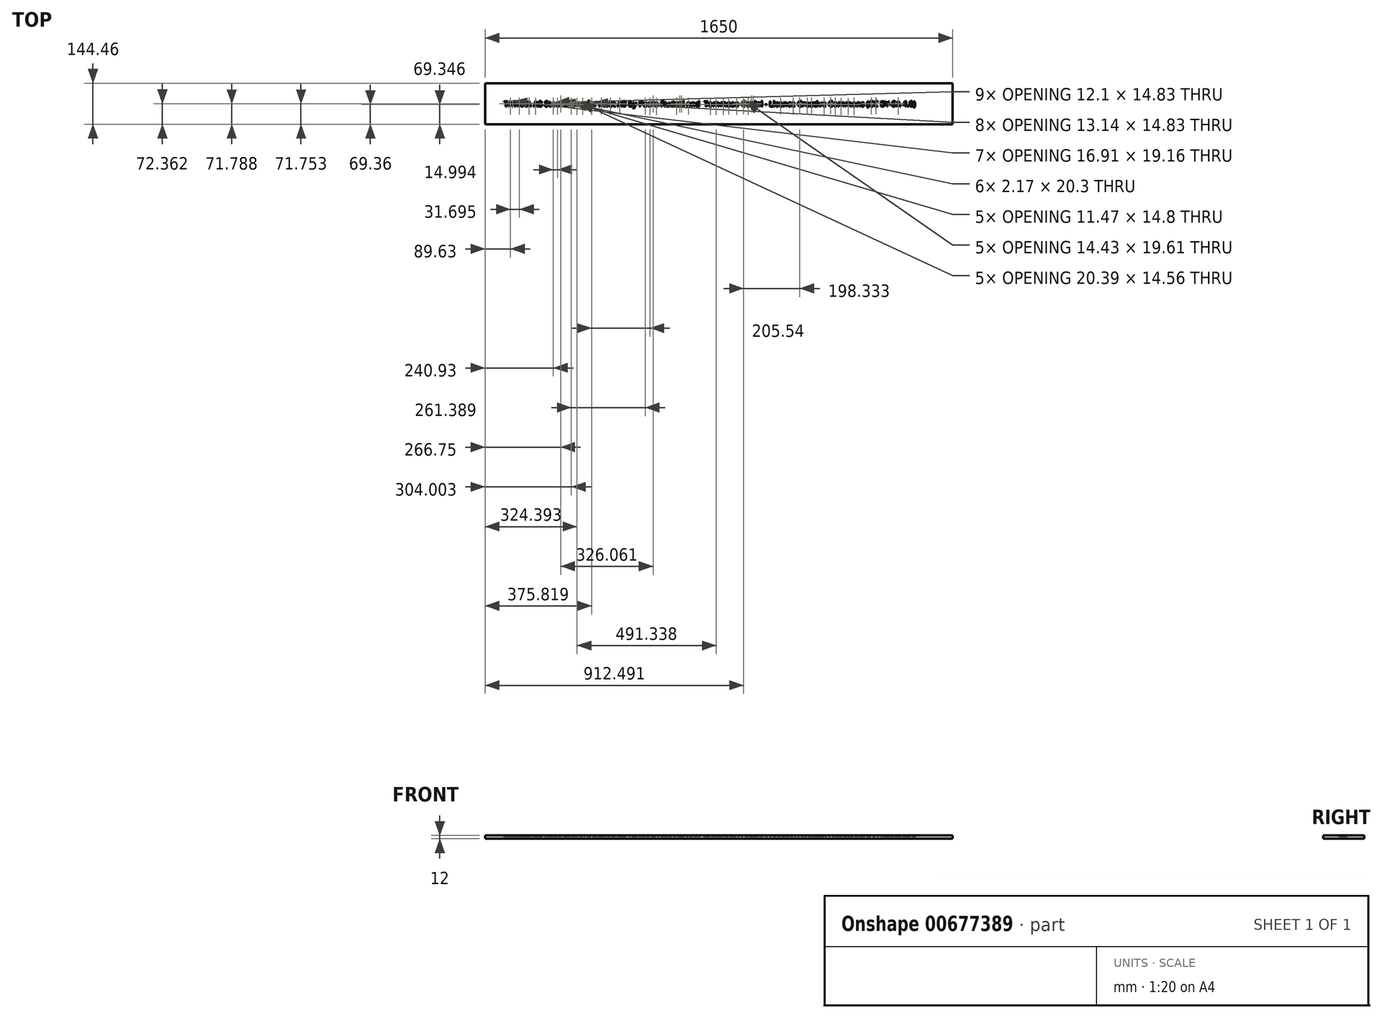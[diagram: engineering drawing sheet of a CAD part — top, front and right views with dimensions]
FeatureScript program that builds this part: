
annotation { "Feature Type Name" : "Feature", "Feature Type Description" : "" }
export const myFeature = defineFeature(function(context is Context, id is Id, definition is map)
    precondition{}
    {
        {
            var Q0;
            Q0=qCreatedBy(makeId("Top.planeOp"),FACE);
            var sketch = newSketch(context, id + "F0", { "sketchPlane" : qUnion([Q0])});
            skText(sketch, "E0", { "text": "TATARA A8 Steel frame for Anet A8 by Paolo Rudelli and  Tommaso Collini - Licence Creative Commons (CC BY-SA 4.0)", "fontName": "OpenSans-Regular.ttf"});
            const initialGuessF0  = {"E0": [-0.56495, -0.011, 1, 0, 0.01924]};
            skSetInitialGuess(sketch, initialGuessF0);
            skSolve(sketch);
        }
        {
            var Q0;
            Q0=qCreatedBy(makeId("Top.planeOp"),FACE);
            var sketch = newSketch(context, id + "F1", { "sketchPlane" : qUnion([Q0])});
            skLineSegment(sketch, "E1.bottom", {"start": v(-631.34, 71.25) * mm, "end": v(1018.66, 71.25) * mm});
            skLineSegment(sketch, "E1.top", {"start": v(-631.34, -73.21) * mm, "end": v(1018.66, -73.21) * mm});
            skLineSegment(sketch, "E1.left", {"start": v(-631.34, 71.25) * mm, "end": v(-631.34, -73.21) * mm});
            skLineSegment(sketch, "E1.right", {"start": v(1018.66, 71.25) * mm, "end": v(1018.66, -73.21) * mm});
            skSolve(sketch);
        }
        {
            var Q0;
            Q0 = qSketchRegion(id + "F0", true);
            extrude(context, id + "F2", {"entities" : qUnion([Q0]), "depth" : 25 * mm, "offsetDistance" : 25 * mm});
        }
        {
            var Q0;
            Q0=makeQuery(id+"F1.imprint","IMPRINT",FACE,{"disambiguationData":[TD([[makeQuery(id+"F1.imprint","IMPRINT",EDGE,{"derivedFrom":sQuery(id+"F1.wireOp",EDGE,"E1.bottom")}),-1.0]])]});
            extrude(context, id + "F3", {"entities" : qUnion([Q0]), "depth" : 18 * mm, "offsetDistance" : 25 * mm, "hasSecondDirection" : true, "secondDirectionOppositeDirection" : false, "secondDirectionDepth" : 6 * mm});
        }
        {
            var Q0;
            Q0=makeQuery(id+"F2.opExtrude","SWEPT_BODY",BODY,{"disambiguationData":[OSD([sQuery(id+"F0.wireOp",EDGE,"E0.sketch_text.stroke-1756"),sQuery(id+"F0.wireOp",EDGE,"E0.sketch_text.stroke-1757"),sQuery(id+"F0.wireOp",EDGE,"E0.sketch_text.stroke-1758"),sQuery(id+"F0.wireOp",EDGE,"E0.sketch_text.stroke-1759"),sQuery(id+"F0.wireOp",EDGE,"E0.sketch_text.stroke-1760"),sQuery(id+"F0.wireOp",EDGE,"E0.sketch_text.stroke-1761"),sQuery(id+"F0.wireOp",EDGE,"E0.sketch_text.stroke-1762"),sQuery(id+"F0.wireOp",EDGE,"E0.sketch_text.stroke-1763"),sQuery(id+"F0.wireOp",EDGE,"E0.sketch_text.stroke-1764"),sQuery(id+"F0.wireOp",EDGE,"E0.sketch_text.stroke-1765"),sQuery(id+"F0.wireOp",EDGE,"E0.sketch_text.stroke-1766"),sQuery(id+"F0.wireOp",EDGE,"E0.sketch_text.stroke-1767"),sQuery(id+"F0.wireOp",EDGE,"E0.sketch_text.stroke-1768"),sQuery(id+"F0.wireOp",EDGE,"E0.sketch_text.stroke-1769"),sQuery(id+"F0.wireOp",EDGE,"E0.sketch_text.stroke-1770"),sQuery(id+"F0.wireOp",EDGE,"E0.sketch_text.stroke-1771"),sQuery(id+"F0.wireOp",EDGE,"E0.sketch_text.stroke-1772"),sQuery(id+"F0.wireOp",EDGE,"E0.sketch_text.stroke-1773"),sQuery(id+"F0.wireOp",EDGE,"E0.sketch_text.stroke-1774")])]});
            var Q1;
            Q1=makeQuery(id+"F2.opExtrude","SWEPT_BODY",BODY,{"disambiguationData":[OSD([sQuery(id+"F0.wireOp",EDGE,"E0.sketch_text.stroke-1705"),sQuery(id+"F0.wireOp",EDGE,"E0.sketch_text.stroke-1706"),sQuery(id+"F0.wireOp",EDGE,"E0.sketch_text.stroke-1707"),sQuery(id+"F0.wireOp",EDGE,"E0.sketch_text.stroke-1708"),sQuery(id+"F0.wireOp",EDGE,"E0.sketch_text.stroke-1709"),sQuery(id+"F0.wireOp",EDGE,"E0.sketch_text.stroke-1710"),sQuery(id+"F0.wireOp",EDGE,"E0.sketch_text.stroke-1711"),sQuery(id+"F0.wireOp",EDGE,"E0.sketch_text.stroke-1712"),sQuery(id+"F0.wireOp",EDGE,"E0.sketch_text.stroke-1713"),sQuery(id+"F0.wireOp",EDGE,"E0.sketch_text.stroke-1714"),sQuery(id+"F0.wireOp",EDGE,"E0.sketch_text.stroke-1715"),sQuery(id+"F0.wireOp",EDGE,"E0.sketch_text.stroke-1716"),sQuery(id+"F0.wireOp",EDGE,"E0.sketch_text.stroke-1717"),sQuery(id+"F0.wireOp",EDGE,"E0.sketch_text.stroke-1718"),sQuery(id+"F0.wireOp",EDGE,"E0.sketch_text.stroke-1719"),sQuery(id+"F0.wireOp",EDGE,"E0.sketch_text.stroke-1720"),sQuery(id+"F0.wireOp",EDGE,"E0.sketch_text.stroke-1721"),sQuery(id+"F0.wireOp",EDGE,"E0.sketch_text.stroke-1722"),sQuery(id+"F0.wireOp",EDGE,"E0.sketch_text.stroke-1723")])]});
            var Q2;
            Q2=makeQuery(id+"F2.opExtrude","SWEPT_BODY",BODY,{"disambiguationData":[OSD([sQuery(id+"F0.wireOp",EDGE,"E0.sketch_text.stroke-1682"),sQuery(id+"F0.wireOp",EDGE,"E0.sketch_text.stroke-1683"),sQuery(id+"F0.wireOp",EDGE,"E0.sketch_text.stroke-1684"),sQuery(id+"F0.wireOp",EDGE,"E0.sketch_text.stroke-1685"),sQuery(id+"F0.wireOp",EDGE,"E0.sketch_text.stroke-1686"),sQuery(id+"F0.wireOp",EDGE,"E0.sketch_text.stroke-1687"),sQuery(id+"F0.wireOp",EDGE,"E0.sketch_text.stroke-1688"),sQuery(id+"F0.wireOp",EDGE,"E0.sketch_text.stroke-1689")])]});
            var Q3;
            Q3=makeQuery(id+"F2.opExtrude","SWEPT_BODY",BODY,{"disambiguationData":[OSD([sQuery(id+"F0.wireOp",EDGE,"E0.sketch_text.stroke-1690"),sQuery(id+"F0.wireOp",EDGE,"E0.sketch_text.stroke-1691"),sQuery(id+"F0.wireOp",EDGE,"E0.sketch_text.stroke-1692"),sQuery(id+"F0.wireOp",EDGE,"E0.sketch_text.stroke-1693"),sQuery(id+"F0.wireOp",EDGE,"E0.sketch_text.stroke-1694"),sQuery(id+"F0.wireOp",EDGE,"E0.sketch_text.stroke-1695"),sQuery(id+"F0.wireOp",EDGE,"E0.sketch_text.stroke-1696"),sQuery(id+"F0.wireOp",EDGE,"E0.sketch_text.stroke-1697"),sQuery(id+"F0.wireOp",EDGE,"E0.sketch_text.stroke-1698"),sQuery(id+"F0.wireOp",EDGE,"E0.sketch_text.stroke-1699"),sQuery(id+"F0.wireOp",EDGE,"E0.sketch_text.stroke-1700"),sQuery(id+"F0.wireOp",EDGE,"E0.sketch_text.stroke-1701"),sQuery(id+"F0.wireOp",EDGE,"E0.sketch_text.stroke-1702"),sQuery(id+"F0.wireOp",EDGE,"E0.sketch_text.stroke-1703"),sQuery(id+"F0.wireOp",EDGE,"E0.sketch_text.stroke-1704")])]});
            var Q4;
            Q4=makeQuery(id+"F2.opExtrude","SWEPT_BODY",BODY,{"disambiguationData":[OSD([sQuery(id+"F0.wireOp",EDGE,"E0.sketch_text.stroke-1741"),sQuery(id+"F0.wireOp",EDGE,"E0.sketch_text.stroke-1742"),sQuery(id+"F0.wireOp",EDGE,"E0.sketch_text.stroke-1743"),sQuery(id+"F0.wireOp",EDGE,"E0.sketch_text.stroke-1744"),sQuery(id+"F0.wireOp",EDGE,"E0.sketch_text.stroke-1745"),sQuery(id+"F0.wireOp",EDGE,"E0.sketch_text.stroke-1746"),sQuery(id+"F0.wireOp",EDGE,"E0.sketch_text.stroke-1747"),sQuery(id+"F0.wireOp",EDGE,"E0.sketch_text.stroke-1748"),sQuery(id+"F0.wireOp",EDGE,"E0.sketch_text.stroke-1749"),sQuery(id+"F0.wireOp",EDGE,"E0.sketch_text.stroke-1750"),sQuery(id+"F0.wireOp",EDGE,"E0.sketch_text.stroke-1751"),sQuery(id+"F0.wireOp",EDGE,"E0.sketch_text.stroke-1752"),sQuery(id+"F0.wireOp",EDGE,"E0.sketch_text.stroke-1753"),sQuery(id+"F0.wireOp",EDGE,"E0.sketch_text.stroke-1754"),sQuery(id+"F0.wireOp",EDGE,"E0.sketch_text.stroke-1755")])]});
            var Q5;
            Q5=makeQuery(id+"F2.opExtrude","SWEPT_BODY",BODY,{"disambiguationData":[OSD([sQuery(id+"F0.wireOp",EDGE,"E0.sketch_text.stroke-0"),sQuery(id+"F0.wireOp",EDGE,"E0.sketch_text.stroke-1"),sQuery(id+"F0.wireOp",EDGE,"E0.sketch_text.stroke-2"),sQuery(id+"F0.wireOp",EDGE,"E0.sketch_text.stroke-3"),sQuery(id+"F0.wireOp",EDGE,"E0.sketch_text.stroke-4"),sQuery(id+"F0.wireOp",EDGE,"E0.sketch_text.stroke-5"),sQuery(id+"F0.wireOp",EDGE,"E0.sketch_text.stroke-6"),sQuery(id+"F0.wireOp",EDGE,"E0.sketch_text.stroke-7")])]});
            var Q6;
            Q6=makeQuery(id+"F2.opExtrude","SWEPT_BODY",BODY,{"disambiguationData":[OSD([sQuery(id+"F0.wireOp",EDGE,"E0.sketch_text.stroke-8"),sQuery(id+"F0.wireOp",EDGE,"E0.sketch_text.stroke-9"),sQuery(id+"F0.wireOp",EDGE,"E0.sketch_text.stroke-10"),sQuery(id+"F0.wireOp",EDGE,"E0.sketch_text.stroke-11"),sQuery(id+"F0.wireOp",EDGE,"E0.sketch_text.stroke-12"),sQuery(id+"F0.wireOp",EDGE,"E0.sketch_text.stroke-13"),sQuery(id+"F0.wireOp",EDGE,"E0.sketch_text.stroke-14"),sQuery(id+"F0.wireOp",EDGE,"E0.sketch_text.stroke-15"),sQuery(id+"F0.wireOp",EDGE,"E0.sketch_text.stroke-16"),sQuery(id+"F0.wireOp",EDGE,"E0.sketch_text.stroke-17"),sQuery(id+"F0.wireOp",EDGE,"E0.sketch_text.stroke-18"),sQuery(id+"F0.wireOp",EDGE,"E0.sketch_text.stroke-19"),sQuery(id+"F0.wireOp",EDGE,"E0.sketch_text.stroke-20")])]});
            var Q7;
            Q7=makeQuery(id+"F2.opExtrude","SWEPT_BODY",BODY,{"disambiguationData":[OSD([sQuery(id+"F0.wireOp",EDGE,"E0.sketch_text.stroke-21"),sQuery(id+"F0.wireOp",EDGE,"E0.sketch_text.stroke-22"),sQuery(id+"F0.wireOp",EDGE,"E0.sketch_text.stroke-23"),sQuery(id+"F0.wireOp",EDGE,"E0.sketch_text.stroke-24"),sQuery(id+"F0.wireOp",EDGE,"E0.sketch_text.stroke-25"),sQuery(id+"F0.wireOp",EDGE,"E0.sketch_text.stroke-26"),sQuery(id+"F0.wireOp",EDGE,"E0.sketch_text.stroke-27"),sQuery(id+"F0.wireOp",EDGE,"E0.sketch_text.stroke-28")])]});
            var Q8;
            Q8=makeQuery(id+"F2.opExtrude","SWEPT_BODY",BODY,{"disambiguationData":[OSD([sQuery(id+"F0.wireOp",EDGE,"E0.sketch_text.stroke-29"),sQuery(id+"F0.wireOp",EDGE,"E0.sketch_text.stroke-30"),sQuery(id+"F0.wireOp",EDGE,"E0.sketch_text.stroke-31"),sQuery(id+"F0.wireOp",EDGE,"E0.sketch_text.stroke-32"),sQuery(id+"F0.wireOp",EDGE,"E0.sketch_text.stroke-33"),sQuery(id+"F0.wireOp",EDGE,"E0.sketch_text.stroke-34"),sQuery(id+"F0.wireOp",EDGE,"E0.sketch_text.stroke-35"),sQuery(id+"F0.wireOp",EDGE,"E0.sketch_text.stroke-36"),sQuery(id+"F0.wireOp",EDGE,"E0.sketch_text.stroke-37"),sQuery(id+"F0.wireOp",EDGE,"E0.sketch_text.stroke-38"),sQuery(id+"F0.wireOp",EDGE,"E0.sketch_text.stroke-39"),sQuery(id+"F0.wireOp",EDGE,"E0.sketch_text.stroke-40"),sQuery(id+"F0.wireOp",EDGE,"E0.sketch_text.stroke-41")])]});
            var Q9;
            Q9=makeQuery(id+"F2.opExtrude","SWEPT_BODY",BODY,{"disambiguationData":[OSD([sQuery(id+"F0.wireOp",EDGE,"E0.sketch_text.stroke-42"),sQuery(id+"F0.wireOp",EDGE,"E0.sketch_text.stroke-43"),sQuery(id+"F0.wireOp",EDGE,"E0.sketch_text.stroke-44"),sQuery(id+"F0.wireOp",EDGE,"E0.sketch_text.stroke-45"),sQuery(id+"F0.wireOp",EDGE,"E0.sketch_text.stroke-46"),sQuery(id+"F0.wireOp",EDGE,"E0.sketch_text.stroke-47"),sQuery(id+"F0.wireOp",EDGE,"E0.sketch_text.stroke-48"),sQuery(id+"F0.wireOp",EDGE,"E0.sketch_text.stroke-49"),sQuery(id+"F0.wireOp",EDGE,"E0.sketch_text.stroke-50"),sQuery(id+"F0.wireOp",EDGE,"E0.sketch_text.stroke-51"),sQuery(id+"F0.wireOp",EDGE,"E0.sketch_text.stroke-52"),sQuery(id+"F0.wireOp",EDGE,"E0.sketch_text.stroke-53"),sQuery(id+"F0.wireOp",EDGE,"E0.sketch_text.stroke-54"),sQuery(id+"F0.wireOp",EDGE,"E0.sketch_text.stroke-55"),sQuery(id+"F0.wireOp",EDGE,"E0.sketch_text.stroke-56"),sQuery(id+"F0.wireOp",EDGE,"E0.sketch_text.stroke-57"),sQuery(id+"F0.wireOp",EDGE,"E0.sketch_text.stroke-58"),sQuery(id+"F0.wireOp",EDGE,"E0.sketch_text.stroke-59")])]});
            var Q10;
            Q10=makeQuery(id+"F2.opExtrude","SWEPT_BODY",BODY,{"disambiguationData":[OSD([sQuery(id+"F0.wireOp",EDGE,"E0.sketch_text.stroke-60"),sQuery(id+"F0.wireOp",EDGE,"E0.sketch_text.stroke-61"),sQuery(id+"F0.wireOp",EDGE,"E0.sketch_text.stroke-62"),sQuery(id+"F0.wireOp",EDGE,"E0.sketch_text.stroke-63"),sQuery(id+"F0.wireOp",EDGE,"E0.sketch_text.stroke-64"),sQuery(id+"F0.wireOp",EDGE,"E0.sketch_text.stroke-65"),sQuery(id+"F0.wireOp",EDGE,"E0.sketch_text.stroke-66"),sQuery(id+"F0.wireOp",EDGE,"E0.sketch_text.stroke-67"),sQuery(id+"F0.wireOp",EDGE,"E0.sketch_text.stroke-68"),sQuery(id+"F0.wireOp",EDGE,"E0.sketch_text.stroke-69"),sQuery(id+"F0.wireOp",EDGE,"E0.sketch_text.stroke-70"),sQuery(id+"F0.wireOp",EDGE,"E0.sketch_text.stroke-71"),sQuery(id+"F0.wireOp",EDGE,"E0.sketch_text.stroke-72")])]});
            var Q11;
            Q11=makeQuery(id+"F2.opExtrude","SWEPT_BODY",BODY,{"disambiguationData":[OSD([sQuery(id+"F0.wireOp",EDGE,"E0.sketch_text.stroke-73"),sQuery(id+"F0.wireOp",EDGE,"E0.sketch_text.stroke-74"),sQuery(id+"F0.wireOp",EDGE,"E0.sketch_text.stroke-75"),sQuery(id+"F0.wireOp",EDGE,"E0.sketch_text.stroke-76"),sQuery(id+"F0.wireOp",EDGE,"E0.sketch_text.stroke-77"),sQuery(id+"F0.wireOp",EDGE,"E0.sketch_text.stroke-78"),sQuery(id+"F0.wireOp",EDGE,"E0.sketch_text.stroke-79"),sQuery(id+"F0.wireOp",EDGE,"E0.sketch_text.stroke-80"),sQuery(id+"F0.wireOp",EDGE,"E0.sketch_text.stroke-81"),sQuery(id+"F0.wireOp",EDGE,"E0.sketch_text.stroke-82"),sQuery(id+"F0.wireOp",EDGE,"E0.sketch_text.stroke-83"),sQuery(id+"F0.wireOp",EDGE,"E0.sketch_text.stroke-84"),sQuery(id+"F0.wireOp",EDGE,"E0.sketch_text.stroke-85"),sQuery(id+"F0.wireOp",EDGE,"E0.sketch_text.stroke-86"),sQuery(id+"F0.wireOp",EDGE,"E0.sketch_text.stroke-87"),sQuery(id+"F0.wireOp",EDGE,"E0.sketch_text.stroke-88"),sQuery(id+"F0.wireOp",EDGE,"E0.sketch_text.stroke-89"),sQuery(id+"F0.wireOp",EDGE,"E0.sketch_text.stroke-90"),sQuery(id+"F0.wireOp",EDGE,"E0.sketch_text.stroke-91")])]});
            var Q12;
            Q12=makeQuery(id+"F2.opExtrude","SWEPT_BODY",BODY,{"disambiguationData":[OSD([sQuery(id+"F0.wireOp",EDGE,"E0.sketch_text.stroke-92"),sQuery(id+"F0.wireOp",EDGE,"E0.sketch_text.stroke-93"),sQuery(id+"F0.wireOp",EDGE,"E0.sketch_text.stroke-94"),sQuery(id+"F0.wireOp",EDGE,"E0.sketch_text.stroke-95"),sQuery(id+"F0.wireOp",EDGE,"E0.sketch_text.stroke-96"),sQuery(id+"F0.wireOp",EDGE,"E0.sketch_text.stroke-97"),sQuery(id+"F0.wireOp",EDGE,"E0.sketch_text.stroke-98"),sQuery(id+"F0.wireOp",EDGE,"E0.sketch_text.stroke-99"),sQuery(id+"F0.wireOp",EDGE,"E0.sketch_text.stroke-100"),sQuery(id+"F0.wireOp",EDGE,"E0.sketch_text.stroke-101"),sQuery(id+"F0.wireOp",EDGE,"E0.sketch_text.stroke-102"),sQuery(id+"F0.wireOp",EDGE,"E0.sketch_text.stroke-103")])]});
            var Q13;
            Q13=makeQuery(id+"F2.opExtrude","SWEPT_BODY",BODY,{"disambiguationData":[OSD([sQuery(id+"F0.wireOp",EDGE,"E0.sketch_text.stroke-104"),sQuery(id+"F0.wireOp",EDGE,"E0.sketch_text.stroke-105"),sQuery(id+"F0.wireOp",EDGE,"E0.sketch_text.stroke-106"),sQuery(id+"F0.wireOp",EDGE,"E0.sketch_text.stroke-107"),sQuery(id+"F0.wireOp",EDGE,"E0.sketch_text.stroke-108"),sQuery(id+"F0.wireOp",EDGE,"E0.sketch_text.stroke-109"),sQuery(id+"F0.wireOp",EDGE,"E0.sketch_text.stroke-110"),sQuery(id+"F0.wireOp",EDGE,"E0.sketch_text.stroke-111"),sQuery(id+"F0.wireOp",EDGE,"E0.sketch_text.stroke-112"),sQuery(id+"F0.wireOp",EDGE,"E0.sketch_text.stroke-113"),sQuery(id+"F0.wireOp",EDGE,"E0.sketch_text.stroke-114"),sQuery(id+"F0.wireOp",EDGE,"E0.sketch_text.stroke-115"),sQuery(id+"F0.wireOp",EDGE,"E0.sketch_text.stroke-116"),sQuery(id+"F0.wireOp",EDGE,"E0.sketch_text.stroke-117"),sQuery(id+"F0.wireOp",EDGE,"E0.sketch_text.stroke-118"),sQuery(id+"F0.wireOp",EDGE,"E0.sketch_text.stroke-119"),sQuery(id+"F0.wireOp",EDGE,"E0.sketch_text.stroke-120"),sQuery(id+"F0.wireOp",EDGE,"E0.sketch_text.stroke-121"),sQuery(id+"F0.wireOp",EDGE,"E0.sketch_text.stroke-122")])]});
            var Q14;
            Q14=makeQuery(id+"F2.opExtrude","SWEPT_BODY",BODY,{"disambiguationData":[OSD([sQuery(id+"F0.wireOp",EDGE,"E0.sketch_text.stroke-123"),sQuery(id+"F0.wireOp",EDGE,"E0.sketch_text.stroke-124"),sQuery(id+"F0.wireOp",EDGE,"E0.sketch_text.stroke-125"),sQuery(id+"F0.wireOp",EDGE,"E0.sketch_text.stroke-126"),sQuery(id+"F0.wireOp",EDGE,"E0.sketch_text.stroke-127"),sQuery(id+"F0.wireOp",EDGE,"E0.sketch_text.stroke-128"),sQuery(id+"F0.wireOp",EDGE,"E0.sketch_text.stroke-129"),sQuery(id+"F0.wireOp",EDGE,"E0.sketch_text.stroke-130"),sQuery(id+"F0.wireOp",EDGE,"E0.sketch_text.stroke-131"),sQuery(id+"F0.wireOp",EDGE,"E0.sketch_text.stroke-132"),sQuery(id+"F0.wireOp",EDGE,"E0.sketch_text.stroke-133"),sQuery(id+"F0.wireOp",EDGE,"E0.sketch_text.stroke-134"),sQuery(id+"F0.wireOp",EDGE,"E0.sketch_text.stroke-135")])]});
            var Q15;
            Q15=makeQuery(id+"F2.opExtrude","SWEPT_BODY",BODY,{"disambiguationData":[OSD([sQuery(id+"F0.wireOp",EDGE,"E0.sketch_text.stroke-136"),sQuery(id+"F0.wireOp",EDGE,"E0.sketch_text.stroke-137"),sQuery(id+"F0.wireOp",EDGE,"E0.sketch_text.stroke-138"),sQuery(id+"F0.wireOp",EDGE,"E0.sketch_text.stroke-139"),sQuery(id+"F0.wireOp",EDGE,"E0.sketch_text.stroke-140"),sQuery(id+"F0.wireOp",EDGE,"E0.sketch_text.stroke-141"),sQuery(id+"F0.wireOp",EDGE,"E0.sketch_text.stroke-142"),sQuery(id+"F0.wireOp",EDGE,"E0.sketch_text.stroke-143"),sQuery(id+"F0.wireOp",EDGE,"E0.sketch_text.stroke-144"),sQuery(id+"F0.wireOp",EDGE,"E0.sketch_text.stroke-145"),sQuery(id+"F0.wireOp",EDGE,"E0.sketch_text.stroke-146"),sQuery(id+"F0.wireOp",EDGE,"E0.sketch_text.stroke-147"),sQuery(id+"F0.wireOp",EDGE,"E0.sketch_text.stroke-148"),sQuery(id+"F0.wireOp",EDGE,"E0.sketch_text.stroke-149"),sQuery(id+"F0.wireOp",EDGE,"E0.sketch_text.stroke-150"),sQuery(id+"F0.wireOp",EDGE,"E0.sketch_text.stroke-151"),sQuery(id+"F0.wireOp",EDGE,"E0.sketch_text.stroke-152"),sQuery(id+"F0.wireOp",EDGE,"E0.sketch_text.stroke-153"),sQuery(id+"F0.wireOp",EDGE,"E0.sketch_text.stroke-154")])]});
            var Q16;
            Q16=makeQuery(id+"F2.opExtrude","SWEPT_BODY",BODY,{"disambiguationData":[OSD([sQuery(id+"F0.wireOp",EDGE,"E0.sketch_text.stroke-155"),sQuery(id+"F0.wireOp",EDGE,"E0.sketch_text.stroke-156"),sQuery(id+"F0.wireOp",EDGE,"E0.sketch_text.stroke-157"),sQuery(id+"F0.wireOp",EDGE,"E0.sketch_text.stroke-158"),sQuery(id+"F0.wireOp",EDGE,"E0.sketch_text.stroke-159"),sQuery(id+"F0.wireOp",EDGE,"E0.sketch_text.stroke-160"),sQuery(id+"F0.wireOp",EDGE,"E0.sketch_text.stroke-161"),sQuery(id+"F0.wireOp",EDGE,"E0.sketch_text.stroke-162"),sQuery(id+"F0.wireOp",EDGE,"E0.sketch_text.stroke-163"),sQuery(id+"F0.wireOp",EDGE,"E0.sketch_text.stroke-164"),sQuery(id+"F0.wireOp",EDGE,"E0.sketch_text.stroke-165"),sQuery(id+"F0.wireOp",EDGE,"E0.sketch_text.stroke-166"),sQuery(id+"F0.wireOp",EDGE,"E0.sketch_text.stroke-167"),sQuery(id+"F0.wireOp",EDGE,"E0.sketch_text.stroke-168"),sQuery(id+"F0.wireOp",EDGE,"E0.sketch_text.stroke-169"),sQuery(id+"F0.wireOp",EDGE,"E0.sketch_text.stroke-170"),sQuery(id+"F0.wireOp",EDGE,"E0.sketch_text.stroke-171"),sQuery(id+"F0.wireOp",EDGE,"E0.sketch_text.stroke-172"),sQuery(id+"F0.wireOp",EDGE,"E0.sketch_text.stroke-173"),sQuery(id+"F0.wireOp",EDGE,"E0.sketch_text.stroke-174"),sQuery(id+"F0.wireOp",EDGE,"E0.sketch_text.stroke-175"),sQuery(id+"F0.wireOp",EDGE,"E0.sketch_text.stroke-176"),sQuery(id+"F0.wireOp",EDGE,"E0.sketch_text.stroke-177"),sQuery(id+"F0.wireOp",EDGE,"E0.sketch_text.stroke-178"),sQuery(id+"F0.wireOp",EDGE,"E0.sketch_text.stroke-179"),sQuery(id+"F0.wireOp",EDGE,"E0.sketch_text.stroke-180"),sQuery(id+"F0.wireOp",EDGE,"E0.sketch_text.stroke-181"),sQuery(id+"F0.wireOp",EDGE,"E0.sketch_text.stroke-182")])]});
            var Q17;
            Q17=makeQuery(id+"F2.opExtrude","SWEPT_BODY",BODY,{"disambiguationData":[OSD([sQuery(id+"F0.wireOp",EDGE,"E0.sketch_text.stroke-183"),sQuery(id+"F0.wireOp",EDGE,"E0.sketch_text.stroke-184"),sQuery(id+"F0.wireOp",EDGE,"E0.sketch_text.stroke-185"),sQuery(id+"F0.wireOp",EDGE,"E0.sketch_text.stroke-186"),sQuery(id+"F0.wireOp",EDGE,"E0.sketch_text.stroke-187"),sQuery(id+"F0.wireOp",EDGE,"E0.sketch_text.stroke-188"),sQuery(id+"F0.wireOp",EDGE,"E0.sketch_text.stroke-189"),sQuery(id+"F0.wireOp",EDGE,"E0.sketch_text.stroke-190"),sQuery(id+"F0.wireOp",EDGE,"E0.sketch_text.stroke-191"),sQuery(id+"F0.wireOp",EDGE,"E0.sketch_text.stroke-192"),sQuery(id+"F0.wireOp",EDGE,"E0.sketch_text.stroke-193"),sQuery(id+"F0.wireOp",EDGE,"E0.sketch_text.stroke-194"),sQuery(id+"F0.wireOp",EDGE,"E0.sketch_text.stroke-195"),sQuery(id+"F0.wireOp",EDGE,"E0.sketch_text.stroke-196"),sQuery(id+"F0.wireOp",EDGE,"E0.sketch_text.stroke-197"),sQuery(id+"F0.wireOp",EDGE,"E0.sketch_text.stroke-198"),sQuery(id+"F0.wireOp",EDGE,"E0.sketch_text.stroke-199"),sQuery(id+"F0.wireOp",EDGE,"E0.sketch_text.stroke-200"),sQuery(id+"F0.wireOp",EDGE,"E0.sketch_text.stroke-201")])]});
            var Q18;
            Q18=makeQuery(id+"F2.opExtrude","SWEPT_BODY",BODY,{"disambiguationData":[OSD([sQuery(id+"F0.wireOp",EDGE,"E0.sketch_text.stroke-202"),sQuery(id+"F0.wireOp",EDGE,"E0.sketch_text.stroke-203"),sQuery(id+"F0.wireOp",EDGE,"E0.sketch_text.stroke-204"),sQuery(id+"F0.wireOp",EDGE,"E0.sketch_text.stroke-205"),sQuery(id+"F0.wireOp",EDGE,"E0.sketch_text.stroke-206"),sQuery(id+"F0.wireOp",EDGE,"E0.sketch_text.stroke-207"),sQuery(id+"F0.wireOp",EDGE,"E0.sketch_text.stroke-208"),sQuery(id+"F0.wireOp",EDGE,"E0.sketch_text.stroke-209"),sQuery(id+"F0.wireOp",EDGE,"E0.sketch_text.stroke-210"),sQuery(id+"F0.wireOp",EDGE,"E0.sketch_text.stroke-211"),sQuery(id+"F0.wireOp",EDGE,"E0.sketch_text.stroke-212"),sQuery(id+"F0.wireOp",EDGE,"E0.sketch_text.stroke-213"),sQuery(id+"F0.wireOp",EDGE,"E0.sketch_text.stroke-214"),sQuery(id+"F0.wireOp",EDGE,"E0.sketch_text.stroke-215"),sQuery(id+"F0.wireOp",EDGE,"E0.sketch_text.stroke-216"),sQuery(id+"F0.wireOp",EDGE,"E0.sketch_text.stroke-217"),sQuery(id+"F0.wireOp",EDGE,"E0.sketch_text.stroke-218"),sQuery(id+"F0.wireOp",EDGE,"E0.sketch_text.stroke-219"),sQuery(id+"F0.wireOp",EDGE,"E0.sketch_text.stroke-220"),sQuery(id+"F0.wireOp",EDGE,"E0.sketch_text.stroke-221"),sQuery(id+"F0.wireOp",EDGE,"E0.sketch_text.stroke-222"),sQuery(id+"F0.wireOp",EDGE,"E0.sketch_text.stroke-223"),sQuery(id+"F0.wireOp",EDGE,"E0.sketch_text.stroke-224"),sQuery(id+"F0.wireOp",EDGE,"E0.sketch_text.stroke-225"),sQuery(id+"F0.wireOp",EDGE,"E0.sketch_text.stroke-226")])]});
            var Q19;
            Q19=makeQuery(id+"F2.opExtrude","SWEPT_BODY",BODY,{"disambiguationData":[OSD([sQuery(id+"F0.wireOp",EDGE,"E0.sketch_text.stroke-227"),sQuery(id+"F0.wireOp",EDGE,"E0.sketch_text.stroke-228"),sQuery(id+"F0.wireOp",EDGE,"E0.sketch_text.stroke-229"),sQuery(id+"F0.wireOp",EDGE,"E0.sketch_text.stroke-230"),sQuery(id+"F0.wireOp",EDGE,"E0.sketch_text.stroke-231"),sQuery(id+"F0.wireOp",EDGE,"E0.sketch_text.stroke-232"),sQuery(id+"F0.wireOp",EDGE,"E0.sketch_text.stroke-233"),sQuery(id+"F0.wireOp",EDGE,"E0.sketch_text.stroke-234"),sQuery(id+"F0.wireOp",EDGE,"E0.sketch_text.stroke-235"),sQuery(id+"F0.wireOp",EDGE,"E0.sketch_text.stroke-236"),sQuery(id+"F0.wireOp",EDGE,"E0.sketch_text.stroke-237"),sQuery(id+"F0.wireOp",EDGE,"E0.sketch_text.stroke-238"),sQuery(id+"F0.wireOp",EDGE,"E0.sketch_text.stroke-239"),sQuery(id+"F0.wireOp",EDGE,"E0.sketch_text.stroke-240"),sQuery(id+"F0.wireOp",EDGE,"E0.sketch_text.stroke-241"),sQuery(id+"F0.wireOp",EDGE,"E0.sketch_text.stroke-242"),sQuery(id+"F0.wireOp",EDGE,"E0.sketch_text.stroke-243"),sQuery(id+"F0.wireOp",EDGE,"E0.sketch_text.stroke-244"),sQuery(id+"F0.wireOp",EDGE,"E0.sketch_text.stroke-245")])]});
            var Q20;
            Q20=makeQuery(id+"F2.opExtrude","SWEPT_BODY",BODY,{"disambiguationData":[OSD([sQuery(id+"F0.wireOp",EDGE,"E0.sketch_text.stroke-246"),sQuery(id+"F0.wireOp",EDGE,"E0.sketch_text.stroke-247"),sQuery(id+"F0.wireOp",EDGE,"E0.sketch_text.stroke-248"),sQuery(id+"F0.wireOp",EDGE,"E0.sketch_text.stroke-249"),sQuery(id+"F0.wireOp",EDGE,"E0.sketch_text.stroke-250"),sQuery(id+"F0.wireOp",EDGE,"E0.sketch_text.stroke-251"),sQuery(id+"F0.wireOp",EDGE,"E0.sketch_text.stroke-252"),sQuery(id+"F0.wireOp",EDGE,"E0.sketch_text.stroke-253"),sQuery(id+"F0.wireOp",EDGE,"E0.sketch_text.stroke-254"),sQuery(id+"F0.wireOp",EDGE,"E0.sketch_text.stroke-255"),sQuery(id+"F0.wireOp",EDGE,"E0.sketch_text.stroke-256"),sQuery(id+"F0.wireOp",EDGE,"E0.sketch_text.stroke-257"),sQuery(id+"F0.wireOp",EDGE,"E0.sketch_text.stroke-258"),sQuery(id+"F0.wireOp",EDGE,"E0.sketch_text.stroke-259"),sQuery(id+"F0.wireOp",EDGE,"E0.sketch_text.stroke-260"),sQuery(id+"F0.wireOp",EDGE,"E0.sketch_text.stroke-261"),sQuery(id+"F0.wireOp",EDGE,"E0.sketch_text.stroke-262"),sQuery(id+"F0.wireOp",EDGE,"E0.sketch_text.stroke-263"),sQuery(id+"F0.wireOp",EDGE,"E0.sketch_text.stroke-264")])]});
            var Q21;
            Q21=makeQuery(id+"F2.opExtrude","SWEPT_BODY",BODY,{"disambiguationData":[OSD([sQuery(id+"F0.wireOp",EDGE,"E0.sketch_text.stroke-265"),sQuery(id+"F0.wireOp",EDGE,"E0.sketch_text.stroke-266"),sQuery(id+"F0.wireOp",EDGE,"E0.sketch_text.stroke-267"),sQuery(id+"F0.wireOp",EDGE,"E0.sketch_text.stroke-268"),sQuery(id+"F0.wireOp",EDGE,"E0.sketch_text.stroke-269"),sQuery(id+"F0.wireOp",EDGE,"E0.sketch_text.stroke-270"),sQuery(id+"F0.wireOp",EDGE,"E0.sketch_text.stroke-271"),sQuery(id+"F0.wireOp",EDGE,"E0.sketch_text.stroke-272"),sQuery(id+"F0.wireOp",EDGE,"E0.sketch_text.stroke-273"),sQuery(id+"F0.wireOp",EDGE,"E0.sketch_text.stroke-274"),sQuery(id+"F0.wireOp",EDGE,"E0.sketch_text.stroke-275"),sQuery(id+"F0.wireOp",EDGE,"E0.sketch_text.stroke-276"),sQuery(id+"F0.wireOp",EDGE,"E0.sketch_text.stroke-277"),sQuery(id+"F0.wireOp",EDGE,"E0.sketch_text.stroke-278"),sQuery(id+"F0.wireOp",EDGE,"E0.sketch_text.stroke-279"),sQuery(id+"F0.wireOp",EDGE,"E0.sketch_text.stroke-280"),sQuery(id+"F0.wireOp",EDGE,"E0.sketch_text.stroke-281"),sQuery(id+"F0.wireOp",EDGE,"E0.sketch_text.stroke-282"),sQuery(id+"F0.wireOp",EDGE,"E0.sketch_text.stroke-283")])]});
            var Q22;
            Q22=makeQuery(id+"F2.opExtrude","SWEPT_BODY",BODY,{"disambiguationData":[OSD([sQuery(id+"F0.wireOp",EDGE,"E0.sketch_text.stroke-284"),sQuery(id+"F0.wireOp",EDGE,"E0.sketch_text.stroke-285"),sQuery(id+"F0.wireOp",EDGE,"E0.sketch_text.stroke-286"),sQuery(id+"F0.wireOp",EDGE,"E0.sketch_text.stroke-287")])]});
            var Q23;
            Q23=makeQuery(id+"F2.opExtrude","SWEPT_BODY",BODY,{"disambiguationData":[OSD([sQuery(id+"F0.wireOp",EDGE,"E0.sketch_text.stroke-288"),sQuery(id+"F0.wireOp",EDGE,"E0.sketch_text.stroke-289"),sQuery(id+"F0.wireOp",EDGE,"E0.sketch_text.stroke-290"),sQuery(id+"F0.wireOp",EDGE,"E0.sketch_text.stroke-291"),sQuery(id+"F0.wireOp",EDGE,"E0.sketch_text.stroke-292"),sQuery(id+"F0.wireOp",EDGE,"E0.sketch_text.stroke-293"),sQuery(id+"F0.wireOp",EDGE,"E0.sketch_text.stroke-294"),sQuery(id+"F0.wireOp",EDGE,"E0.sketch_text.stroke-295"),sQuery(id+"F0.wireOp",EDGE,"E0.sketch_text.stroke-296"),sQuery(id+"F0.wireOp",EDGE,"E0.sketch_text.stroke-297"),sQuery(id+"F0.wireOp",EDGE,"E0.sketch_text.stroke-298"),sQuery(id+"F0.wireOp",EDGE,"E0.sketch_text.stroke-299"),sQuery(id+"F0.wireOp",EDGE,"E0.sketch_text.stroke-300"),sQuery(id+"F0.wireOp",EDGE,"E0.sketch_text.stroke-301"),sQuery(id+"F0.wireOp",EDGE,"E0.sketch_text.stroke-302"),sQuery(id+"F0.wireOp",EDGE,"E0.sketch_text.stroke-303"),sQuery(id+"F0.wireOp",EDGE,"E0.sketch_text.stroke-304")])]});
            var Q24;
            Q24=makeQuery(id+"F2.opExtrude","SWEPT_BODY",BODY,{"disambiguationData":[OSD([sQuery(id+"F0.wireOp",EDGE,"E0.sketch_text.stroke-305"),sQuery(id+"F0.wireOp",EDGE,"E0.sketch_text.stroke-306"),sQuery(id+"F0.wireOp",EDGE,"E0.sketch_text.stroke-307"),sQuery(id+"F0.wireOp",EDGE,"E0.sketch_text.stroke-308"),sQuery(id+"F0.wireOp",EDGE,"E0.sketch_text.stroke-309"),sQuery(id+"F0.wireOp",EDGE,"E0.sketch_text.stroke-310"),sQuery(id+"F0.wireOp",EDGE,"E0.sketch_text.stroke-311"),sQuery(id+"F0.wireOp",EDGE,"E0.sketch_text.stroke-312"),sQuery(id+"F0.wireOp",EDGE,"E0.sketch_text.stroke-313"),sQuery(id+"F0.wireOp",EDGE,"E0.sketch_text.stroke-314"),sQuery(id+"F0.wireOp",EDGE,"E0.sketch_text.stroke-315"),sQuery(id+"F0.wireOp",EDGE,"E0.sketch_text.stroke-316"),sQuery(id+"F0.wireOp",EDGE,"E0.sketch_text.stroke-317")])]});
            var Q25;
            Q25=makeQuery(id+"F2.opExtrude","SWEPT_BODY",BODY,{"disambiguationData":[OSD([sQuery(id+"F0.wireOp",EDGE,"E0.sketch_text.stroke-318"),sQuery(id+"F0.wireOp",EDGE,"E0.sketch_text.stroke-319"),sQuery(id+"F0.wireOp",EDGE,"E0.sketch_text.stroke-320"),sQuery(id+"F0.wireOp",EDGE,"E0.sketch_text.stroke-321"),sQuery(id+"F0.wireOp",EDGE,"E0.sketch_text.stroke-322"),sQuery(id+"F0.wireOp",EDGE,"E0.sketch_text.stroke-323"),sQuery(id+"F0.wireOp",EDGE,"E0.sketch_text.stroke-324"),sQuery(id+"F0.wireOp",EDGE,"E0.sketch_text.stroke-325"),sQuery(id+"F0.wireOp",EDGE,"E0.sketch_text.stroke-326"),sQuery(id+"F0.wireOp",EDGE,"E0.sketch_text.stroke-327"),sQuery(id+"F0.wireOp",EDGE,"E0.sketch_text.stroke-328"),sQuery(id+"F0.wireOp",EDGE,"E0.sketch_text.stroke-329"),sQuery(id+"F0.wireOp",EDGE,"E0.sketch_text.stroke-330"),sQuery(id+"F0.wireOp",EDGE,"E0.sketch_text.stroke-331"),sQuery(id+"F0.wireOp",EDGE,"E0.sketch_text.stroke-332"),sQuery(id+"F0.wireOp",EDGE,"E0.sketch_text.stroke-333"),sQuery(id+"F0.wireOp",EDGE,"E0.sketch_text.stroke-334"),sQuery(id+"F0.wireOp",EDGE,"E0.sketch_text.stroke-335"),sQuery(id+"F0.wireOp",EDGE,"E0.sketch_text.stroke-336"),sQuery(id+"F0.wireOp",EDGE,"E0.sketch_text.stroke-337"),sQuery(id+"F0.wireOp",EDGE,"E0.sketch_text.stroke-338"),sQuery(id+"F0.wireOp",EDGE,"E0.sketch_text.stroke-339"),sQuery(id+"F0.wireOp",EDGE,"E0.sketch_text.stroke-340"),sQuery(id+"F0.wireOp",EDGE,"E0.sketch_text.stroke-341"),sQuery(id+"F0.wireOp",EDGE,"E0.sketch_text.stroke-342"),sQuery(id+"F0.wireOp",EDGE,"E0.sketch_text.stroke-343"),sQuery(id+"F0.wireOp",EDGE,"E0.sketch_text.stroke-344")])]});
            var Q26;
            Q26=makeQuery(id+"F2.opExtrude","SWEPT_BODY",BODY,{"disambiguationData":[OSD([sQuery(id+"F0.wireOp",EDGE,"E0.sketch_text.stroke-345"),sQuery(id+"F0.wireOp",EDGE,"E0.sketch_text.stroke-346"),sQuery(id+"F0.wireOp",EDGE,"E0.sketch_text.stroke-347"),sQuery(id+"F0.wireOp",EDGE,"E0.sketch_text.stroke-348"),sQuery(id+"F0.wireOp",EDGE,"E0.sketch_text.stroke-349"),sQuery(id+"F0.wireOp",EDGE,"E0.sketch_text.stroke-350"),sQuery(id+"F0.wireOp",EDGE,"E0.sketch_text.stroke-351"),sQuery(id+"F0.wireOp",EDGE,"E0.sketch_text.stroke-352"),sQuery(id+"F0.wireOp",EDGE,"E0.sketch_text.stroke-353"),sQuery(id+"F0.wireOp",EDGE,"E0.sketch_text.stroke-354"),sQuery(id+"F0.wireOp",EDGE,"E0.sketch_text.stroke-355"),sQuery(id+"F0.wireOp",EDGE,"E0.sketch_text.stroke-356"),sQuery(id+"F0.wireOp",EDGE,"E0.sketch_text.stroke-357"),sQuery(id+"F0.wireOp",EDGE,"E0.sketch_text.stroke-358"),sQuery(id+"F0.wireOp",EDGE,"E0.sketch_text.stroke-359"),sQuery(id+"F0.wireOp",EDGE,"E0.sketch_text.stroke-360"),sQuery(id+"F0.wireOp",EDGE,"E0.sketch_text.stroke-361"),sQuery(id+"F0.wireOp",EDGE,"E0.sketch_text.stroke-362"),sQuery(id+"F0.wireOp",EDGE,"E0.sketch_text.stroke-363"),sQuery(id+"F0.wireOp",EDGE,"E0.sketch_text.stroke-364"),sQuery(id+"F0.wireOp",EDGE,"E0.sketch_text.stroke-365"),sQuery(id+"F0.wireOp",EDGE,"E0.sketch_text.stroke-366"),sQuery(id+"F0.wireOp",EDGE,"E0.sketch_text.stroke-367"),sQuery(id+"F0.wireOp",EDGE,"E0.sketch_text.stroke-368"),sQuery(id+"F0.wireOp",EDGE,"E0.sketch_text.stroke-369"),sQuery(id+"F0.wireOp",EDGE,"E0.sketch_text.stroke-370"),sQuery(id+"F0.wireOp",EDGE,"E0.sketch_text.stroke-371"),sQuery(id+"F0.wireOp",EDGE,"E0.sketch_text.stroke-372")])]});
            var Q27;
            Q27=makeQuery(id+"F2.opExtrude","SWEPT_BODY",BODY,{"disambiguationData":[OSD([sQuery(id+"F0.wireOp",EDGE,"E0.sketch_text.stroke-373"),sQuery(id+"F0.wireOp",EDGE,"E0.sketch_text.stroke-374"),sQuery(id+"F0.wireOp",EDGE,"E0.sketch_text.stroke-375"),sQuery(id+"F0.wireOp",EDGE,"E0.sketch_text.stroke-376"),sQuery(id+"F0.wireOp",EDGE,"E0.sketch_text.stroke-377"),sQuery(id+"F0.wireOp",EDGE,"E0.sketch_text.stroke-378"),sQuery(id+"F0.wireOp",EDGE,"E0.sketch_text.stroke-379"),sQuery(id+"F0.wireOp",EDGE,"E0.sketch_text.stroke-380"),sQuery(id+"F0.wireOp",EDGE,"E0.sketch_text.stroke-381"),sQuery(id+"F0.wireOp",EDGE,"E0.sketch_text.stroke-382"),sQuery(id+"F0.wireOp",EDGE,"E0.sketch_text.stroke-383"),sQuery(id+"F0.wireOp",EDGE,"E0.sketch_text.stroke-384"),sQuery(id+"F0.wireOp",EDGE,"E0.sketch_text.stroke-385"),sQuery(id+"F0.wireOp",EDGE,"E0.sketch_text.stroke-386"),sQuery(id+"F0.wireOp",EDGE,"E0.sketch_text.stroke-387"),sQuery(id+"F0.wireOp",EDGE,"E0.sketch_text.stroke-388"),sQuery(id+"F0.wireOp",EDGE,"E0.sketch_text.stroke-389"),sQuery(id+"F0.wireOp",EDGE,"E0.sketch_text.stroke-390"),sQuery(id+"F0.wireOp",EDGE,"E0.sketch_text.stroke-391")])]});
            var Q28;
            Q28=makeQuery(id+"F2.opExtrude","SWEPT_BODY",BODY,{"disambiguationData":[OSD([sQuery(id+"F0.wireOp",EDGE,"E0.sketch_text.stroke-392"),sQuery(id+"F0.wireOp",EDGE,"E0.sketch_text.stroke-393"),sQuery(id+"F0.wireOp",EDGE,"E0.sketch_text.stroke-394"),sQuery(id+"F0.wireOp",EDGE,"E0.sketch_text.stroke-395"),sQuery(id+"F0.wireOp",EDGE,"E0.sketch_text.stroke-396"),sQuery(id+"F0.wireOp",EDGE,"E0.sketch_text.stroke-397"),sQuery(id+"F0.wireOp",EDGE,"E0.sketch_text.stroke-398"),sQuery(id+"F0.wireOp",EDGE,"E0.sketch_text.stroke-399"),sQuery(id+"F0.wireOp",EDGE,"E0.sketch_text.stroke-400"),sQuery(id+"F0.wireOp",EDGE,"E0.sketch_text.stroke-401"),sQuery(id+"F0.wireOp",EDGE,"E0.sketch_text.stroke-402"),sQuery(id+"F0.wireOp",EDGE,"E0.sketch_text.stroke-403"),sQuery(id+"F0.wireOp",EDGE,"E0.sketch_text.stroke-404"),sQuery(id+"F0.wireOp",EDGE,"E0.sketch_text.stroke-405"),sQuery(id+"F0.wireOp",EDGE,"E0.sketch_text.stroke-406"),sQuery(id+"F0.wireOp",EDGE,"E0.sketch_text.stroke-407"),sQuery(id+"F0.wireOp",EDGE,"E0.sketch_text.stroke-408")])]});
            var Q29;
            Q29=makeQuery(id+"F2.opExtrude","SWEPT_BODY",BODY,{"disambiguationData":[OSD([sQuery(id+"F0.wireOp",EDGE,"E0.sketch_text.stroke-409"),sQuery(id+"F0.wireOp",EDGE,"E0.sketch_text.stroke-410"),sQuery(id+"F0.wireOp",EDGE,"E0.sketch_text.stroke-411"),sQuery(id+"F0.wireOp",EDGE,"E0.sketch_text.stroke-412"),sQuery(id+"F0.wireOp",EDGE,"E0.sketch_text.stroke-413"),sQuery(id+"F0.wireOp",EDGE,"E0.sketch_text.stroke-414"),sQuery(id+"F0.wireOp",EDGE,"E0.sketch_text.stroke-415"),sQuery(id+"F0.wireOp",EDGE,"E0.sketch_text.stroke-416"),sQuery(id+"F0.wireOp",EDGE,"E0.sketch_text.stroke-417"),sQuery(id+"F0.wireOp",EDGE,"E0.sketch_text.stroke-418"),sQuery(id+"F0.wireOp",EDGE,"E0.sketch_text.stroke-419"),sQuery(id+"F0.wireOp",EDGE,"E0.sketch_text.stroke-420"),sQuery(id+"F0.wireOp",EDGE,"E0.sketch_text.stroke-421"),sQuery(id+"F0.wireOp",EDGE,"E0.sketch_text.stroke-422"),sQuery(id+"F0.wireOp",EDGE,"E0.sketch_text.stroke-423"),sQuery(id+"F0.wireOp",EDGE,"E0.sketch_text.stroke-424"),sQuery(id+"F0.wireOp",EDGE,"E0.sketch_text.stroke-425")])]});
            var Q30;
            Q30=makeQuery(id+"F2.opExtrude","SWEPT_BODY",BODY,{"disambiguationData":[OSD([sQuery(id+"F0.wireOp",EDGE,"E0.sketch_text.stroke-426"),sQuery(id+"F0.wireOp",EDGE,"E0.sketch_text.stroke-427"),sQuery(id+"F0.wireOp",EDGE,"E0.sketch_text.stroke-428"),sQuery(id+"F0.wireOp",EDGE,"E0.sketch_text.stroke-429"),sQuery(id+"F0.wireOp",EDGE,"E0.sketch_text.stroke-430"),sQuery(id+"F0.wireOp",EDGE,"E0.sketch_text.stroke-431"),sQuery(id+"F0.wireOp",EDGE,"E0.sketch_text.stroke-432"),sQuery(id+"F0.wireOp",EDGE,"E0.sketch_text.stroke-433"),sQuery(id+"F0.wireOp",EDGE,"E0.sketch_text.stroke-434"),sQuery(id+"F0.wireOp",EDGE,"E0.sketch_text.stroke-435"),sQuery(id+"F0.wireOp",EDGE,"E0.sketch_text.stroke-436"),sQuery(id+"F0.wireOp",EDGE,"E0.sketch_text.stroke-437"),sQuery(id+"F0.wireOp",EDGE,"E0.sketch_text.stroke-438")])]});
            var Q31;
            Q31=makeQuery(id+"F2.opExtrude","SWEPT_BODY",BODY,{"disambiguationData":[OSD([sQuery(id+"F0.wireOp",EDGE,"E0.sketch_text.stroke-439"),sQuery(id+"F0.wireOp",EDGE,"E0.sketch_text.stroke-440"),sQuery(id+"F0.wireOp",EDGE,"E0.sketch_text.stroke-441"),sQuery(id+"F0.wireOp",EDGE,"E0.sketch_text.stroke-442"),sQuery(id+"F0.wireOp",EDGE,"E0.sketch_text.stroke-443"),sQuery(id+"F0.wireOp",EDGE,"E0.sketch_text.stroke-444"),sQuery(id+"F0.wireOp",EDGE,"E0.sketch_text.stroke-445"),sQuery(id+"F0.wireOp",EDGE,"E0.sketch_text.stroke-446"),sQuery(id+"F0.wireOp",EDGE,"E0.sketch_text.stroke-447"),sQuery(id+"F0.wireOp",EDGE,"E0.sketch_text.stroke-448"),sQuery(id+"F0.wireOp",EDGE,"E0.sketch_text.stroke-449"),sQuery(id+"F0.wireOp",EDGE,"E0.sketch_text.stroke-450"),sQuery(id+"F0.wireOp",EDGE,"E0.sketch_text.stroke-451")])]});
            var Q32;
            Q32=makeQuery(id+"F2.opExtrude","SWEPT_BODY",BODY,{"disambiguationData":[OSD([sQuery(id+"F0.wireOp",EDGE,"E0.sketch_text.stroke-452"),sQuery(id+"F0.wireOp",EDGE,"E0.sketch_text.stroke-453"),sQuery(id+"F0.wireOp",EDGE,"E0.sketch_text.stroke-454"),sQuery(id+"F0.wireOp",EDGE,"E0.sketch_text.stroke-455"),sQuery(id+"F0.wireOp",EDGE,"E0.sketch_text.stroke-456"),sQuery(id+"F0.wireOp",EDGE,"E0.sketch_text.stroke-457"),sQuery(id+"F0.wireOp",EDGE,"E0.sketch_text.stroke-458"),sQuery(id+"F0.wireOp",EDGE,"E0.sketch_text.stroke-459"),sQuery(id+"F0.wireOp",EDGE,"E0.sketch_text.stroke-460"),sQuery(id+"F0.wireOp",EDGE,"E0.sketch_text.stroke-461"),sQuery(id+"F0.wireOp",EDGE,"E0.sketch_text.stroke-462"),sQuery(id+"F0.wireOp",EDGE,"E0.sketch_text.stroke-463"),sQuery(id+"F0.wireOp",EDGE,"E0.sketch_text.stroke-464"),sQuery(id+"F0.wireOp",EDGE,"E0.sketch_text.stroke-465"),sQuery(id+"F0.wireOp",EDGE,"E0.sketch_text.stroke-466"),sQuery(id+"F0.wireOp",EDGE,"E0.sketch_text.stroke-467"),sQuery(id+"F0.wireOp",EDGE,"E0.sketch_text.stroke-468")])]});
            var Q33;
            Q33=makeQuery(id+"F2.opExtrude","SWEPT_BODY",BODY,{"disambiguationData":[OSD([sQuery(id+"F0.wireOp",EDGE,"E0.sketch_text.stroke-469"),sQuery(id+"F0.wireOp",EDGE,"E0.sketch_text.stroke-470"),sQuery(id+"F0.wireOp",EDGE,"E0.sketch_text.stroke-471"),sQuery(id+"F0.wireOp",EDGE,"E0.sketch_text.stroke-472"),sQuery(id+"F0.wireOp",EDGE,"E0.sketch_text.stroke-473"),sQuery(id+"F0.wireOp",EDGE,"E0.sketch_text.stroke-474"),sQuery(id+"F0.wireOp",EDGE,"E0.sketch_text.stroke-475"),sQuery(id+"F0.wireOp",EDGE,"E0.sketch_text.stroke-476"),sQuery(id+"F0.wireOp",EDGE,"E0.sketch_text.stroke-477"),sQuery(id+"F0.wireOp",EDGE,"E0.sketch_text.stroke-478"),sQuery(id+"F0.wireOp",EDGE,"E0.sketch_text.stroke-479"),sQuery(id+"F0.wireOp",EDGE,"E0.sketch_text.stroke-480"),sQuery(id+"F0.wireOp",EDGE,"E0.sketch_text.stroke-481"),sQuery(id+"F0.wireOp",EDGE,"E0.sketch_text.stroke-482"),sQuery(id+"F0.wireOp",EDGE,"E0.sketch_text.stroke-483"),sQuery(id+"F0.wireOp",EDGE,"E0.sketch_text.stroke-484"),sQuery(id+"F0.wireOp",EDGE,"E0.sketch_text.stroke-485"),sQuery(id+"F0.wireOp",EDGE,"E0.sketch_text.stroke-486"),sQuery(id+"F0.wireOp",EDGE,"E0.sketch_text.stroke-487")])]});
            var Q34;
            Q34=makeQuery(id+"F2.opExtrude","SWEPT_BODY",BODY,{"disambiguationData":[OSD([sQuery(id+"F0.wireOp",EDGE,"E0.sketch_text.stroke-488"),sQuery(id+"F0.wireOp",EDGE,"E0.sketch_text.stroke-489"),sQuery(id+"F0.wireOp",EDGE,"E0.sketch_text.stroke-490"),sQuery(id+"F0.wireOp",EDGE,"E0.sketch_text.stroke-491"),sQuery(id+"F0.wireOp",EDGE,"E0.sketch_text.stroke-492"),sQuery(id+"F0.wireOp",EDGE,"E0.sketch_text.stroke-493"),sQuery(id+"F0.wireOp",EDGE,"E0.sketch_text.stroke-494"),sQuery(id+"F0.wireOp",EDGE,"E0.sketch_text.stroke-495"),sQuery(id+"F0.wireOp",EDGE,"E0.sketch_text.stroke-496"),sQuery(id+"F0.wireOp",EDGE,"E0.sketch_text.stroke-497"),sQuery(id+"F0.wireOp",EDGE,"E0.sketch_text.stroke-498"),sQuery(id+"F0.wireOp",EDGE,"E0.sketch_text.stroke-499"),sQuery(id+"F0.wireOp",EDGE,"E0.sketch_text.stroke-500"),sQuery(id+"F0.wireOp",EDGE,"E0.sketch_text.stroke-501"),sQuery(id+"F0.wireOp",EDGE,"E0.sketch_text.stroke-502"),sQuery(id+"F0.wireOp",EDGE,"E0.sketch_text.stroke-503"),sQuery(id+"F0.wireOp",EDGE,"E0.sketch_text.stroke-504"),sQuery(id+"F0.wireOp",EDGE,"E0.sketch_text.stroke-505"),sQuery(id+"F0.wireOp",EDGE,"E0.sketch_text.stroke-506")])]});
            var Q35;
            Q35=makeQuery(id+"F2.opExtrude","SWEPT_BODY",BODY,{"disambiguationData":[OSD([sQuery(id+"F0.wireOp",EDGE,"E0.sketch_text.stroke-507"),sQuery(id+"F0.wireOp",EDGE,"E0.sketch_text.stroke-508"),sQuery(id+"F0.wireOp",EDGE,"E0.sketch_text.stroke-509"),sQuery(id+"F0.wireOp",EDGE,"E0.sketch_text.stroke-510"),sQuery(id+"F0.wireOp",EDGE,"E0.sketch_text.stroke-511"),sQuery(id+"F0.wireOp",EDGE,"E0.sketch_text.stroke-512"),sQuery(id+"F0.wireOp",EDGE,"E0.sketch_text.stroke-513"),sQuery(id+"F0.wireOp",EDGE,"E0.sketch_text.stroke-514"),sQuery(id+"F0.wireOp",EDGE,"E0.sketch_text.stroke-515"),sQuery(id+"F0.wireOp",EDGE,"E0.sketch_text.stroke-516"),sQuery(id+"F0.wireOp",EDGE,"E0.sketch_text.stroke-517"),sQuery(id+"F0.wireOp",EDGE,"E0.sketch_text.stroke-518"),sQuery(id+"F0.wireOp",EDGE,"E0.sketch_text.stroke-519")])]});
            var Q36;
            Q36=makeQuery(id+"F2.opExtrude","SWEPT_BODY",BODY,{"disambiguationData":[OSD([sQuery(id+"F0.wireOp",EDGE,"E0.sketch_text.stroke-520"),sQuery(id+"F0.wireOp",EDGE,"E0.sketch_text.stroke-521"),sQuery(id+"F0.wireOp",EDGE,"E0.sketch_text.stroke-522"),sQuery(id+"F0.wireOp",EDGE,"E0.sketch_text.stroke-523"),sQuery(id+"F0.wireOp",EDGE,"E0.sketch_text.stroke-524"),sQuery(id+"F0.wireOp",EDGE,"E0.sketch_text.stroke-525"),sQuery(id+"F0.wireOp",EDGE,"E0.sketch_text.stroke-526"),sQuery(id+"F0.wireOp",EDGE,"E0.sketch_text.stroke-527"),sQuery(id+"F0.wireOp",EDGE,"E0.sketch_text.stroke-528"),sQuery(id+"F0.wireOp",EDGE,"E0.sketch_text.stroke-529"),sQuery(id+"F0.wireOp",EDGE,"E0.sketch_text.stroke-530"),sQuery(id+"F0.wireOp",EDGE,"E0.sketch_text.stroke-531"),sQuery(id+"F0.wireOp",EDGE,"E0.sketch_text.stroke-532"),sQuery(id+"F0.wireOp",EDGE,"E0.sketch_text.stroke-533"),sQuery(id+"F0.wireOp",EDGE,"E0.sketch_text.stroke-534"),sQuery(id+"F0.wireOp",EDGE,"E0.sketch_text.stroke-535"),sQuery(id+"F0.wireOp",EDGE,"E0.sketch_text.stroke-536"),sQuery(id+"F0.wireOp",EDGE,"E0.sketch_text.stroke-537"),sQuery(id+"F0.wireOp",EDGE,"E0.sketch_text.stroke-538"),sQuery(id+"F0.wireOp",EDGE,"E0.sketch_text.stroke-539"),sQuery(id+"F0.wireOp",EDGE,"E0.sketch_text.stroke-540"),sQuery(id+"F0.wireOp",EDGE,"E0.sketch_text.stroke-541"),sQuery(id+"F0.wireOp",EDGE,"E0.sketch_text.stroke-542"),sQuery(id+"F0.wireOp",EDGE,"E0.sketch_text.stroke-543"),sQuery(id+"F0.wireOp",EDGE,"E0.sketch_text.stroke-544"),sQuery(id+"F0.wireOp",EDGE,"E0.sketch_text.stroke-545"),sQuery(id+"F0.wireOp",EDGE,"E0.sketch_text.stroke-546"),sQuery(id+"F0.wireOp",EDGE,"E0.sketch_text.stroke-547"),sQuery(id+"F0.wireOp",EDGE,"E0.sketch_text.stroke-548"),sQuery(id+"F0.wireOp",EDGE,"E0.sketch_text.stroke-549"),sQuery(id+"F0.wireOp",EDGE,"E0.sketch_text.stroke-550")])]});
            var Q37;
            Q37=makeQuery(id+"F2.opExtrude","SWEPT_BODY",BODY,{"disambiguationData":[OSD([sQuery(id+"F0.wireOp",EDGE,"E0.sketch_text.stroke-551"),sQuery(id+"F0.wireOp",EDGE,"E0.sketch_text.stroke-552"),sQuery(id+"F0.wireOp",EDGE,"E0.sketch_text.stroke-553"),sQuery(id+"F0.wireOp",EDGE,"E0.sketch_text.stroke-554"),sQuery(id+"F0.wireOp",EDGE,"E0.sketch_text.stroke-555"),sQuery(id+"F0.wireOp",EDGE,"E0.sketch_text.stroke-556"),sQuery(id+"F0.wireOp",EDGE,"E0.sketch_text.stroke-557"),sQuery(id+"F0.wireOp",EDGE,"E0.sketch_text.stroke-558"),sQuery(id+"F0.wireOp",EDGE,"E0.sketch_text.stroke-559"),sQuery(id+"F0.wireOp",EDGE,"E0.sketch_text.stroke-560"),sQuery(id+"F0.wireOp",EDGE,"E0.sketch_text.stroke-561"),sQuery(id+"F0.wireOp",EDGE,"E0.sketch_text.stroke-562"),sQuery(id+"F0.wireOp",EDGE,"E0.sketch_text.stroke-563"),sQuery(id+"F0.wireOp",EDGE,"E0.sketch_text.stroke-564"),sQuery(id+"F0.wireOp",EDGE,"E0.sketch_text.stroke-565"),sQuery(id+"F0.wireOp",EDGE,"E0.sketch_text.stroke-566"),sQuery(id+"F0.wireOp",EDGE,"E0.sketch_text.stroke-567"),sQuery(id+"F0.wireOp",EDGE,"E0.sketch_text.stroke-568"),sQuery(id+"F0.wireOp",EDGE,"E0.sketch_text.stroke-569"),sQuery(id+"F0.wireOp",EDGE,"E0.sketch_text.stroke-570"),sQuery(id+"F0.wireOp",EDGE,"E0.sketch_text.stroke-571"),sQuery(id+"F0.wireOp",EDGE,"E0.sketch_text.stroke-572"),sQuery(id+"F0.wireOp",EDGE,"E0.sketch_text.stroke-573")])]});
            var Q38;
            Q38=makeQuery(id+"F2.opExtrude","SWEPT_BODY",BODY,{"disambiguationData":[OSD([sQuery(id+"F0.wireOp",EDGE,"E0.sketch_text.stroke-574"),sQuery(id+"F0.wireOp",EDGE,"E0.sketch_text.stroke-575"),sQuery(id+"F0.wireOp",EDGE,"E0.sketch_text.stroke-576"),sQuery(id+"F0.wireOp",EDGE,"E0.sketch_text.stroke-577"),sQuery(id+"F0.wireOp",EDGE,"E0.sketch_text.stroke-578"),sQuery(id+"F0.wireOp",EDGE,"E0.sketch_text.stroke-579"),sQuery(id+"F0.wireOp",EDGE,"E0.sketch_text.stroke-580"),sQuery(id+"F0.wireOp",EDGE,"E0.sketch_text.stroke-581"),sQuery(id+"F0.wireOp",EDGE,"E0.sketch_text.stroke-582"),sQuery(id+"F0.wireOp",EDGE,"E0.sketch_text.stroke-583"),sQuery(id+"F0.wireOp",EDGE,"E0.sketch_text.stroke-584"),sQuery(id+"F0.wireOp",EDGE,"E0.sketch_text.stroke-585"),sQuery(id+"F0.wireOp",EDGE,"E0.sketch_text.stroke-586"),sQuery(id+"F0.wireOp",EDGE,"E0.sketch_text.stroke-587"),sQuery(id+"F0.wireOp",EDGE,"E0.sketch_text.stroke-588"),sQuery(id+"F0.wireOp",EDGE,"E0.sketch_text.stroke-589")])]});
            var Q39;
            Q39=makeQuery(id+"F2.opExtrude","SWEPT_BODY",BODY,{"disambiguationData":[OSD([sQuery(id+"F0.wireOp",EDGE,"E0.sketch_text.stroke-590"),sQuery(id+"F0.wireOp",EDGE,"E0.sketch_text.stroke-591"),sQuery(id+"F0.wireOp",EDGE,"E0.sketch_text.stroke-592"),sQuery(id+"F0.wireOp",EDGE,"E0.sketch_text.stroke-593"),sQuery(id+"F0.wireOp",EDGE,"E0.sketch_text.stroke-594"),sQuery(id+"F0.wireOp",EDGE,"E0.sketch_text.stroke-595"),sQuery(id+"F0.wireOp",EDGE,"E0.sketch_text.stroke-596"),sQuery(id+"F0.wireOp",EDGE,"E0.sketch_text.stroke-597"),sQuery(id+"F0.wireOp",EDGE,"E0.sketch_text.stroke-598"),sQuery(id+"F0.wireOp",EDGE,"E0.sketch_text.stroke-599"),sQuery(id+"F0.wireOp",EDGE,"E0.sketch_text.stroke-600"),sQuery(id+"F0.wireOp",EDGE,"E0.sketch_text.stroke-601"),sQuery(id+"F0.wireOp",EDGE,"E0.sketch_text.stroke-602"),sQuery(id+"F0.wireOp",EDGE,"E0.sketch_text.stroke-603"),sQuery(id+"F0.wireOp",EDGE,"E0.sketch_text.stroke-604")])]});
            var Q40;
            Q40=makeQuery(id+"F2.opExtrude","SWEPT_BODY",BODY,{"disambiguationData":[OSD([sQuery(id+"F0.wireOp",EDGE,"E0.sketch_text.stroke-605"),sQuery(id+"F0.wireOp",EDGE,"E0.sketch_text.stroke-606"),sQuery(id+"F0.wireOp",EDGE,"E0.sketch_text.stroke-607"),sQuery(id+"F0.wireOp",EDGE,"E0.sketch_text.stroke-608"),sQuery(id+"F0.wireOp",EDGE,"E0.sketch_text.stroke-609"),sQuery(id+"F0.wireOp",EDGE,"E0.sketch_text.stroke-610"),sQuery(id+"F0.wireOp",EDGE,"E0.sketch_text.stroke-611"),sQuery(id+"F0.wireOp",EDGE,"E0.sketch_text.stroke-612"),sQuery(id+"F0.wireOp",EDGE,"E0.sketch_text.stroke-613"),sQuery(id+"F0.wireOp",EDGE,"E0.sketch_text.stroke-614"),sQuery(id+"F0.wireOp",EDGE,"E0.sketch_text.stroke-615"),sQuery(id+"F0.wireOp",EDGE,"E0.sketch_text.stroke-616"),sQuery(id+"F0.wireOp",EDGE,"E0.sketch_text.stroke-617"),sQuery(id+"F0.wireOp",EDGE,"E0.sketch_text.stroke-618"),sQuery(id+"F0.wireOp",EDGE,"E0.sketch_text.stroke-619"),sQuery(id+"F0.wireOp",EDGE,"E0.sketch_text.stroke-620"),sQuery(id+"F0.wireOp",EDGE,"E0.sketch_text.stroke-621"),sQuery(id+"F0.wireOp",EDGE,"E0.sketch_text.stroke-622"),sQuery(id+"F0.wireOp",EDGE,"E0.sketch_text.stroke-623"),sQuery(id+"F0.wireOp",EDGE,"E0.sketch_text.stroke-624"),sQuery(id+"F0.wireOp",EDGE,"E0.sketch_text.stroke-625"),sQuery(id+"F0.wireOp",EDGE,"E0.sketch_text.stroke-626"),sQuery(id+"F0.wireOp",EDGE,"E0.sketch_text.stroke-627"),sQuery(id+"F0.wireOp",EDGE,"E0.sketch_text.stroke-628"),sQuery(id+"F0.wireOp",EDGE,"E0.sketch_text.stroke-629"),sQuery(id+"F0.wireOp",EDGE,"E0.sketch_text.stroke-630"),sQuery(id+"F0.wireOp",EDGE,"E0.sketch_text.stroke-631")])]});
            var Q41;
            Q41=makeQuery(id+"F2.opExtrude","SWEPT_BODY",BODY,{"disambiguationData":[OSD([sQuery(id+"F0.wireOp",EDGE,"E0.sketch_text.stroke-760"),sQuery(id+"F0.wireOp",EDGE,"E0.sketch_text.stroke-761"),sQuery(id+"F0.wireOp",EDGE,"E0.sketch_text.stroke-762"),sQuery(id+"F0.wireOp",EDGE,"E0.sketch_text.stroke-763"),sQuery(id+"F0.wireOp",EDGE,"E0.sketch_text.stroke-764"),sQuery(id+"F0.wireOp",EDGE,"E0.sketch_text.stroke-765"),sQuery(id+"F0.wireOp",EDGE,"E0.sketch_text.stroke-766"),sQuery(id+"F0.wireOp",EDGE,"E0.sketch_text.stroke-767")])]});
            var Q42;
            Q42=makeQuery(id+"F2.opExtrude","SWEPT_BODY",BODY,{"disambiguationData":[OSD([sQuery(id+"F0.wireOp",EDGE,"E0.sketch_text.stroke-768"),sQuery(id+"F0.wireOp",EDGE,"E0.sketch_text.stroke-769"),sQuery(id+"F0.wireOp",EDGE,"E0.sketch_text.stroke-770"),sQuery(id+"F0.wireOp",EDGE,"E0.sketch_text.stroke-771"),sQuery(id+"F0.wireOp",EDGE,"E0.sketch_text.stroke-772"),sQuery(id+"F0.wireOp",EDGE,"E0.sketch_text.stroke-773"),sQuery(id+"F0.wireOp",EDGE,"E0.sketch_text.stroke-774"),sQuery(id+"F0.wireOp",EDGE,"E0.sketch_text.stroke-775"),sQuery(id+"F0.wireOp",EDGE,"E0.sketch_text.stroke-776"),sQuery(id+"F0.wireOp",EDGE,"E0.sketch_text.stroke-777"),sQuery(id+"F0.wireOp",EDGE,"E0.sketch_text.stroke-778"),sQuery(id+"F0.wireOp",EDGE,"E0.sketch_text.stroke-779"),sQuery(id+"F0.wireOp",EDGE,"E0.sketch_text.stroke-780"),sQuery(id+"F0.wireOp",EDGE,"E0.sketch_text.stroke-781"),sQuery(id+"F0.wireOp",EDGE,"E0.sketch_text.stroke-782"),sQuery(id+"F0.wireOp",EDGE,"E0.sketch_text.stroke-783"),sQuery(id+"F0.wireOp",EDGE,"E0.sketch_text.stroke-784"),sQuery(id+"F0.wireOp",EDGE,"E0.sketch_text.stroke-785"),sQuery(id+"F0.wireOp",EDGE,"E0.sketch_text.stroke-786"),sQuery(id+"F0.wireOp",EDGE,"E0.sketch_text.stroke-787"),sQuery(id+"F0.wireOp",EDGE,"E0.sketch_text.stroke-788"),sQuery(id+"F0.wireOp",EDGE,"E0.sketch_text.stroke-789"),sQuery(id+"F0.wireOp",EDGE,"E0.sketch_text.stroke-790"),sQuery(id+"F0.wireOp",EDGE,"E0.sketch_text.stroke-791"),sQuery(id+"F0.wireOp",EDGE,"E0.sketch_text.stroke-792"),sQuery(id+"F0.wireOp",EDGE,"E0.sketch_text.stroke-793"),sQuery(id+"F0.wireOp",EDGE,"E0.sketch_text.stroke-794")])]});
            var Q43;
            Q43=makeQuery(id+"F2.opExtrude","SWEPT_BODY",BODY,{"disambiguationData":[OSD([sQuery(id+"F0.wireOp",EDGE,"E0.sketch_text.stroke-795"),sQuery(id+"F0.wireOp",EDGE,"E0.sketch_text.stroke-796"),sQuery(id+"F0.wireOp",EDGE,"E0.sketch_text.stroke-797"),sQuery(id+"F0.wireOp",EDGE,"E0.sketch_text.stroke-798"),sQuery(id+"F0.wireOp",EDGE,"E0.sketch_text.stroke-799"),sQuery(id+"F0.wireOp",EDGE,"E0.sketch_text.stroke-800"),sQuery(id+"F0.wireOp",EDGE,"E0.sketch_text.stroke-801"),sQuery(id+"F0.wireOp",EDGE,"E0.sketch_text.stroke-802"),sQuery(id+"F0.wireOp",EDGE,"E0.sketch_text.stroke-803"),sQuery(id+"F0.wireOp",EDGE,"E0.sketch_text.stroke-804"),sQuery(id+"F0.wireOp",EDGE,"E0.sketch_text.stroke-805"),sQuery(id+"F0.wireOp",EDGE,"E0.sketch_text.stroke-806"),sQuery(id+"F0.wireOp",EDGE,"E0.sketch_text.stroke-807"),sQuery(id+"F0.wireOp",EDGE,"E0.sketch_text.stroke-808"),sQuery(id+"F0.wireOp",EDGE,"E0.sketch_text.stroke-809"),sQuery(id+"F0.wireOp",EDGE,"E0.sketch_text.stroke-810"),sQuery(id+"F0.wireOp",EDGE,"E0.sketch_text.stroke-811")])]});
            var Q44;
            Q44=makeQuery(id+"F2.opExtrude","SWEPT_BODY",BODY,{"disambiguationData":[OSD([sQuery(id+"F0.wireOp",EDGE,"E0.sketch_text.stroke-812"),sQuery(id+"F0.wireOp",EDGE,"E0.sketch_text.stroke-813"),sQuery(id+"F0.wireOp",EDGE,"E0.sketch_text.stroke-814"),sQuery(id+"F0.wireOp",EDGE,"E0.sketch_text.stroke-815"),sQuery(id+"F0.wireOp",EDGE,"E0.sketch_text.stroke-816"),sQuery(id+"F0.wireOp",EDGE,"E0.sketch_text.stroke-817"),sQuery(id+"F0.wireOp",EDGE,"E0.sketch_text.stroke-818"),sQuery(id+"F0.wireOp",EDGE,"E0.sketch_text.stroke-819"),sQuery(id+"F0.wireOp",EDGE,"E0.sketch_text.stroke-820"),sQuery(id+"F0.wireOp",EDGE,"E0.sketch_text.stroke-821"),sQuery(id+"F0.wireOp",EDGE,"E0.sketch_text.stroke-822"),sQuery(id+"F0.wireOp",EDGE,"E0.sketch_text.stroke-823"),sQuery(id+"F0.wireOp",EDGE,"E0.sketch_text.stroke-824"),sQuery(id+"F0.wireOp",EDGE,"E0.sketch_text.stroke-825"),sQuery(id+"F0.wireOp",EDGE,"E0.sketch_text.stroke-826"),sQuery(id+"F0.wireOp",EDGE,"E0.sketch_text.stroke-827"),sQuery(id+"F0.wireOp",EDGE,"E0.sketch_text.stroke-828"),sQuery(id+"F0.wireOp",EDGE,"E0.sketch_text.stroke-829"),sQuery(id+"F0.wireOp",EDGE,"E0.sketch_text.stroke-830"),sQuery(id+"F0.wireOp",EDGE,"E0.sketch_text.stroke-831"),sQuery(id+"F0.wireOp",EDGE,"E0.sketch_text.stroke-832"),sQuery(id+"F0.wireOp",EDGE,"E0.sketch_text.stroke-833"),sQuery(id+"F0.wireOp",EDGE,"E0.sketch_text.stroke-834"),sQuery(id+"F0.wireOp",EDGE,"E0.sketch_text.stroke-835")])]});
            var Q45;
            Q45=makeQuery(id+"F2.opExtrude","SWEPT_BODY",BODY,{"disambiguationData":[OSD([sQuery(id+"F0.wireOp",EDGE,"E0.sketch_text.stroke-836"),sQuery(id+"F0.wireOp",EDGE,"E0.sketch_text.stroke-837"),sQuery(id+"F0.wireOp",EDGE,"E0.sketch_text.stroke-838"),sQuery(id+"F0.wireOp",EDGE,"E0.sketch_text.stroke-839"),sQuery(id+"F0.wireOp",EDGE,"E0.sketch_text.stroke-840"),sQuery(id+"F0.wireOp",EDGE,"E0.sketch_text.stroke-841"),sQuery(id+"F0.wireOp",EDGE,"E0.sketch_text.stroke-842"),sQuery(id+"F0.wireOp",EDGE,"E0.sketch_text.stroke-843")])]});
            var Q46;
            Q46=makeQuery(id+"F2.opExtrude","SWEPT_BODY",BODY,{"disambiguationData":[OSD([sQuery(id+"F0.wireOp",EDGE,"E0.sketch_text.stroke-844"),sQuery(id+"F0.wireOp",EDGE,"E0.sketch_text.stroke-845"),sQuery(id+"F0.wireOp",EDGE,"E0.sketch_text.stroke-846"),sQuery(id+"F0.wireOp",EDGE,"E0.sketch_text.stroke-847"),sQuery(id+"F0.wireOp",EDGE,"E0.sketch_text.stroke-848"),sQuery(id+"F0.wireOp",EDGE,"E0.sketch_text.stroke-849"),sQuery(id+"F0.wireOp",EDGE,"E0.sketch_text.stroke-850"),sQuery(id+"F0.wireOp",EDGE,"E0.sketch_text.stroke-851"),sQuery(id+"F0.wireOp",EDGE,"E0.sketch_text.stroke-852"),sQuery(id+"F0.wireOp",EDGE,"E0.sketch_text.stroke-853"),sQuery(id+"F0.wireOp",EDGE,"E0.sketch_text.stroke-854"),sQuery(id+"F0.wireOp",EDGE,"E0.sketch_text.stroke-855"),sQuery(id+"F0.wireOp",EDGE,"E0.sketch_text.stroke-856"),sQuery(id+"F0.wireOp",EDGE,"E0.sketch_text.stroke-857"),sQuery(id+"F0.wireOp",EDGE,"E0.sketch_text.stroke-858"),sQuery(id+"F0.wireOp",EDGE,"E0.sketch_text.stroke-859"),sQuery(id+"F0.wireOp",EDGE,"E0.sketch_text.stroke-860")])]});
            var Q47;
            Q47=makeQuery(id+"F2.opExtrude","SWEPT_BODY",BODY,{"disambiguationData":[OSD([sQuery(id+"F0.wireOp",EDGE,"E0.sketch_text.stroke-861"),sQuery(id+"F0.wireOp",EDGE,"E0.sketch_text.stroke-862"),sQuery(id+"F0.wireOp",EDGE,"E0.sketch_text.stroke-863"),sQuery(id+"F0.wireOp",EDGE,"E0.sketch_text.stroke-864"),sQuery(id+"F0.wireOp",EDGE,"E0.sketch_text.stroke-865"),sQuery(id+"F0.wireOp",EDGE,"E0.sketch_text.stroke-866"),sQuery(id+"F0.wireOp",EDGE,"E0.sketch_text.stroke-867"),sQuery(id+"F0.wireOp",EDGE,"E0.sketch_text.stroke-868"),sQuery(id+"F0.wireOp",EDGE,"E0.sketch_text.stroke-869"),sQuery(id+"F0.wireOp",EDGE,"E0.sketch_text.stroke-870"),sQuery(id+"F0.wireOp",EDGE,"E0.sketch_text.stroke-871"),sQuery(id+"F0.wireOp",EDGE,"E0.sketch_text.stroke-872"),sQuery(id+"F0.wireOp",EDGE,"E0.sketch_text.stroke-873"),sQuery(id+"F0.wireOp",EDGE,"E0.sketch_text.stroke-874"),sQuery(id+"F0.wireOp",EDGE,"E0.sketch_text.stroke-875"),sQuery(id+"F0.wireOp",EDGE,"E0.sketch_text.stroke-876"),sQuery(id+"F0.wireOp",EDGE,"E0.sketch_text.stroke-877"),sQuery(id+"F0.wireOp",EDGE,"E0.sketch_text.stroke-878"),sQuery(id+"F0.wireOp",EDGE,"E0.sketch_text.stroke-879"),sQuery(id+"F0.wireOp",EDGE,"E0.sketch_text.stroke-880"),sQuery(id+"F0.wireOp",EDGE,"E0.sketch_text.stroke-881"),sQuery(id+"F0.wireOp",EDGE,"E0.sketch_text.stroke-882"),sQuery(id+"F0.wireOp",EDGE,"E0.sketch_text.stroke-883"),sQuery(id+"F0.wireOp",EDGE,"E0.sketch_text.stroke-884"),sQuery(id+"F0.wireOp",EDGE,"E0.sketch_text.stroke-885"),sQuery(id+"F0.wireOp",EDGE,"E0.sketch_text.stroke-886"),sQuery(id+"F0.wireOp",EDGE,"E0.sketch_text.stroke-887"),sQuery(id+"F0.wireOp",EDGE,"E0.sketch_text.stroke-888")])]});
            var Q48;
            Q48=makeQuery(id+"F2.opExtrude","SWEPT_BODY",BODY,{"disambiguationData":[OSD([sQuery(id+"F0.wireOp",EDGE,"E0.sketch_text.stroke-889"),sQuery(id+"F0.wireOp",EDGE,"E0.sketch_text.stroke-890"),sQuery(id+"F0.wireOp",EDGE,"E0.sketch_text.stroke-891"),sQuery(id+"F0.wireOp",EDGE,"E0.sketch_text.stroke-892"),sQuery(id+"F0.wireOp",EDGE,"E0.sketch_text.stroke-893"),sQuery(id+"F0.wireOp",EDGE,"E0.sketch_text.stroke-894"),sQuery(id+"F0.wireOp",EDGE,"E0.sketch_text.stroke-895"),sQuery(id+"F0.wireOp",EDGE,"E0.sketch_text.stroke-896"),sQuery(id+"F0.wireOp",EDGE,"E0.sketch_text.stroke-897"),sQuery(id+"F0.wireOp",EDGE,"E0.sketch_text.stroke-898"),sQuery(id+"F0.wireOp",EDGE,"E0.sketch_text.stroke-899"),sQuery(id+"F0.wireOp",EDGE,"E0.sketch_text.stroke-900"),sQuery(id+"F0.wireOp",EDGE,"E0.sketch_text.stroke-901"),sQuery(id+"F0.wireOp",EDGE,"E0.sketch_text.stroke-902"),sQuery(id+"F0.wireOp",EDGE,"E0.sketch_text.stroke-903"),sQuery(id+"F0.wireOp",EDGE,"E0.sketch_text.stroke-904"),sQuery(id+"F0.wireOp",EDGE,"E0.sketch_text.stroke-905"),sQuery(id+"F0.wireOp",EDGE,"E0.sketch_text.stroke-906"),sQuery(id+"F0.wireOp",EDGE,"E0.sketch_text.stroke-907"),sQuery(id+"F0.wireOp",EDGE,"E0.sketch_text.stroke-908"),sQuery(id+"F0.wireOp",EDGE,"E0.sketch_text.stroke-909"),sQuery(id+"F0.wireOp",EDGE,"E0.sketch_text.stroke-910"),sQuery(id+"F0.wireOp",EDGE,"E0.sketch_text.stroke-911"),sQuery(id+"F0.wireOp",EDGE,"E0.sketch_text.stroke-912"),sQuery(id+"F0.wireOp",EDGE,"E0.sketch_text.stroke-913"),sQuery(id+"F0.wireOp",EDGE,"E0.sketch_text.stroke-914"),sQuery(id+"F0.wireOp",EDGE,"E0.sketch_text.stroke-915"),sQuery(id+"F0.wireOp",EDGE,"E0.sketch_text.stroke-916")])]});
            var Q49;
            Q49=makeQuery(id+"F2.opExtrude","SWEPT_BODY",BODY,{"disambiguationData":[OSD([sQuery(id+"F0.wireOp",EDGE,"E0.sketch_text.stroke-917"),sQuery(id+"F0.wireOp",EDGE,"E0.sketch_text.stroke-918"),sQuery(id+"F0.wireOp",EDGE,"E0.sketch_text.stroke-919"),sQuery(id+"F0.wireOp",EDGE,"E0.sketch_text.stroke-920"),sQuery(id+"F0.wireOp",EDGE,"E0.sketch_text.stroke-921"),sQuery(id+"F0.wireOp",EDGE,"E0.sketch_text.stroke-922"),sQuery(id+"F0.wireOp",EDGE,"E0.sketch_text.stroke-923"),sQuery(id+"F0.wireOp",EDGE,"E0.sketch_text.stroke-924"),sQuery(id+"F0.wireOp",EDGE,"E0.sketch_text.stroke-925"),sQuery(id+"F0.wireOp",EDGE,"E0.sketch_text.stroke-926"),sQuery(id+"F0.wireOp",EDGE,"E0.sketch_text.stroke-927"),sQuery(id+"F0.wireOp",EDGE,"E0.sketch_text.stroke-928"),sQuery(id+"F0.wireOp",EDGE,"E0.sketch_text.stroke-929"),sQuery(id+"F0.wireOp",EDGE,"E0.sketch_text.stroke-930"),sQuery(id+"F0.wireOp",EDGE,"E0.sketch_text.stroke-931"),sQuery(id+"F0.wireOp",EDGE,"E0.sketch_text.stroke-932"),sQuery(id+"F0.wireOp",EDGE,"E0.sketch_text.stroke-933"),sQuery(id+"F0.wireOp",EDGE,"E0.sketch_text.stroke-934"),sQuery(id+"F0.wireOp",EDGE,"E0.sketch_text.stroke-935"),sQuery(id+"F0.wireOp",EDGE,"E0.sketch_text.stroke-936"),sQuery(id+"F0.wireOp",EDGE,"E0.sketch_text.stroke-937"),sQuery(id+"F0.wireOp",EDGE,"E0.sketch_text.stroke-938"),sQuery(id+"F0.wireOp",EDGE,"E0.sketch_text.stroke-939"),sQuery(id+"F0.wireOp",EDGE,"E0.sketch_text.stroke-940"),sQuery(id+"F0.wireOp",EDGE,"E0.sketch_text.stroke-941"),sQuery(id+"F0.wireOp",EDGE,"E0.sketch_text.stroke-942"),sQuery(id+"F0.wireOp",EDGE,"E0.sketch_text.stroke-943")])]});
            var Q50;
            Q50=makeQuery(id+"F2.opExtrude","SWEPT_BODY",BODY,{"disambiguationData":[OSD([sQuery(id+"F0.wireOp",EDGE,"E0.sketch_text.stroke-944"),sQuery(id+"F0.wireOp",EDGE,"E0.sketch_text.stroke-945"),sQuery(id+"F0.wireOp",EDGE,"E0.sketch_text.stroke-946"),sQuery(id+"F0.wireOp",EDGE,"E0.sketch_text.stroke-947"),sQuery(id+"F0.wireOp",EDGE,"E0.sketch_text.stroke-948"),sQuery(id+"F0.wireOp",EDGE,"E0.sketch_text.stroke-949"),sQuery(id+"F0.wireOp",EDGE,"E0.sketch_text.stroke-950"),sQuery(id+"F0.wireOp",EDGE,"E0.sketch_text.stroke-951"),sQuery(id+"F0.wireOp",EDGE,"E0.sketch_text.stroke-952"),sQuery(id+"F0.wireOp",EDGE,"E0.sketch_text.stroke-953"),sQuery(id+"F0.wireOp",EDGE,"E0.sketch_text.stroke-954"),sQuery(id+"F0.wireOp",EDGE,"E0.sketch_text.stroke-955"),sQuery(id+"F0.wireOp",EDGE,"E0.sketch_text.stroke-956"),sQuery(id+"F0.wireOp",EDGE,"E0.sketch_text.stroke-957"),sQuery(id+"F0.wireOp",EDGE,"E0.sketch_text.stroke-958"),sQuery(id+"F0.wireOp",EDGE,"E0.sketch_text.stroke-959"),sQuery(id+"F0.wireOp",EDGE,"E0.sketch_text.stroke-960"),sQuery(id+"F0.wireOp",EDGE,"E0.sketch_text.stroke-961"),sQuery(id+"F0.wireOp",EDGE,"E0.sketch_text.stroke-962"),sQuery(id+"F0.wireOp",EDGE,"E0.sketch_text.stroke-963"),sQuery(id+"F0.wireOp",EDGE,"E0.sketch_text.stroke-964"),sQuery(id+"F0.wireOp",EDGE,"E0.sketch_text.stroke-965"),sQuery(id+"F0.wireOp",EDGE,"E0.sketch_text.stroke-966"),sQuery(id+"F0.wireOp",EDGE,"E0.sketch_text.stroke-967"),sQuery(id+"F0.wireOp",EDGE,"E0.sketch_text.stroke-968")])]});
            var Q51;
            Q51=makeQuery(id+"F2.opExtrude","SWEPT_BODY",BODY,{"disambiguationData":[OSD([sQuery(id+"F0.wireOp",EDGE,"E0.sketch_text.stroke-969"),sQuery(id+"F0.wireOp",EDGE,"E0.sketch_text.stroke-970"),sQuery(id+"F0.wireOp",EDGE,"E0.sketch_text.stroke-971"),sQuery(id+"F0.wireOp",EDGE,"E0.sketch_text.stroke-972"),sQuery(id+"F0.wireOp",EDGE,"E0.sketch_text.stroke-973"),sQuery(id+"F0.wireOp",EDGE,"E0.sketch_text.stroke-974"),sQuery(id+"F0.wireOp",EDGE,"E0.sketch_text.stroke-975"),sQuery(id+"F0.wireOp",EDGE,"E0.sketch_text.stroke-976"),sQuery(id+"F0.wireOp",EDGE,"E0.sketch_text.stroke-977"),sQuery(id+"F0.wireOp",EDGE,"E0.sketch_text.stroke-978"),sQuery(id+"F0.wireOp",EDGE,"E0.sketch_text.stroke-979"),sQuery(id+"F0.wireOp",EDGE,"E0.sketch_text.stroke-980"),sQuery(id+"F0.wireOp",EDGE,"E0.sketch_text.stroke-981"),sQuery(id+"F0.wireOp",EDGE,"E0.sketch_text.stroke-982"),sQuery(id+"F0.wireOp",EDGE,"E0.sketch_text.stroke-983"),sQuery(id+"F0.wireOp",EDGE,"E0.sketch_text.stroke-984"),sQuery(id+"F0.wireOp",EDGE,"E0.sketch_text.stroke-985")])]});
            var Q52;
            Q52=makeQuery(id+"F2.opExtrude","SWEPT_BODY",BODY,{"disambiguationData":[OSD([sQuery(id+"F0.wireOp",EDGE,"E0.sketch_text.stroke-986"),sQuery(id+"F0.wireOp",EDGE,"E0.sketch_text.stroke-987"),sQuery(id+"F0.wireOp",EDGE,"E0.sketch_text.stroke-988"),sQuery(id+"F0.wireOp",EDGE,"E0.sketch_text.stroke-989"),sQuery(id+"F0.wireOp",EDGE,"E0.sketch_text.stroke-990"),sQuery(id+"F0.wireOp",EDGE,"E0.sketch_text.stroke-991"),sQuery(id+"F0.wireOp",EDGE,"E0.sketch_text.stroke-992"),sQuery(id+"F0.wireOp",EDGE,"E0.sketch_text.stroke-993"),sQuery(id+"F0.wireOp",EDGE,"E0.sketch_text.stroke-994"),sQuery(id+"F0.wireOp",EDGE,"E0.sketch_text.stroke-995"),sQuery(id+"F0.wireOp",EDGE,"E0.sketch_text.stroke-996"),sQuery(id+"F0.wireOp",EDGE,"E0.sketch_text.stroke-997"),sQuery(id+"F0.wireOp",EDGE,"E0.sketch_text.stroke-998"),sQuery(id+"F0.wireOp",EDGE,"E0.sketch_text.stroke-999"),sQuery(id+"F0.wireOp",EDGE,"E0.sketch_text.stroke-1000")])]});
            var Q53;
            Q53=makeQuery(id+"F2.opExtrude","SWEPT_BODY",BODY,{"disambiguationData":[OSD([sQuery(id+"F0.wireOp",EDGE,"E0.sketch_text.stroke-1001"),sQuery(id+"F0.wireOp",EDGE,"E0.sketch_text.stroke-1002"),sQuery(id+"F0.wireOp",EDGE,"E0.sketch_text.stroke-1003"),sQuery(id+"F0.wireOp",EDGE,"E0.sketch_text.stroke-1004"),sQuery(id+"F0.wireOp",EDGE,"E0.sketch_text.stroke-1005"),sQuery(id+"F0.wireOp",EDGE,"E0.sketch_text.stroke-1006"),sQuery(id+"F0.wireOp",EDGE,"E0.sketch_text.stroke-1007"),sQuery(id+"F0.wireOp",EDGE,"E0.sketch_text.stroke-1008"),sQuery(id+"F0.wireOp",EDGE,"E0.sketch_text.stroke-1009"),sQuery(id+"F0.wireOp",EDGE,"E0.sketch_text.stroke-1010"),sQuery(id+"F0.wireOp",EDGE,"E0.sketch_text.stroke-1011"),sQuery(id+"F0.wireOp",EDGE,"E0.sketch_text.stroke-1012"),sQuery(id+"F0.wireOp",EDGE,"E0.sketch_text.stroke-1013"),sQuery(id+"F0.wireOp",EDGE,"E0.sketch_text.stroke-1014"),sQuery(id+"F0.wireOp",EDGE,"E0.sketch_text.stroke-1015"),sQuery(id+"F0.wireOp",EDGE,"E0.sketch_text.stroke-1016"),sQuery(id+"F0.wireOp",EDGE,"E0.sketch_text.stroke-1017")])]});
            var Q54;
            Q54=makeQuery(id+"F2.opExtrude","SWEPT_BODY",BODY,{"disambiguationData":[OSD([sQuery(id+"F0.wireOp",EDGE,"E0.sketch_text.stroke-1022"),sQuery(id+"F0.wireOp",EDGE,"E0.sketch_text.stroke-1023"),sQuery(id+"F0.wireOp",EDGE,"E0.sketch_text.stroke-1024"),sQuery(id+"F0.wireOp",EDGE,"E0.sketch_text.stroke-1025")])]});
            var Q55;
            Q55=makeQuery(id+"F2.opExtrude","SWEPT_BODY",BODY,{"disambiguationData":[OSD([sQuery(id+"F0.wireOp",EDGE,"E0.sketch_text.stroke-1030"),sQuery(id+"F0.wireOp",EDGE,"E0.sketch_text.stroke-1031"),sQuery(id+"F0.wireOp",EDGE,"E0.sketch_text.stroke-1032"),sQuery(id+"F0.wireOp",EDGE,"E0.sketch_text.stroke-1033"),sQuery(id+"F0.wireOp",EDGE,"E0.sketch_text.stroke-1034"),sQuery(id+"F0.wireOp",EDGE,"E0.sketch_text.stroke-1035"),sQuery(id+"F0.wireOp",EDGE,"E0.sketch_text.stroke-1036"),sQuery(id+"F0.wireOp",EDGE,"E0.sketch_text.stroke-1037")])]});
            var Q56;
            Q56=makeQuery(id+"F2.opExtrude","SWEPT_BODY",BODY,{"disambiguationData":[OSD([sQuery(id+"F0.wireOp",EDGE,"E0.sketch_text.stroke-1038"),sQuery(id+"F0.wireOp",EDGE,"E0.sketch_text.stroke-1039"),sQuery(id+"F0.wireOp",EDGE,"E0.sketch_text.stroke-1040"),sQuery(id+"F0.wireOp",EDGE,"E0.sketch_text.stroke-1041"),sQuery(id+"F0.wireOp",EDGE,"E0.sketch_text.stroke-1042"),sQuery(id+"F0.wireOp",EDGE,"E0.sketch_text.stroke-1043"),sQuery(id+"F0.wireOp",EDGE,"E0.sketch_text.stroke-1044"),sQuery(id+"F0.wireOp",EDGE,"E0.sketch_text.stroke-1045"),sQuery(id+"F0.wireOp",EDGE,"E0.sketch_text.stroke-1046"),sQuery(id+"F0.wireOp",EDGE,"E0.sketch_text.stroke-1047"),sQuery(id+"F0.wireOp",EDGE,"E0.sketch_text.stroke-1048"),sQuery(id+"F0.wireOp",EDGE,"E0.sketch_text.stroke-1049"),sQuery(id+"F0.wireOp",EDGE,"E0.sketch_text.stroke-1050"),sQuery(id+"F0.wireOp",EDGE,"E0.sketch_text.stroke-1051"),sQuery(id+"F0.wireOp",EDGE,"E0.sketch_text.stroke-1052"),sQuery(id+"F0.wireOp",EDGE,"E0.sketch_text.stroke-1053"),sQuery(id+"F0.wireOp",EDGE,"E0.sketch_text.stroke-1054")])]});
            var Q57;
            Q57=makeQuery(id+"F2.opExtrude","SWEPT_BODY",BODY,{"disambiguationData":[OSD([sQuery(id+"F0.wireOp",EDGE,"E0.sketch_text.stroke-1055"),sQuery(id+"F0.wireOp",EDGE,"E0.sketch_text.stroke-1056"),sQuery(id+"F0.wireOp",EDGE,"E0.sketch_text.stroke-1057"),sQuery(id+"F0.wireOp",EDGE,"E0.sketch_text.stroke-1058")])]});
            var Q58;
            Q58=makeQuery(id+"F2.opExtrude","SWEPT_BODY",BODY,{"disambiguationData":[OSD([sQuery(id+"F0.wireOp",EDGE,"E0.sketch_text.stroke-1059"),sQuery(id+"F0.wireOp",EDGE,"E0.sketch_text.stroke-1060"),sQuery(id+"F0.wireOp",EDGE,"E0.sketch_text.stroke-1061"),sQuery(id+"F0.wireOp",EDGE,"E0.sketch_text.stroke-1062"),sQuery(id+"F0.wireOp",EDGE,"E0.sketch_text.stroke-1063"),sQuery(id+"F0.wireOp",EDGE,"E0.sketch_text.stroke-1064"),sQuery(id+"F0.wireOp",EDGE,"E0.sketch_text.stroke-1065"),sQuery(id+"F0.wireOp",EDGE,"E0.sketch_text.stroke-1066")])]});
            var Q59;
            Q59=makeQuery(id+"F2.opExtrude","SWEPT_BODY",BODY,{"disambiguationData":[OSD([sQuery(id+"F0.wireOp",EDGE,"E0.sketch_text.stroke-1067"),sQuery(id+"F0.wireOp",EDGE,"E0.sketch_text.stroke-1068"),sQuery(id+"F0.wireOp",EDGE,"E0.sketch_text.stroke-1069"),sQuery(id+"F0.wireOp",EDGE,"E0.sketch_text.stroke-1070")])]});
            var Q60;
            Q60=makeQuery(id+"F2.opExtrude","SWEPT_BODY",BODY,{"disambiguationData":[OSD([sQuery(id+"F0.wireOp",EDGE,"E0.sketch_text.stroke-1071"),sQuery(id+"F0.wireOp",EDGE,"E0.sketch_text.stroke-1072"),sQuery(id+"F0.wireOp",EDGE,"E0.sketch_text.stroke-1073"),sQuery(id+"F0.wireOp",EDGE,"E0.sketch_text.stroke-1074"),sQuery(id+"F0.wireOp",EDGE,"E0.sketch_text.stroke-1075"),sQuery(id+"F0.wireOp",EDGE,"E0.sketch_text.stroke-1076")])]});
            var Q61;
            Q61=makeQuery(id+"F2.opExtrude","SWEPT_BODY",BODY,{"disambiguationData":[OSD([sQuery(id+"F0.wireOp",EDGE,"E0.sketch_text.stroke-1081"),sQuery(id+"F0.wireOp",EDGE,"E0.sketch_text.stroke-1082"),sQuery(id+"F0.wireOp",EDGE,"E0.sketch_text.stroke-1083"),sQuery(id+"F0.wireOp",EDGE,"E0.sketch_text.stroke-1084"),sQuery(id+"F0.wireOp",EDGE,"E0.sketch_text.stroke-1085"),sQuery(id+"F0.wireOp",EDGE,"E0.sketch_text.stroke-1086"),sQuery(id+"F0.wireOp",EDGE,"E0.sketch_text.stroke-1087"),sQuery(id+"F0.wireOp",EDGE,"E0.sketch_text.stroke-1088")])]});
            var Q62;
            Q62=makeQuery(id+"F2.opExtrude","SWEPT_BODY",BODY,{"disambiguationData":[OSD([sQuery(id+"F0.wireOp",EDGE,"E0.sketch_text.stroke-1089"),sQuery(id+"F0.wireOp",EDGE,"E0.sketch_text.stroke-1090"),sQuery(id+"F0.wireOp",EDGE,"E0.sketch_text.stroke-1091"),sQuery(id+"F0.wireOp",EDGE,"E0.sketch_text.stroke-1092"),sQuery(id+"F0.wireOp",EDGE,"E0.sketch_text.stroke-1093"),sQuery(id+"F0.wireOp",EDGE,"E0.sketch_text.stroke-1094"),sQuery(id+"F0.wireOp",EDGE,"E0.sketch_text.stroke-1095"),sQuery(id+"F0.wireOp",EDGE,"E0.sketch_text.stroke-1096"),sQuery(id+"F0.wireOp",EDGE,"E0.sketch_text.stroke-1097"),sQuery(id+"F0.wireOp",EDGE,"E0.sketch_text.stroke-1098"),sQuery(id+"F0.wireOp",EDGE,"E0.sketch_text.stroke-1099"),sQuery(id+"F0.wireOp",EDGE,"E0.sketch_text.stroke-1100"),sQuery(id+"F0.wireOp",EDGE,"E0.sketch_text.stroke-1101"),sQuery(id+"F0.wireOp",EDGE,"E0.sketch_text.stroke-1102"),sQuery(id+"F0.wireOp",EDGE,"E0.sketch_text.stroke-1103")])]});
            var Q63;
            Q63=makeQuery(id+"F2.opExtrude","SWEPT_BODY",BODY,{"disambiguationData":[OSD([sQuery(id+"F0.wireOp",EDGE,"E0.sketch_text.stroke-1104"),sQuery(id+"F0.wireOp",EDGE,"E0.sketch_text.stroke-1105"),sQuery(id+"F0.wireOp",EDGE,"E0.sketch_text.stroke-1106"),sQuery(id+"F0.wireOp",EDGE,"E0.sketch_text.stroke-1107"),sQuery(id+"F0.wireOp",EDGE,"E0.sketch_text.stroke-1108"),sQuery(id+"F0.wireOp",EDGE,"E0.sketch_text.stroke-1109"),sQuery(id+"F0.wireOp",EDGE,"E0.sketch_text.stroke-1110"),sQuery(id+"F0.wireOp",EDGE,"E0.sketch_text.stroke-1111"),sQuery(id+"F0.wireOp",EDGE,"E0.sketch_text.stroke-1112"),sQuery(id+"F0.wireOp",EDGE,"E0.sketch_text.stroke-1113"),sQuery(id+"F0.wireOp",EDGE,"E0.sketch_text.stroke-1114"),sQuery(id+"F0.wireOp",EDGE,"E0.sketch_text.stroke-1115"),sQuery(id+"F0.wireOp",EDGE,"E0.sketch_text.stroke-1116"),sQuery(id+"F0.wireOp",EDGE,"E0.sketch_text.stroke-1117"),sQuery(id+"F0.wireOp",EDGE,"E0.sketch_text.stroke-1118"),sQuery(id+"F0.wireOp",EDGE,"E0.sketch_text.stroke-1119"),sQuery(id+"F0.wireOp",EDGE,"E0.sketch_text.stroke-1120"),sQuery(id+"F0.wireOp",EDGE,"E0.sketch_text.stroke-1121"),sQuery(id+"F0.wireOp",EDGE,"E0.sketch_text.stroke-1122")])]});
            var Q64;
            Q64=makeQuery(id+"F2.opExtrude","SWEPT_BODY",BODY,{"disambiguationData":[OSD([sQuery(id+"F0.wireOp",EDGE,"E0.sketch_text.stroke-1123"),sQuery(id+"F0.wireOp",EDGE,"E0.sketch_text.stroke-1124"),sQuery(id+"F0.wireOp",EDGE,"E0.sketch_text.stroke-1125"),sQuery(id+"F0.wireOp",EDGE,"E0.sketch_text.stroke-1126"),sQuery(id+"F0.wireOp",EDGE,"E0.sketch_text.stroke-1127"),sQuery(id+"F0.wireOp",EDGE,"E0.sketch_text.stroke-1128"),sQuery(id+"F0.wireOp",EDGE,"E0.sketch_text.stroke-1129"),sQuery(id+"F0.wireOp",EDGE,"E0.sketch_text.stroke-1130"),sQuery(id+"F0.wireOp",EDGE,"E0.sketch_text.stroke-1131"),sQuery(id+"F0.wireOp",EDGE,"E0.sketch_text.stroke-1132"),sQuery(id+"F0.wireOp",EDGE,"E0.sketch_text.stroke-1133"),sQuery(id+"F0.wireOp",EDGE,"E0.sketch_text.stroke-1134"),sQuery(id+"F0.wireOp",EDGE,"E0.sketch_text.stroke-1135"),sQuery(id+"F0.wireOp",EDGE,"E0.sketch_text.stroke-1136"),sQuery(id+"F0.wireOp",EDGE,"E0.sketch_text.stroke-1137"),sQuery(id+"F0.wireOp",EDGE,"E0.sketch_text.stroke-1138"),sQuery(id+"F0.wireOp",EDGE,"E0.sketch_text.stroke-1139")])]});
            var Q65;
            Q65=makeQuery(id+"F2.opExtrude","SWEPT_BODY",BODY,{"disambiguationData":[OSD([sQuery(id+"F0.wireOp",EDGE,"E0.sketch_text.stroke-1140"),sQuery(id+"F0.wireOp",EDGE,"E0.sketch_text.stroke-1141"),sQuery(id+"F0.wireOp",EDGE,"E0.sketch_text.stroke-1142"),sQuery(id+"F0.wireOp",EDGE,"E0.sketch_text.stroke-1143"),sQuery(id+"F0.wireOp",EDGE,"E0.sketch_text.stroke-1144"),sQuery(id+"F0.wireOp",EDGE,"E0.sketch_text.stroke-1145"),sQuery(id+"F0.wireOp",EDGE,"E0.sketch_text.stroke-1146"),sQuery(id+"F0.wireOp",EDGE,"E0.sketch_text.stroke-1147"),sQuery(id+"F0.wireOp",EDGE,"E0.sketch_text.stroke-1148"),sQuery(id+"F0.wireOp",EDGE,"E0.sketch_text.stroke-1149"),sQuery(id+"F0.wireOp",EDGE,"E0.sketch_text.stroke-1150"),sQuery(id+"F0.wireOp",EDGE,"E0.sketch_text.stroke-1151"),sQuery(id+"F0.wireOp",EDGE,"E0.sketch_text.stroke-1152"),sQuery(id+"F0.wireOp",EDGE,"E0.sketch_text.stroke-1153"),sQuery(id+"F0.wireOp",EDGE,"E0.sketch_text.stroke-1154")])]});
            var Q66;
            Q66=makeQuery(id+"F2.opExtrude","SWEPT_BODY",BODY,{"disambiguationData":[OSD([sQuery(id+"F0.wireOp",EDGE,"E0.sketch_text.stroke-1155"),sQuery(id+"F0.wireOp",EDGE,"E0.sketch_text.stroke-1156"),sQuery(id+"F0.wireOp",EDGE,"E0.sketch_text.stroke-1157"),sQuery(id+"F0.wireOp",EDGE,"E0.sketch_text.stroke-1158"),sQuery(id+"F0.wireOp",EDGE,"E0.sketch_text.stroke-1159"),sQuery(id+"F0.wireOp",EDGE,"E0.sketch_text.stroke-1160"),sQuery(id+"F0.wireOp",EDGE,"E0.sketch_text.stroke-1161"),sQuery(id+"F0.wireOp",EDGE,"E0.sketch_text.stroke-1162"),sQuery(id+"F0.wireOp",EDGE,"E0.sketch_text.stroke-1163"),sQuery(id+"F0.wireOp",EDGE,"E0.sketch_text.stroke-1164"),sQuery(id+"F0.wireOp",EDGE,"E0.sketch_text.stroke-1165"),sQuery(id+"F0.wireOp",EDGE,"E0.sketch_text.stroke-1166"),sQuery(id+"F0.wireOp",EDGE,"E0.sketch_text.stroke-1167"),sQuery(id+"F0.wireOp",EDGE,"E0.sketch_text.stroke-1168"),sQuery(id+"F0.wireOp",EDGE,"E0.sketch_text.stroke-1169"),sQuery(id+"F0.wireOp",EDGE,"E0.sketch_text.stroke-1170"),sQuery(id+"F0.wireOp",EDGE,"E0.sketch_text.stroke-1171"),sQuery(id+"F0.wireOp",EDGE,"E0.sketch_text.stroke-1172"),sQuery(id+"F0.wireOp",EDGE,"E0.sketch_text.stroke-1173")])]});
            var Q67;
            Q67=makeQuery(id+"F2.opExtrude","SWEPT_BODY",BODY,{"disambiguationData":[OSD([sQuery(id+"F0.wireOp",EDGE,"E0.sketch_text.stroke-1174"),sQuery(id+"F0.wireOp",EDGE,"E0.sketch_text.stroke-1175"),sQuery(id+"F0.wireOp",EDGE,"E0.sketch_text.stroke-1176"),sQuery(id+"F0.wireOp",EDGE,"E0.sketch_text.stroke-1177"),sQuery(id+"F0.wireOp",EDGE,"E0.sketch_text.stroke-1178"),sQuery(id+"F0.wireOp",EDGE,"E0.sketch_text.stroke-1179"),sQuery(id+"F0.wireOp",EDGE,"E0.sketch_text.stroke-1180"),sQuery(id+"F0.wireOp",EDGE,"E0.sketch_text.stroke-1181"),sQuery(id+"F0.wireOp",EDGE,"E0.sketch_text.stroke-1182"),sQuery(id+"F0.wireOp",EDGE,"E0.sketch_text.stroke-1183"),sQuery(id+"F0.wireOp",EDGE,"E0.sketch_text.stroke-1184"),sQuery(id+"F0.wireOp",EDGE,"E0.sketch_text.stroke-1185"),sQuery(id+"F0.wireOp",EDGE,"E0.sketch_text.stroke-1186"),sQuery(id+"F0.wireOp",EDGE,"E0.sketch_text.stroke-1187"),sQuery(id+"F0.wireOp",EDGE,"E0.sketch_text.stroke-1188")])]});
            var Q68;
            Q68=makeQuery(id+"F2.opExtrude","SWEPT_BODY",BODY,{"disambiguationData":[OSD([sQuery(id+"F0.wireOp",EDGE,"E0.sketch_text.stroke-1202"),sQuery(id+"F0.wireOp",EDGE,"E0.sketch_text.stroke-1203"),sQuery(id+"F0.wireOp",EDGE,"E0.sketch_text.stroke-1204"),sQuery(id+"F0.wireOp",EDGE,"E0.sketch_text.stroke-1205"),sQuery(id+"F0.wireOp",EDGE,"E0.sketch_text.stroke-1206"),sQuery(id+"F0.wireOp",EDGE,"E0.sketch_text.stroke-1207"),sQuery(id+"F0.wireOp",EDGE,"E0.sketch_text.stroke-1208"),sQuery(id+"F0.wireOp",EDGE,"E0.sketch_text.stroke-1209"),sQuery(id+"F0.wireOp",EDGE,"E0.sketch_text.stroke-1210"),sQuery(id+"F0.wireOp",EDGE,"E0.sketch_text.stroke-1211"),sQuery(id+"F0.wireOp",EDGE,"E0.sketch_text.stroke-1212"),sQuery(id+"F0.wireOp",EDGE,"E0.sketch_text.stroke-1213"),sQuery(id+"F0.wireOp",EDGE,"E0.sketch_text.stroke-1214"),sQuery(id+"F0.wireOp",EDGE,"E0.sketch_text.stroke-1215"),sQuery(id+"F0.wireOp",EDGE,"E0.sketch_text.stroke-1216"),sQuery(id+"F0.wireOp",EDGE,"E0.sketch_text.stroke-1217"),sQuery(id+"F0.wireOp",EDGE,"E0.sketch_text.stroke-1218"),sQuery(id+"F0.wireOp",EDGE,"E0.sketch_text.stroke-1219"),sQuery(id+"F0.wireOp",EDGE,"E0.sketch_text.stroke-1220")])]});
            var Q69;
            Q69=makeQuery(id+"F2.opExtrude","SWEPT_BODY",BODY,{"disambiguationData":[OSD([sQuery(id+"F0.wireOp",EDGE,"E0.sketch_text.stroke-1221"),sQuery(id+"F0.wireOp",EDGE,"E0.sketch_text.stroke-1222"),sQuery(id+"F0.wireOp",EDGE,"E0.sketch_text.stroke-1223"),sQuery(id+"F0.wireOp",EDGE,"E0.sketch_text.stroke-1224"),sQuery(id+"F0.wireOp",EDGE,"E0.sketch_text.stroke-1225"),sQuery(id+"F0.wireOp",EDGE,"E0.sketch_text.stroke-1226"),sQuery(id+"F0.wireOp",EDGE,"E0.sketch_text.stroke-1227"),sQuery(id+"F0.wireOp",EDGE,"E0.sketch_text.stroke-1228"),sQuery(id+"F0.wireOp",EDGE,"E0.sketch_text.stroke-1229"),sQuery(id+"F0.wireOp",EDGE,"E0.sketch_text.stroke-1230"),sQuery(id+"F0.wireOp",EDGE,"E0.sketch_text.stroke-1231"),sQuery(id+"F0.wireOp",EDGE,"E0.sketch_text.stroke-1232"),sQuery(id+"F0.wireOp",EDGE,"E0.sketch_text.stroke-1233"),sQuery(id+"F0.wireOp",EDGE,"E0.sketch_text.stroke-1234"),sQuery(id+"F0.wireOp",EDGE,"E0.sketch_text.stroke-1235"),sQuery(id+"F0.wireOp",EDGE,"E0.sketch_text.stroke-1236"),sQuery(id+"F0.wireOp",EDGE,"E0.sketch_text.stroke-1237"),sQuery(id+"F0.wireOp",EDGE,"E0.sketch_text.stroke-1238"),sQuery(id+"F0.wireOp",EDGE,"E0.sketch_text.stroke-1239"),sQuery(id+"F0.wireOp",EDGE,"E0.sketch_text.stroke-1240"),sQuery(id+"F0.wireOp",EDGE,"E0.sketch_text.stroke-1241"),sQuery(id+"F0.wireOp",EDGE,"E0.sketch_text.stroke-1242"),sQuery(id+"F0.wireOp",EDGE,"E0.sketch_text.stroke-1243"),sQuery(id+"F0.wireOp",EDGE,"E0.sketch_text.stroke-1244"),sQuery(id+"F0.wireOp",EDGE,"E0.sketch_text.stroke-1245"),sQuery(id+"F0.wireOp",EDGE,"E0.sketch_text.stroke-1246"),sQuery(id+"F0.wireOp",EDGE,"E0.sketch_text.stroke-1247")])]});
            var Q70;
            Q70=makeQuery(id+"F2.opExtrude","SWEPT_BODY",BODY,{"disambiguationData":[OSD([sQuery(id+"F0.wireOp",EDGE,"E0.sketch_text.stroke-1248"),sQuery(id+"F0.wireOp",EDGE,"E0.sketch_text.stroke-1249"),sQuery(id+"F0.wireOp",EDGE,"E0.sketch_text.stroke-1250"),sQuery(id+"F0.wireOp",EDGE,"E0.sketch_text.stroke-1251"),sQuery(id+"F0.wireOp",EDGE,"E0.sketch_text.stroke-1252"),sQuery(id+"F0.wireOp",EDGE,"E0.sketch_text.stroke-1253"),sQuery(id+"F0.wireOp",EDGE,"E0.sketch_text.stroke-1254"),sQuery(id+"F0.wireOp",EDGE,"E0.sketch_text.stroke-1255"),sQuery(id+"F0.wireOp",EDGE,"E0.sketch_text.stroke-1256"),sQuery(id+"F0.wireOp",EDGE,"E0.sketch_text.stroke-1257"),sQuery(id+"F0.wireOp",EDGE,"E0.sketch_text.stroke-1258"),sQuery(id+"F0.wireOp",EDGE,"E0.sketch_text.stroke-1259"),sQuery(id+"F0.wireOp",EDGE,"E0.sketch_text.stroke-1260"),sQuery(id+"F0.wireOp",EDGE,"E0.sketch_text.stroke-1261"),sQuery(id+"F0.wireOp",EDGE,"E0.sketch_text.stroke-1262"),sQuery(id+"F0.wireOp",EDGE,"E0.sketch_text.stroke-1263"),sQuery(id+"F0.wireOp",EDGE,"E0.sketch_text.stroke-1264"),sQuery(id+"F0.wireOp",EDGE,"E0.sketch_text.stroke-1265"),sQuery(id+"F0.wireOp",EDGE,"E0.sketch_text.stroke-1266")])]});
            var Q71;
            Q71=makeQuery(id+"F2.opExtrude","SWEPT_BODY",BODY,{"disambiguationData":[OSD([sQuery(id+"F0.wireOp",EDGE,"E0.sketch_text.stroke-1271"),sQuery(id+"F0.wireOp",EDGE,"E0.sketch_text.stroke-1272"),sQuery(id+"F0.wireOp",EDGE,"E0.sketch_text.stroke-1273"),sQuery(id+"F0.wireOp",EDGE,"E0.sketch_text.stroke-1274"),sQuery(id+"F0.wireOp",EDGE,"E0.sketch_text.stroke-1275"),sQuery(id+"F0.wireOp",EDGE,"E0.sketch_text.stroke-1276"),sQuery(id+"F0.wireOp",EDGE,"E0.sketch_text.stroke-1277"),sQuery(id+"F0.wireOp",EDGE,"E0.sketch_text.stroke-1278")])]});
            var Q72;
            Q72=makeQuery(id+"F2.opExtrude","SWEPT_BODY",BODY,{"disambiguationData":[OSD([sQuery(id+"F0.wireOp",EDGE,"E0.sketch_text.stroke-1279"),sQuery(id+"F0.wireOp",EDGE,"E0.sketch_text.stroke-1280"),sQuery(id+"F0.wireOp",EDGE,"E0.sketch_text.stroke-1281"),sQuery(id+"F0.wireOp",EDGE,"E0.sketch_text.stroke-1282"),sQuery(id+"F0.wireOp",EDGE,"E0.sketch_text.stroke-1283"),sQuery(id+"F0.wireOp",EDGE,"E0.sketch_text.stroke-1284"),sQuery(id+"F0.wireOp",EDGE,"E0.sketch_text.stroke-1285"),sQuery(id+"F0.wireOp",EDGE,"E0.sketch_text.stroke-1286"),sQuery(id+"F0.wireOp",EDGE,"E0.sketch_text.stroke-1287"),sQuery(id+"F0.wireOp",EDGE,"E0.sketch_text.stroke-1288")])]});
            var Q73;
            Q73=makeQuery(id+"F2.opExtrude","SWEPT_BODY",BODY,{"disambiguationData":[OSD([sQuery(id+"F0.wireOp",EDGE,"E0.sketch_text.stroke-1289"),sQuery(id+"F0.wireOp",EDGE,"E0.sketch_text.stroke-1290"),sQuery(id+"F0.wireOp",EDGE,"E0.sketch_text.stroke-1291"),sQuery(id+"F0.wireOp",EDGE,"E0.sketch_text.stroke-1292"),sQuery(id+"F0.wireOp",EDGE,"E0.sketch_text.stroke-1293"),sQuery(id+"F0.wireOp",EDGE,"E0.sketch_text.stroke-1294"),sQuery(id+"F0.wireOp",EDGE,"E0.sketch_text.stroke-1295"),sQuery(id+"F0.wireOp",EDGE,"E0.sketch_text.stroke-1296"),sQuery(id+"F0.wireOp",EDGE,"E0.sketch_text.stroke-1297"),sQuery(id+"F0.wireOp",EDGE,"E0.sketch_text.stroke-1298"),sQuery(id+"F0.wireOp",EDGE,"E0.sketch_text.stroke-1299"),sQuery(id+"F0.wireOp",EDGE,"E0.sketch_text.stroke-1300"),sQuery(id+"F0.wireOp",EDGE,"E0.sketch_text.stroke-1301"),sQuery(id+"F0.wireOp",EDGE,"E0.sketch_text.stroke-1302"),sQuery(id+"F0.wireOp",EDGE,"E0.sketch_text.stroke-1303"),sQuery(id+"F0.wireOp",EDGE,"E0.sketch_text.stroke-1304"),sQuery(id+"F0.wireOp",EDGE,"E0.sketch_text.stroke-1305"),sQuery(id+"F0.wireOp",EDGE,"E0.sketch_text.stroke-1306"),sQuery(id+"F0.wireOp",EDGE,"E0.sketch_text.stroke-1307")])]});
            var Q74;
            Q74=makeQuery(id+"F2.opExtrude","SWEPT_BODY",BODY,{"disambiguationData":[OSD([sQuery(id+"F0.wireOp",EDGE,"E0.sketch_text.stroke-1308"),sQuery(id+"F0.wireOp",EDGE,"E0.sketch_text.stroke-1309"),sQuery(id+"F0.wireOp",EDGE,"E0.sketch_text.stroke-1310"),sQuery(id+"F0.wireOp",EDGE,"E0.sketch_text.stroke-1311"),sQuery(id+"F0.wireOp",EDGE,"E0.sketch_text.stroke-1312"),sQuery(id+"F0.wireOp",EDGE,"E0.sketch_text.stroke-1313"),sQuery(id+"F0.wireOp",EDGE,"E0.sketch_text.stroke-1314"),sQuery(id+"F0.wireOp",EDGE,"E0.sketch_text.stroke-1315"),sQuery(id+"F0.wireOp",EDGE,"E0.sketch_text.stroke-1316"),sQuery(id+"F0.wireOp",EDGE,"E0.sketch_text.stroke-1317"),sQuery(id+"F0.wireOp",EDGE,"E0.sketch_text.stroke-1318"),sQuery(id+"F0.wireOp",EDGE,"E0.sketch_text.stroke-1319"),sQuery(id+"F0.wireOp",EDGE,"E0.sketch_text.stroke-1320"),sQuery(id+"F0.wireOp",EDGE,"E0.sketch_text.stroke-1321"),sQuery(id+"F0.wireOp",EDGE,"E0.sketch_text.stroke-1322")])]});
            var Q75;
            Q75=makeQuery(id+"F2.opExtrude","SWEPT_BODY",BODY,{"disambiguationData":[OSD([sQuery(id+"F0.wireOp",EDGE,"E0.sketch_text.stroke-1323"),sQuery(id+"F0.wireOp",EDGE,"E0.sketch_text.stroke-1324"),sQuery(id+"F0.wireOp",EDGE,"E0.sketch_text.stroke-1325"),sQuery(id+"F0.wireOp",EDGE,"E0.sketch_text.stroke-1326"),sQuery(id+"F0.wireOp",EDGE,"E0.sketch_text.stroke-1327"),sQuery(id+"F0.wireOp",EDGE,"E0.sketch_text.stroke-1328"),sQuery(id+"F0.wireOp",EDGE,"E0.sketch_text.stroke-1329"),sQuery(id+"F0.wireOp",EDGE,"E0.sketch_text.stroke-1330"),sQuery(id+"F0.wireOp",EDGE,"E0.sketch_text.stroke-1331"),sQuery(id+"F0.wireOp",EDGE,"E0.sketch_text.stroke-1332"),sQuery(id+"F0.wireOp",EDGE,"E0.sketch_text.stroke-1333"),sQuery(id+"F0.wireOp",EDGE,"E0.sketch_text.stroke-1334"),sQuery(id+"F0.wireOp",EDGE,"E0.sketch_text.stroke-1335"),sQuery(id+"F0.wireOp",EDGE,"E0.sketch_text.stroke-1336"),sQuery(id+"F0.wireOp",EDGE,"E0.sketch_text.stroke-1337"),sQuery(id+"F0.wireOp",EDGE,"E0.sketch_text.stroke-1338"),sQuery(id+"F0.wireOp",EDGE,"E0.sketch_text.stroke-1339")])]});
            var Q76;
            Q76=makeQuery(id+"F2.opExtrude","SWEPT_BODY",BODY,{"disambiguationData":[OSD([sQuery(id+"F0.wireOp",EDGE,"E0.sketch_text.stroke-1340"),sQuery(id+"F0.wireOp",EDGE,"E0.sketch_text.stroke-1341"),sQuery(id+"F0.wireOp",EDGE,"E0.sketch_text.stroke-1342"),sQuery(id+"F0.wireOp",EDGE,"E0.sketch_text.stroke-1343"),sQuery(id+"F0.wireOp",EDGE,"E0.sketch_text.stroke-1344"),sQuery(id+"F0.wireOp",EDGE,"E0.sketch_text.stroke-1345"),sQuery(id+"F0.wireOp",EDGE,"E0.sketch_text.stroke-1346"),sQuery(id+"F0.wireOp",EDGE,"E0.sketch_text.stroke-1347"),sQuery(id+"F0.wireOp",EDGE,"E0.sketch_text.stroke-1348"),sQuery(id+"F0.wireOp",EDGE,"E0.sketch_text.stroke-1349"),sQuery(id+"F0.wireOp",EDGE,"E0.sketch_text.stroke-1350"),sQuery(id+"F0.wireOp",EDGE,"E0.sketch_text.stroke-1351"),sQuery(id+"F0.wireOp",EDGE,"E0.sketch_text.stroke-1352"),sQuery(id+"F0.wireOp",EDGE,"E0.sketch_text.stroke-1353"),sQuery(id+"F0.wireOp",EDGE,"E0.sketch_text.stroke-1354"),sQuery(id+"F0.wireOp",EDGE,"E0.sketch_text.stroke-1355"),sQuery(id+"F0.wireOp",EDGE,"E0.sketch_text.stroke-1356"),sQuery(id+"F0.wireOp",EDGE,"E0.sketch_text.stroke-1357"),sQuery(id+"F0.wireOp",EDGE,"E0.sketch_text.stroke-1358"),sQuery(id+"F0.wireOp",EDGE,"E0.sketch_text.stroke-1359"),sQuery(id+"F0.wireOp",EDGE,"E0.sketch_text.stroke-1360"),sQuery(id+"F0.wireOp",EDGE,"E0.sketch_text.stroke-1361"),sQuery(id+"F0.wireOp",EDGE,"E0.sketch_text.stroke-1362"),sQuery(id+"F0.wireOp",EDGE,"E0.sketch_text.stroke-1363"),sQuery(id+"F0.wireOp",EDGE,"E0.sketch_text.stroke-1364"),sQuery(id+"F0.wireOp",EDGE,"E0.sketch_text.stroke-1365"),sQuery(id+"F0.wireOp",EDGE,"E0.sketch_text.stroke-1366"),sQuery(id+"F0.wireOp",EDGE,"E0.sketch_text.stroke-1367")])]});
            var Q77;
            Q77=makeQuery(id+"F2.opExtrude","SWEPT_BODY",BODY,{"disambiguationData":[OSD([sQuery(id+"F0.wireOp",EDGE,"E0.sketch_text.stroke-1368"),sQuery(id+"F0.wireOp",EDGE,"E0.sketch_text.stroke-1369"),sQuery(id+"F0.wireOp",EDGE,"E0.sketch_text.stroke-1370"),sQuery(id+"F0.wireOp",EDGE,"E0.sketch_text.stroke-1371"),sQuery(id+"F0.wireOp",EDGE,"E0.sketch_text.stroke-1372"),sQuery(id+"F0.wireOp",EDGE,"E0.sketch_text.stroke-1373"),sQuery(id+"F0.wireOp",EDGE,"E0.sketch_text.stroke-1374"),sQuery(id+"F0.wireOp",EDGE,"E0.sketch_text.stroke-1375"),sQuery(id+"F0.wireOp",EDGE,"E0.sketch_text.stroke-1376"),sQuery(id+"F0.wireOp",EDGE,"E0.sketch_text.stroke-1377"),sQuery(id+"F0.wireOp",EDGE,"E0.sketch_text.stroke-1378"),sQuery(id+"F0.wireOp",EDGE,"E0.sketch_text.stroke-1379"),sQuery(id+"F0.wireOp",EDGE,"E0.sketch_text.stroke-1380"),sQuery(id+"F0.wireOp",EDGE,"E0.sketch_text.stroke-1381"),sQuery(id+"F0.wireOp",EDGE,"E0.sketch_text.stroke-1382"),sQuery(id+"F0.wireOp",EDGE,"E0.sketch_text.stroke-1383"),sQuery(id+"F0.wireOp",EDGE,"E0.sketch_text.stroke-1384"),sQuery(id+"F0.wireOp",EDGE,"E0.sketch_text.stroke-1385"),sQuery(id+"F0.wireOp",EDGE,"E0.sketch_text.stroke-1386"),sQuery(id+"F0.wireOp",EDGE,"E0.sketch_text.stroke-1387"),sQuery(id+"F0.wireOp",EDGE,"E0.sketch_text.stroke-1388"),sQuery(id+"F0.wireOp",EDGE,"E0.sketch_text.stroke-1389"),sQuery(id+"F0.wireOp",EDGE,"E0.sketch_text.stroke-1390"),sQuery(id+"F0.wireOp",EDGE,"E0.sketch_text.stroke-1391"),sQuery(id+"F0.wireOp",EDGE,"E0.sketch_text.stroke-1392"),sQuery(id+"F0.wireOp",EDGE,"E0.sketch_text.stroke-1393"),sQuery(id+"F0.wireOp",EDGE,"E0.sketch_text.stroke-1394"),sQuery(id+"F0.wireOp",EDGE,"E0.sketch_text.stroke-1395")])]});
            var Q78;
            Q78=makeQuery(id+"F2.opExtrude","SWEPT_BODY",BODY,{"disambiguationData":[OSD([sQuery(id+"F0.wireOp",EDGE,"E0.sketch_text.stroke-1396"),sQuery(id+"F0.wireOp",EDGE,"E0.sketch_text.stroke-1397"),sQuery(id+"F0.wireOp",EDGE,"E0.sketch_text.stroke-1398"),sQuery(id+"F0.wireOp",EDGE,"E0.sketch_text.stroke-1399"),sQuery(id+"F0.wireOp",EDGE,"E0.sketch_text.stroke-1400"),sQuery(id+"F0.wireOp",EDGE,"E0.sketch_text.stroke-1401"),sQuery(id+"F0.wireOp",EDGE,"E0.sketch_text.stroke-1402"),sQuery(id+"F0.wireOp",EDGE,"E0.sketch_text.stroke-1403"),sQuery(id+"F0.wireOp",EDGE,"E0.sketch_text.stroke-1404"),sQuery(id+"F0.wireOp",EDGE,"E0.sketch_text.stroke-1405"),sQuery(id+"F0.wireOp",EDGE,"E0.sketch_text.stroke-1406"),sQuery(id+"F0.wireOp",EDGE,"E0.sketch_text.stroke-1407"),sQuery(id+"F0.wireOp",EDGE,"E0.sketch_text.stroke-1408"),sQuery(id+"F0.wireOp",EDGE,"E0.sketch_text.stroke-1409"),sQuery(id+"F0.wireOp",EDGE,"E0.sketch_text.stroke-1410"),sQuery(id+"F0.wireOp",EDGE,"E0.sketch_text.stroke-1411"),sQuery(id+"F0.wireOp",EDGE,"E0.sketch_text.stroke-1412")])]});
            var Q79;
            Q79=makeQuery(id+"F2.opExtrude","SWEPT_BODY",BODY,{"disambiguationData":[OSD([sQuery(id+"F0.wireOp",EDGE,"E0.sketch_text.stroke-1413"),sQuery(id+"F0.wireOp",EDGE,"E0.sketch_text.stroke-1414"),sQuery(id+"F0.wireOp",EDGE,"E0.sketch_text.stroke-1415"),sQuery(id+"F0.wireOp",EDGE,"E0.sketch_text.stroke-1416"),sQuery(id+"F0.wireOp",EDGE,"E0.sketch_text.stroke-1417"),sQuery(id+"F0.wireOp",EDGE,"E0.sketch_text.stroke-1418"),sQuery(id+"F0.wireOp",EDGE,"E0.sketch_text.stroke-1419"),sQuery(id+"F0.wireOp",EDGE,"E0.sketch_text.stroke-1420"),sQuery(id+"F0.wireOp",EDGE,"E0.sketch_text.stroke-1421"),sQuery(id+"F0.wireOp",EDGE,"E0.sketch_text.stroke-1422"),sQuery(id+"F0.wireOp",EDGE,"E0.sketch_text.stroke-1423"),sQuery(id+"F0.wireOp",EDGE,"E0.sketch_text.stroke-1424"),sQuery(id+"F0.wireOp",EDGE,"E0.sketch_text.stroke-1425"),sQuery(id+"F0.wireOp",EDGE,"E0.sketch_text.stroke-1426"),sQuery(id+"F0.wireOp",EDGE,"E0.sketch_text.stroke-1427"),sQuery(id+"F0.wireOp",EDGE,"E0.sketch_text.stroke-1428"),sQuery(id+"F0.wireOp",EDGE,"E0.sketch_text.stroke-1429")])]});
            var Q80;
            Q80=makeQuery(id+"F2.opExtrude","SWEPT_BODY",BODY,{"disambiguationData":[OSD([sQuery(id+"F0.wireOp",EDGE,"E0.sketch_text.stroke-1430"),sQuery(id+"F0.wireOp",EDGE,"E0.sketch_text.stroke-1431"),sQuery(id+"F0.wireOp",EDGE,"E0.sketch_text.stroke-1432"),sQuery(id+"F0.wireOp",EDGE,"E0.sketch_text.stroke-1433"),sQuery(id+"F0.wireOp",EDGE,"E0.sketch_text.stroke-1434"),sQuery(id+"F0.wireOp",EDGE,"E0.sketch_text.stroke-1435"),sQuery(id+"F0.wireOp",EDGE,"E0.sketch_text.stroke-1436"),sQuery(id+"F0.wireOp",EDGE,"E0.sketch_text.stroke-1437"),sQuery(id+"F0.wireOp",EDGE,"E0.sketch_text.stroke-1438"),sQuery(id+"F0.wireOp",EDGE,"E0.sketch_text.stroke-1439"),sQuery(id+"F0.wireOp",EDGE,"E0.sketch_text.stroke-1440"),sQuery(id+"F0.wireOp",EDGE,"E0.sketch_text.stroke-1441"),sQuery(id+"F0.wireOp",EDGE,"E0.sketch_text.stroke-1442"),sQuery(id+"F0.wireOp",EDGE,"E0.sketch_text.stroke-1443"),sQuery(id+"F0.wireOp",EDGE,"E0.sketch_text.stroke-1444"),sQuery(id+"F0.wireOp",EDGE,"E0.sketch_text.stroke-1445"),sQuery(id+"F0.wireOp",EDGE,"E0.sketch_text.stroke-1446"),sQuery(id+"F0.wireOp",EDGE,"E0.sketch_text.stroke-1447"),sQuery(id+"F0.wireOp",EDGE,"E0.sketch_text.stroke-1448"),sQuery(id+"F0.wireOp",EDGE,"E0.sketch_text.stroke-1449"),sQuery(id+"F0.wireOp",EDGE,"E0.sketch_text.stroke-1450"),sQuery(id+"F0.wireOp",EDGE,"E0.sketch_text.stroke-1451"),sQuery(id+"F0.wireOp",EDGE,"E0.sketch_text.stroke-1452"),sQuery(id+"F0.wireOp",EDGE,"E0.sketch_text.stroke-1453"),sQuery(id+"F0.wireOp",EDGE,"E0.sketch_text.stroke-1454")])]});
            var Q81;
            Q81=makeQuery(id+"F2.opExtrude","SWEPT_BODY",BODY,{"disambiguationData":[OSD([sQuery(id+"F0.wireOp",EDGE,"E0.sketch_text.stroke-1455"),sQuery(id+"F0.wireOp",EDGE,"E0.sketch_text.stroke-1456"),sQuery(id+"F0.wireOp",EDGE,"E0.sketch_text.stroke-1457"),sQuery(id+"F0.wireOp",EDGE,"E0.sketch_text.stroke-1458"),sQuery(id+"F0.wireOp",EDGE,"E0.sketch_text.stroke-1459"),sQuery(id+"F0.wireOp",EDGE,"E0.sketch_text.stroke-1460"),sQuery(id+"F0.wireOp",EDGE,"E0.sketch_text.stroke-1461"),sQuery(id+"F0.wireOp",EDGE,"E0.sketch_text.stroke-1462"),sQuery(id+"F0.wireOp",EDGE,"E0.sketch_text.stroke-1463"),sQuery(id+"F0.wireOp",EDGE,"E0.sketch_text.stroke-1464"),sQuery(id+"F0.wireOp",EDGE,"E0.sketch_text.stroke-1465"),sQuery(id+"F0.wireOp",EDGE,"E0.sketch_text.stroke-1466"),sQuery(id+"F0.wireOp",EDGE,"E0.sketch_text.stroke-1467"),sQuery(id+"F0.wireOp",EDGE,"E0.sketch_text.stroke-1468"),sQuery(id+"F0.wireOp",EDGE,"E0.sketch_text.stroke-1469"),sQuery(id+"F0.wireOp",EDGE,"E0.sketch_text.stroke-1470"),sQuery(id+"F0.wireOp",EDGE,"E0.sketch_text.stroke-1471"),sQuery(id+"F0.wireOp",EDGE,"E0.sketch_text.stroke-1472"),sQuery(id+"F0.wireOp",EDGE,"E0.sketch_text.stroke-1473"),sQuery(id+"F0.wireOp",EDGE,"E0.sketch_text.stroke-1474"),sQuery(id+"F0.wireOp",EDGE,"E0.sketch_text.stroke-1475"),sQuery(id+"F0.wireOp",EDGE,"E0.sketch_text.stroke-1476"),sQuery(id+"F0.wireOp",EDGE,"E0.sketch_text.stroke-1477"),sQuery(id+"F0.wireOp",EDGE,"E0.sketch_text.stroke-1478"),sQuery(id+"F0.wireOp",EDGE,"E0.sketch_text.stroke-1479")])]});
            var Q82;
            Q82=makeQuery(id+"F2.opExtrude","SWEPT_BODY",BODY,{"disambiguationData":[OSD([sQuery(id+"F0.wireOp",EDGE,"E0.sketch_text.stroke-1480"),sQuery(id+"F0.wireOp",EDGE,"E0.sketch_text.stroke-1481"),sQuery(id+"F0.wireOp",EDGE,"E0.sketch_text.stroke-1482"),sQuery(id+"F0.wireOp",EDGE,"E0.sketch_text.stroke-1483"),sQuery(id+"F0.wireOp",EDGE,"E0.sketch_text.stroke-1484"),sQuery(id+"F0.wireOp",EDGE,"E0.sketch_text.stroke-1485"),sQuery(id+"F0.wireOp",EDGE,"E0.sketch_text.stroke-1486"),sQuery(id+"F0.wireOp",EDGE,"E0.sketch_text.stroke-1487"),sQuery(id+"F0.wireOp",EDGE,"E0.sketch_text.stroke-1488"),sQuery(id+"F0.wireOp",EDGE,"E0.sketch_text.stroke-1489"),sQuery(id+"F0.wireOp",EDGE,"E0.sketch_text.stroke-1490"),sQuery(id+"F0.wireOp",EDGE,"E0.sketch_text.stroke-1491"),sQuery(id+"F0.wireOp",EDGE,"E0.sketch_text.stroke-1492"),sQuery(id+"F0.wireOp",EDGE,"E0.sketch_text.stroke-1493"),sQuery(id+"F0.wireOp",EDGE,"E0.sketch_text.stroke-1494"),sQuery(id+"F0.wireOp",EDGE,"E0.sketch_text.stroke-1495"),sQuery(id+"F0.wireOp",EDGE,"E0.sketch_text.stroke-1496"),sQuery(id+"F0.wireOp",EDGE,"E0.sketch_text.stroke-1497")])]});
            var Q83;
            Q83=makeQuery(id+"F2.opExtrude","SWEPT_BODY",BODY,{"disambiguationData":[OSD([sQuery(id+"F0.wireOp",EDGE,"E0.sketch_text.stroke-1498"),sQuery(id+"F0.wireOp",EDGE,"E0.sketch_text.stroke-1499"),sQuery(id+"F0.wireOp",EDGE,"E0.sketch_text.stroke-1500"),sQuery(id+"F0.wireOp",EDGE,"E0.sketch_text.stroke-1501"),sQuery(id+"F0.wireOp",EDGE,"E0.sketch_text.stroke-1502"),sQuery(id+"F0.wireOp",EDGE,"E0.sketch_text.stroke-1503"),sQuery(id+"F0.wireOp",EDGE,"E0.sketch_text.stroke-1504"),sQuery(id+"F0.wireOp",EDGE,"E0.sketch_text.stroke-1505"),sQuery(id+"F0.wireOp",EDGE,"E0.sketch_text.stroke-1506"),sQuery(id+"F0.wireOp",EDGE,"E0.sketch_text.stroke-1507"),sQuery(id+"F0.wireOp",EDGE,"E0.sketch_text.stroke-1508"),sQuery(id+"F0.wireOp",EDGE,"E0.sketch_text.stroke-1509"),sQuery(id+"F0.wireOp",EDGE,"E0.sketch_text.stroke-1510"),sQuery(id+"F0.wireOp",EDGE,"E0.sketch_text.stroke-1511"),sQuery(id+"F0.wireOp",EDGE,"E0.sketch_text.stroke-1512"),sQuery(id+"F0.wireOp",EDGE,"E0.sketch_text.stroke-1513"),sQuery(id+"F0.wireOp",EDGE,"E0.sketch_text.stroke-1514"),sQuery(id+"F0.wireOp",EDGE,"E0.sketch_text.stroke-1515"),sQuery(id+"F0.wireOp",EDGE,"E0.sketch_text.stroke-1516"),sQuery(id+"F0.wireOp",EDGE,"E0.sketch_text.stroke-1517"),sQuery(id+"F0.wireOp",EDGE,"E0.sketch_text.stroke-1518"),sQuery(id+"F0.wireOp",EDGE,"E0.sketch_text.stroke-1519"),sQuery(id+"F0.wireOp",EDGE,"E0.sketch_text.stroke-1520"),sQuery(id+"F0.wireOp",EDGE,"E0.sketch_text.stroke-1521"),sQuery(id+"F0.wireOp",EDGE,"E0.sketch_text.stroke-1522"),sQuery(id+"F0.wireOp",EDGE,"E0.sketch_text.stroke-1523"),sQuery(id+"F0.wireOp",EDGE,"E0.sketch_text.stroke-1524")])]});
            var Q84;
            Q84=makeQuery(id+"F2.opExtrude","SWEPT_BODY",BODY,{"disambiguationData":[OSD([sQuery(id+"F0.wireOp",EDGE,"E0.sketch_text.stroke-1525"),sQuery(id+"F0.wireOp",EDGE,"E0.sketch_text.stroke-1526"),sQuery(id+"F0.wireOp",EDGE,"E0.sketch_text.stroke-1527"),sQuery(id+"F0.wireOp",EDGE,"E0.sketch_text.stroke-1528"),sQuery(id+"F0.wireOp",EDGE,"E0.sketch_text.stroke-1529"),sQuery(id+"F0.wireOp",EDGE,"E0.sketch_text.stroke-1530"),sQuery(id+"F0.wireOp",EDGE,"E0.sketch_text.stroke-1531"),sQuery(id+"F0.wireOp",EDGE,"E0.sketch_text.stroke-1532"),sQuery(id+"F0.wireOp",EDGE,"E0.sketch_text.stroke-1533"),sQuery(id+"F0.wireOp",EDGE,"E0.sketch_text.stroke-1534"),sQuery(id+"F0.wireOp",EDGE,"E0.sketch_text.stroke-1535"),sQuery(id+"F0.wireOp",EDGE,"E0.sketch_text.stroke-1536"),sQuery(id+"F0.wireOp",EDGE,"E0.sketch_text.stroke-1537")])]});
            var Q85;
            Q85=makeQuery(id+"F2.opExtrude","SWEPT_BODY",BODY,{"disambiguationData":[OSD([sQuery(id+"F0.wireOp",EDGE,"E0.sketch_text.stroke-1538"),sQuery(id+"F0.wireOp",EDGE,"E0.sketch_text.stroke-1539"),sQuery(id+"F0.wireOp",EDGE,"E0.sketch_text.stroke-1540"),sQuery(id+"F0.wireOp",EDGE,"E0.sketch_text.stroke-1541"),sQuery(id+"F0.wireOp",EDGE,"E0.sketch_text.stroke-1542"),sQuery(id+"F0.wireOp",EDGE,"E0.sketch_text.stroke-1543"),sQuery(id+"F0.wireOp",EDGE,"E0.sketch_text.stroke-1544"),sQuery(id+"F0.wireOp",EDGE,"E0.sketch_text.stroke-1545"),sQuery(id+"F0.wireOp",EDGE,"E0.sketch_text.stroke-1546"),sQuery(id+"F0.wireOp",EDGE,"E0.sketch_text.stroke-1547"),sQuery(id+"F0.wireOp",EDGE,"E0.sketch_text.stroke-1548"),sQuery(id+"F0.wireOp",EDGE,"E0.sketch_text.stroke-1549"),sQuery(id+"F0.wireOp",EDGE,"E0.sketch_text.stroke-1550"),sQuery(id+"F0.wireOp",EDGE,"E0.sketch_text.stroke-1551"),sQuery(id+"F0.wireOp",EDGE,"E0.sketch_text.stroke-1552"),sQuery(id+"F0.wireOp",EDGE,"E0.sketch_text.stroke-1553"),sQuery(id+"F0.wireOp",EDGE,"E0.sketch_text.stroke-1554"),sQuery(id+"F0.wireOp",EDGE,"E0.sketch_text.stroke-1555"),sQuery(id+"F0.wireOp",EDGE,"E0.sketch_text.stroke-1556")])]});
            var Q86;
            Q86=makeQuery(id+"F2.opExtrude","SWEPT_BODY",BODY,{"disambiguationData":[OSD([sQuery(id+"F0.wireOp",EDGE,"E0.sketch_text.stroke-1557"),sQuery(id+"F0.wireOp",EDGE,"E0.sketch_text.stroke-1558"),sQuery(id+"F0.wireOp",EDGE,"E0.sketch_text.stroke-1559"),sQuery(id+"F0.wireOp",EDGE,"E0.sketch_text.stroke-1560"),sQuery(id+"F0.wireOp",EDGE,"E0.sketch_text.stroke-1561"),sQuery(id+"F0.wireOp",EDGE,"E0.sketch_text.stroke-1562"),sQuery(id+"F0.wireOp",EDGE,"E0.sketch_text.stroke-1563"),sQuery(id+"F0.wireOp",EDGE,"E0.sketch_text.stroke-1564"),sQuery(id+"F0.wireOp",EDGE,"E0.sketch_text.stroke-1565"),sQuery(id+"F0.wireOp",EDGE,"E0.sketch_text.stroke-1566"),sQuery(id+"F0.wireOp",EDGE,"E0.sketch_text.stroke-1567"),sQuery(id+"F0.wireOp",EDGE,"E0.sketch_text.stroke-1568"),sQuery(id+"F0.wireOp",EDGE,"E0.sketch_text.stroke-1569")])]});
            var Q87;
            Q87=makeQuery(id+"F2.opExtrude","SWEPT_BODY",BODY,{"disambiguationData":[OSD([sQuery(id+"F0.wireOp",EDGE,"E0.sketch_text.stroke-1570"),sQuery(id+"F0.wireOp",EDGE,"E0.sketch_text.stroke-1571"),sQuery(id+"F0.wireOp",EDGE,"E0.sketch_text.stroke-1572"),sQuery(id+"F0.wireOp",EDGE,"E0.sketch_text.stroke-1573")])]});
            var Q88;
            Q88=makeQuery(id+"F2.opExtrude","SWEPT_BODY",BODY,{"disambiguationData":[OSD([sQuery(id+"F0.wireOp",EDGE,"E0.sketch_text.stroke-1574"),sQuery(id+"F0.wireOp",EDGE,"E0.sketch_text.stroke-1575"),sQuery(id+"F0.wireOp",EDGE,"E0.sketch_text.stroke-1576"),sQuery(id+"F0.wireOp",EDGE,"E0.sketch_text.stroke-1577")])]});
            var Q89;
            Q89=makeQuery(id+"F2.opExtrude","SWEPT_BODY",BODY,{"disambiguationData":[OSD([sQuery(id+"F0.wireOp",EDGE,"E0.sketch_text.stroke-1678"),sQuery(id+"F0.wireOp",EDGE,"E0.sketch_text.stroke-1679"),sQuery(id+"F0.wireOp",EDGE,"E0.sketch_text.stroke-1680"),sQuery(id+"F0.wireOp",EDGE,"E0.sketch_text.stroke-1681")])]});
            var Q90;
            Q90=makeQuery(id+"F2.opExtrude","SWEPT_BODY",BODY,{"disambiguationData":[OSD([sQuery(id+"F0.wireOp",EDGE,"E0.sketch_text.stroke-1586"),sQuery(id+"F0.wireOp",EDGE,"E0.sketch_text.stroke-1587"),sQuery(id+"F0.wireOp",EDGE,"E0.sketch_text.stroke-1588"),sQuery(id+"F0.wireOp",EDGE,"E0.sketch_text.stroke-1589"),sQuery(id+"F0.wireOp",EDGE,"E0.sketch_text.stroke-1590"),sQuery(id+"F0.wireOp",EDGE,"E0.sketch_text.stroke-1591"),sQuery(id+"F0.wireOp",EDGE,"E0.sketch_text.stroke-1592"),sQuery(id+"F0.wireOp",EDGE,"E0.sketch_text.stroke-1593"),sQuery(id+"F0.wireOp",EDGE,"E0.sketch_text.stroke-1594"),sQuery(id+"F0.wireOp",EDGE,"E0.sketch_text.stroke-1595"),sQuery(id+"F0.wireOp",EDGE,"E0.sketch_text.stroke-1596"),sQuery(id+"F0.wireOp",EDGE,"E0.sketch_text.stroke-1597"),sQuery(id+"F0.wireOp",EDGE,"E0.sketch_text.stroke-1598"),sQuery(id+"F0.wireOp",EDGE,"E0.sketch_text.stroke-1599"),sQuery(id+"F0.wireOp",EDGE,"E0.sketch_text.stroke-1600")])]});
            var Q91;
            Q91=makeQuery(id+"F2.opExtrude","SWEPT_BODY",BODY,{"disambiguationData":[OSD([sQuery(id+"F0.wireOp",EDGE,"E0.sketch_text.stroke-1601"),sQuery(id+"F0.wireOp",EDGE,"E0.sketch_text.stroke-1602"),sQuery(id+"F0.wireOp",EDGE,"E0.sketch_text.stroke-1603"),sQuery(id+"F0.wireOp",EDGE,"E0.sketch_text.stroke-1604"),sQuery(id+"F0.wireOp",EDGE,"E0.sketch_text.stroke-1605"),sQuery(id+"F0.wireOp",EDGE,"E0.sketch_text.stroke-1606"),sQuery(id+"F0.wireOp",EDGE,"E0.sketch_text.stroke-1607"),sQuery(id+"F0.wireOp",EDGE,"E0.sketch_text.stroke-1608"),sQuery(id+"F0.wireOp",EDGE,"E0.sketch_text.stroke-1609"),sQuery(id+"F0.wireOp",EDGE,"E0.sketch_text.stroke-1610"),sQuery(id+"F0.wireOp",EDGE,"E0.sketch_text.stroke-1611"),sQuery(id+"F0.wireOp",EDGE,"E0.sketch_text.stroke-1612"),sQuery(id+"F0.wireOp",EDGE,"E0.sketch_text.stroke-1613"),sQuery(id+"F0.wireOp",EDGE,"E0.sketch_text.stroke-1614"),sQuery(id+"F0.wireOp",EDGE,"E0.sketch_text.stroke-1615"),sQuery(id+"F0.wireOp",EDGE,"E0.sketch_text.stroke-1616"),sQuery(id+"F0.wireOp",EDGE,"E0.sketch_text.stroke-1617"),sQuery(id+"F0.wireOp",EDGE,"E0.sketch_text.stroke-1618"),sQuery(id+"F0.wireOp",EDGE,"E0.sketch_text.stroke-1619")])]});
            var Q92;
            Q92=makeQuery(id+"F2.opExtrude","SWEPT_BODY",BODY,{"disambiguationData":[OSD([sQuery(id+"F0.wireOp",EDGE,"E0.sketch_text.stroke-1620"),sQuery(id+"F0.wireOp",EDGE,"E0.sketch_text.stroke-1621"),sQuery(id+"F0.wireOp",EDGE,"E0.sketch_text.stroke-1622"),sQuery(id+"F0.wireOp",EDGE,"E0.sketch_text.stroke-1623"),sQuery(id+"F0.wireOp",EDGE,"E0.sketch_text.stroke-1624"),sQuery(id+"F0.wireOp",EDGE,"E0.sketch_text.stroke-1625"),sQuery(id+"F0.wireOp",EDGE,"E0.sketch_text.stroke-1626"),sQuery(id+"F0.wireOp",EDGE,"E0.sketch_text.stroke-1627"),sQuery(id+"F0.wireOp",EDGE,"E0.sketch_text.stroke-1628"),sQuery(id+"F0.wireOp",EDGE,"E0.sketch_text.stroke-1629"),sQuery(id+"F0.wireOp",EDGE,"E0.sketch_text.stroke-1630"),sQuery(id+"F0.wireOp",EDGE,"E0.sketch_text.stroke-1631"),sQuery(id+"F0.wireOp",EDGE,"E0.sketch_text.stroke-1632"),sQuery(id+"F0.wireOp",EDGE,"E0.sketch_text.stroke-1633"),sQuery(id+"F0.wireOp",EDGE,"E0.sketch_text.stroke-1634"),sQuery(id+"F0.wireOp",EDGE,"E0.sketch_text.stroke-1635"),sQuery(id+"F0.wireOp",EDGE,"E0.sketch_text.stroke-1636"),sQuery(id+"F0.wireOp",EDGE,"E0.sketch_text.stroke-1637"),sQuery(id+"F0.wireOp",EDGE,"E0.sketch_text.stroke-1638"),sQuery(id+"F0.wireOp",EDGE,"E0.sketch_text.stroke-1639"),sQuery(id+"F0.wireOp",EDGE,"E0.sketch_text.stroke-1640"),sQuery(id+"F0.wireOp",EDGE,"E0.sketch_text.stroke-1641"),sQuery(id+"F0.wireOp",EDGE,"E0.sketch_text.stroke-1642"),sQuery(id+"F0.wireOp",EDGE,"E0.sketch_text.stroke-1643"),sQuery(id+"F0.wireOp",EDGE,"E0.sketch_text.stroke-1644"),sQuery(id+"F0.wireOp",EDGE,"E0.sketch_text.stroke-1645"),sQuery(id+"F0.wireOp",EDGE,"E0.sketch_text.stroke-1646"),sQuery(id+"F0.wireOp",EDGE,"E0.sketch_text.stroke-1647")])]});
            var Q93;
            Q93=makeQuery(id+"F2.opExtrude","SWEPT_BODY",BODY,{"disambiguationData":[OSD([sQuery(id+"F0.wireOp",EDGE,"E0.sketch_text.stroke-1656"),sQuery(id+"F0.wireOp",EDGE,"E0.sketch_text.stroke-1657"),sQuery(id+"F0.wireOp",EDGE,"E0.sketch_text.stroke-1658"),sQuery(id+"F0.wireOp",EDGE,"E0.sketch_text.stroke-1659"),sQuery(id+"F0.wireOp",EDGE,"E0.sketch_text.stroke-1660"),sQuery(id+"F0.wireOp",EDGE,"E0.sketch_text.stroke-1661"),sQuery(id+"F0.wireOp",EDGE,"E0.sketch_text.stroke-1662"),sQuery(id+"F0.wireOp",EDGE,"E0.sketch_text.stroke-1663"),sQuery(id+"F0.wireOp",EDGE,"E0.sketch_text.stroke-1664"),sQuery(id+"F0.wireOp",EDGE,"E0.sketch_text.stroke-1665"),sQuery(id+"F0.wireOp",EDGE,"E0.sketch_text.stroke-1666"),sQuery(id+"F0.wireOp",EDGE,"E0.sketch_text.stroke-1667"),sQuery(id+"F0.wireOp",EDGE,"E0.sketch_text.stroke-1668"),sQuery(id+"F0.wireOp",EDGE,"E0.sketch_text.stroke-1669"),sQuery(id+"F0.wireOp",EDGE,"E0.sketch_text.stroke-1670"),sQuery(id+"F0.wireOp",EDGE,"E0.sketch_text.stroke-1671")])]});
            var Q94;
            Q94=makeQuery(id+"F2.opExtrude","SWEPT_BODY",BODY,{"disambiguationData":[OSD([sQuery(id+"F0.wireOp",EDGE,"E0.sketch_text.stroke-1724"),sQuery(id+"F0.wireOp",EDGE,"E0.sketch_text.stroke-1725"),sQuery(id+"F0.wireOp",EDGE,"E0.sketch_text.stroke-1726"),sQuery(id+"F0.wireOp",EDGE,"E0.sketch_text.stroke-1727"),sQuery(id+"F0.wireOp",EDGE,"E0.sketch_text.stroke-1728"),sQuery(id+"F0.wireOp",EDGE,"E0.sketch_text.stroke-1729"),sQuery(id+"F0.wireOp",EDGE,"E0.sketch_text.stroke-1730"),sQuery(id+"F0.wireOp",EDGE,"E0.sketch_text.stroke-1731"),sQuery(id+"F0.wireOp",EDGE,"E0.sketch_text.stroke-1732"),sQuery(id+"F0.wireOp",EDGE,"E0.sketch_text.stroke-1733"),sQuery(id+"F0.wireOp",EDGE,"E0.sketch_text.stroke-1734"),sQuery(id+"F0.wireOp",EDGE,"E0.sketch_text.stroke-1735"),sQuery(id+"F0.wireOp",EDGE,"E0.sketch_text.stroke-1736"),sQuery(id+"F0.wireOp",EDGE,"E0.sketch_text.stroke-1737"),sQuery(id+"F0.wireOp",EDGE,"E0.sketch_text.stroke-1738"),sQuery(id+"F0.wireOp",EDGE,"E0.sketch_text.stroke-1739"),sQuery(id+"F0.wireOp",EDGE,"E0.sketch_text.stroke-1740")])]});
            var Q95;
            Q95=makeQuery(id+"F2.opExtrude","SWEPT_BODY",BODY,{"disambiguationData":[OSD([sQuery(id+"F0.wireOp",EDGE,"E0.sketch_text.stroke-1672"),sQuery(id+"F0.wireOp",EDGE,"E0.sketch_text.stroke-1673"),sQuery(id+"F0.wireOp",EDGE,"E0.sketch_text.stroke-1674"),sQuery(id+"F0.wireOp",EDGE,"E0.sketch_text.stroke-1675"),sQuery(id+"F0.wireOp",EDGE,"E0.sketch_text.stroke-1676"),sQuery(id+"F0.wireOp",EDGE,"E0.sketch_text.stroke-1677")])]});
            var Q96;
            Q96=makeQuery(id+"F2.opExtrude","SWEPT_BODY",BODY,{"disambiguationData":[OSD([sQuery(id+"F0.wireOp",EDGE,"E0.sketch_text.stroke-632"),sQuery(id+"F0.wireOp",EDGE,"E0.sketch_text.stroke-633"),sQuery(id+"F0.wireOp",EDGE,"E0.sketch_text.stroke-634"),sQuery(id+"F0.wireOp",EDGE,"E0.sketch_text.stroke-635"),sQuery(id+"F0.wireOp",EDGE,"E0.sketch_text.stroke-636"),sQuery(id+"F0.wireOp",EDGE,"E0.sketch_text.stroke-637"),sQuery(id+"F0.wireOp",EDGE,"E0.sketch_text.stroke-638"),sQuery(id+"F0.wireOp",EDGE,"E0.sketch_text.stroke-639"),sQuery(id+"F0.wireOp",EDGE,"E0.sketch_text.stroke-640"),sQuery(id+"F0.wireOp",EDGE,"E0.sketch_text.stroke-641"),sQuery(id+"F0.wireOp",EDGE,"E0.sketch_text.stroke-642"),sQuery(id+"F0.wireOp",EDGE,"E0.sketch_text.stroke-643"),sQuery(id+"F0.wireOp",EDGE,"E0.sketch_text.stroke-644"),sQuery(id+"F0.wireOp",EDGE,"E0.sketch_text.stroke-645"),sQuery(id+"F0.wireOp",EDGE,"E0.sketch_text.stroke-646"),sQuery(id+"F0.wireOp",EDGE,"E0.sketch_text.stroke-647"),sQuery(id+"F0.wireOp",EDGE,"E0.sketch_text.stroke-648")])]});
            var Q97;
            Q97=makeQuery(id+"F2.opExtrude","SWEPT_BODY",BODY,{"disambiguationData":[OSD([sQuery(id+"F0.wireOp",EDGE,"E0.sketch_text.stroke-649"),sQuery(id+"F0.wireOp",EDGE,"E0.sketch_text.stroke-650"),sQuery(id+"F0.wireOp",EDGE,"E0.sketch_text.stroke-651"),sQuery(id+"F0.wireOp",EDGE,"E0.sketch_text.stroke-652")])]});
            var Q98;
            Q98=makeQuery(id+"F2.opExtrude","SWEPT_BODY",BODY,{"disambiguationData":[OSD([sQuery(id+"F0.wireOp",EDGE,"E0.sketch_text.stroke-653"),sQuery(id+"F0.wireOp",EDGE,"E0.sketch_text.stroke-654"),sQuery(id+"F0.wireOp",EDGE,"E0.sketch_text.stroke-655"),sQuery(id+"F0.wireOp",EDGE,"E0.sketch_text.stroke-656"),sQuery(id+"F0.wireOp",EDGE,"E0.sketch_text.stroke-657"),sQuery(id+"F0.wireOp",EDGE,"E0.sketch_text.stroke-658"),sQuery(id+"F0.wireOp",EDGE,"E0.sketch_text.stroke-659"),sQuery(id+"F0.wireOp",EDGE,"E0.sketch_text.stroke-660"),sQuery(id+"F0.wireOp",EDGE,"E0.sketch_text.stroke-661"),sQuery(id+"F0.wireOp",EDGE,"E0.sketch_text.stroke-662"),sQuery(id+"F0.wireOp",EDGE,"E0.sketch_text.stroke-663"),sQuery(id+"F0.wireOp",EDGE,"E0.sketch_text.stroke-664"),sQuery(id+"F0.wireOp",EDGE,"E0.sketch_text.stroke-665"),sQuery(id+"F0.wireOp",EDGE,"E0.sketch_text.stroke-666"),sQuery(id+"F0.wireOp",EDGE,"E0.sketch_text.stroke-667"),sQuery(id+"F0.wireOp",EDGE,"E0.sketch_text.stroke-668"),sQuery(id+"F0.wireOp",EDGE,"E0.sketch_text.stroke-669")])]});
            var Q99;
            Q99=makeQuery(id+"F2.opExtrude","SWEPT_BODY",BODY,{"disambiguationData":[OSD([sQuery(id+"F0.wireOp",EDGE,"E0.sketch_text.stroke-670"),sQuery(id+"F0.wireOp",EDGE,"E0.sketch_text.stroke-671"),sQuery(id+"F0.wireOp",EDGE,"E0.sketch_text.stroke-672"),sQuery(id+"F0.wireOp",EDGE,"E0.sketch_text.stroke-673"),sQuery(id+"F0.wireOp",EDGE,"E0.sketch_text.stroke-674"),sQuery(id+"F0.wireOp",EDGE,"E0.sketch_text.stroke-675"),sQuery(id+"F0.wireOp",EDGE,"E0.sketch_text.stroke-676"),sQuery(id+"F0.wireOp",EDGE,"E0.sketch_text.stroke-677"),sQuery(id+"F0.wireOp",EDGE,"E0.sketch_text.stroke-678"),sQuery(id+"F0.wireOp",EDGE,"E0.sketch_text.stroke-679"),sQuery(id+"F0.wireOp",EDGE,"E0.sketch_text.stroke-680"),sQuery(id+"F0.wireOp",EDGE,"E0.sketch_text.stroke-681"),sQuery(id+"F0.wireOp",EDGE,"E0.sketch_text.stroke-682"),sQuery(id+"F0.wireOp",EDGE,"E0.sketch_text.stroke-683"),sQuery(id+"F0.wireOp",EDGE,"E0.sketch_text.stroke-684"),sQuery(id+"F0.wireOp",EDGE,"E0.sketch_text.stroke-685"),sQuery(id+"F0.wireOp",EDGE,"E0.sketch_text.stroke-686"),sQuery(id+"F0.wireOp",EDGE,"E0.sketch_text.stroke-687")])]});
            var Q100;
            Q100=makeQuery(id+"F2.opExtrude","SWEPT_BODY",BODY,{"disambiguationData":[OSD([sQuery(id+"F0.wireOp",EDGE,"E0.sketch_text.stroke-688"),sQuery(id+"F0.wireOp",EDGE,"E0.sketch_text.stroke-689"),sQuery(id+"F0.wireOp",EDGE,"E0.sketch_text.stroke-690"),sQuery(id+"F0.wireOp",EDGE,"E0.sketch_text.stroke-691"),sQuery(id+"F0.wireOp",EDGE,"E0.sketch_text.stroke-692"),sQuery(id+"F0.wireOp",EDGE,"E0.sketch_text.stroke-693"),sQuery(id+"F0.wireOp",EDGE,"E0.sketch_text.stroke-694"),sQuery(id+"F0.wireOp",EDGE,"E0.sketch_text.stroke-695"),sQuery(id+"F0.wireOp",EDGE,"E0.sketch_text.stroke-696"),sQuery(id+"F0.wireOp",EDGE,"E0.sketch_text.stroke-697"),sQuery(id+"F0.wireOp",EDGE,"E0.sketch_text.stroke-698"),sQuery(id+"F0.wireOp",EDGE,"E0.sketch_text.stroke-699"),sQuery(id+"F0.wireOp",EDGE,"E0.sketch_text.stroke-700"),sQuery(id+"F0.wireOp",EDGE,"E0.sketch_text.stroke-701"),sQuery(id+"F0.wireOp",EDGE,"E0.sketch_text.stroke-702"),sQuery(id+"F0.wireOp",EDGE,"E0.sketch_text.stroke-703"),sQuery(id+"F0.wireOp",EDGE,"E0.sketch_text.stroke-704")])]});
            var Q101;
            Q101=makeQuery(id+"F2.opExtrude","SWEPT_BODY",BODY,{"disambiguationData":[OSD([sQuery(id+"F0.wireOp",EDGE,"E0.sketch_text.stroke-705"),sQuery(id+"F0.wireOp",EDGE,"E0.sketch_text.stroke-706"),sQuery(id+"F0.wireOp",EDGE,"E0.sketch_text.stroke-707"),sQuery(id+"F0.wireOp",EDGE,"E0.sketch_text.stroke-708"),sQuery(id+"F0.wireOp",EDGE,"E0.sketch_text.stroke-709"),sQuery(id+"F0.wireOp",EDGE,"E0.sketch_text.stroke-710"),sQuery(id+"F0.wireOp",EDGE,"E0.sketch_text.stroke-711"),sQuery(id+"F0.wireOp",EDGE,"E0.sketch_text.stroke-712"),sQuery(id+"F0.wireOp",EDGE,"E0.sketch_text.stroke-713"),sQuery(id+"F0.wireOp",EDGE,"E0.sketch_text.stroke-714"),sQuery(id+"F0.wireOp",EDGE,"E0.sketch_text.stroke-715"),sQuery(id+"F0.wireOp",EDGE,"E0.sketch_text.stroke-716"),sQuery(id+"F0.wireOp",EDGE,"E0.sketch_text.stroke-717"),sQuery(id+"F0.wireOp",EDGE,"E0.sketch_text.stroke-718"),sQuery(id+"F0.wireOp",EDGE,"E0.sketch_text.stroke-719"),sQuery(id+"F0.wireOp",EDGE,"E0.sketch_text.stroke-720"),sQuery(id+"F0.wireOp",EDGE,"E0.sketch_text.stroke-721"),sQuery(id+"F0.wireOp",EDGE,"E0.sketch_text.stroke-722"),sQuery(id+"F0.wireOp",EDGE,"E0.sketch_text.stroke-723"),sQuery(id+"F0.wireOp",EDGE,"E0.sketch_text.stroke-724"),sQuery(id+"F0.wireOp",EDGE,"E0.sketch_text.stroke-725"),sQuery(id+"F0.wireOp",EDGE,"E0.sketch_text.stroke-726"),sQuery(id+"F0.wireOp",EDGE,"E0.sketch_text.stroke-727"),sQuery(id+"F0.wireOp",EDGE,"E0.sketch_text.stroke-728")])]});
            var Q102;
            Q102=makeQuery(id+"F2.opExtrude","SWEPT_BODY",BODY,{"disambiguationData":[OSD([sQuery(id+"F0.wireOp",EDGE,"E0.sketch_text.stroke-729"),sQuery(id+"F0.wireOp",EDGE,"E0.sketch_text.stroke-730"),sQuery(id+"F0.wireOp",EDGE,"E0.sketch_text.stroke-731"),sQuery(id+"F0.wireOp",EDGE,"E0.sketch_text.stroke-732"),sQuery(id+"F0.wireOp",EDGE,"E0.sketch_text.stroke-733"),sQuery(id+"F0.wireOp",EDGE,"E0.sketch_text.stroke-734"),sQuery(id+"F0.wireOp",EDGE,"E0.sketch_text.stroke-735"),sQuery(id+"F0.wireOp",EDGE,"E0.sketch_text.stroke-736"),sQuery(id+"F0.wireOp",EDGE,"E0.sketch_text.stroke-737"),sQuery(id+"F0.wireOp",EDGE,"E0.sketch_text.stroke-738"),sQuery(id+"F0.wireOp",EDGE,"E0.sketch_text.stroke-739"),sQuery(id+"F0.wireOp",EDGE,"E0.sketch_text.stroke-740"),sQuery(id+"F0.wireOp",EDGE,"E0.sketch_text.stroke-741"),sQuery(id+"F0.wireOp",EDGE,"E0.sketch_text.stroke-742"),sQuery(id+"F0.wireOp",EDGE,"E0.sketch_text.stroke-743"),sQuery(id+"F0.wireOp",EDGE,"E0.sketch_text.stroke-744"),sQuery(id+"F0.wireOp",EDGE,"E0.sketch_text.stroke-745"),sQuery(id+"F0.wireOp",EDGE,"E0.sketch_text.stroke-746"),sQuery(id+"F0.wireOp",EDGE,"E0.sketch_text.stroke-747")])]});
            var Q103;
            Q103=makeQuery(id+"F2.opExtrude","SWEPT_BODY",BODY,{"disambiguationData":[OSD([sQuery(id+"F0.wireOp",EDGE,"E0.sketch_text.stroke-748"),sQuery(id+"F0.wireOp",EDGE,"E0.sketch_text.stroke-749"),sQuery(id+"F0.wireOp",EDGE,"E0.sketch_text.stroke-750"),sQuery(id+"F0.wireOp",EDGE,"E0.sketch_text.stroke-751")])]});
            var Q104;
            Q104=makeQuery(id+"F2.opExtrude","SWEPT_BODY",BODY,{"disambiguationData":[OSD([sQuery(id+"F0.wireOp",EDGE,"E0.sketch_text.stroke-752"),sQuery(id+"F0.wireOp",EDGE,"E0.sketch_text.stroke-753"),sQuery(id+"F0.wireOp",EDGE,"E0.sketch_text.stroke-754"),sQuery(id+"F0.wireOp",EDGE,"E0.sketch_text.stroke-755")])]});
            var Q105;
            Q105=makeQuery(id+"F2.opExtrude","SWEPT_BODY",BODY,{"disambiguationData":[OSD([sQuery(id+"F0.wireOp",EDGE,"E0.sketch_text.stroke-756"),sQuery(id+"F0.wireOp",EDGE,"E0.sketch_text.stroke-757"),sQuery(id+"F0.wireOp",EDGE,"E0.sketch_text.stroke-758"),sQuery(id+"F0.wireOp",EDGE,"E0.sketch_text.stroke-759")])]});
            var Q106;
            Q106=makeQuery(id+"F2.opExtrude","SWEPT_BODY",BODY,{"disambiguationData":[OSD([sQuery(id+"F0.wireOp",EDGE,"E0.sketch_text.stroke-1018"),sQuery(id+"F0.wireOp",EDGE,"E0.sketch_text.stroke-1019"),sQuery(id+"F0.wireOp",EDGE,"E0.sketch_text.stroke-1020"),sQuery(id+"F0.wireOp",EDGE,"E0.sketch_text.stroke-1021")])]});
            var Q107;
            Q107=makeQuery(id+"F2.opExtrude","SWEPT_BODY",BODY,{"disambiguationData":[OSD([sQuery(id+"F0.wireOp",EDGE,"E0.sketch_text.stroke-1026"),sQuery(id+"F0.wireOp",EDGE,"E0.sketch_text.stroke-1027"),sQuery(id+"F0.wireOp",EDGE,"E0.sketch_text.stroke-1028"),sQuery(id+"F0.wireOp",EDGE,"E0.sketch_text.stroke-1029")])]});
            var Q108;
            Q108=makeQuery(id+"F2.opExtrude","SWEPT_BODY",BODY,{"disambiguationData":[OSD([sQuery(id+"F0.wireOp",EDGE,"E0.sketch_text.stroke-1077"),sQuery(id+"F0.wireOp",EDGE,"E0.sketch_text.stroke-1078"),sQuery(id+"F0.wireOp",EDGE,"E0.sketch_text.stroke-1079"),sQuery(id+"F0.wireOp",EDGE,"E0.sketch_text.stroke-1080")])]});
            var Q109;
            Q109=makeQuery(id+"F2.opExtrude","SWEPT_BODY",BODY,{"disambiguationData":[OSD([sQuery(id+"F0.wireOp",EDGE,"E0.sketch_text.stroke-1189"),sQuery(id+"F0.wireOp",EDGE,"E0.sketch_text.stroke-1190"),sQuery(id+"F0.wireOp",EDGE,"E0.sketch_text.stroke-1191"),sQuery(id+"F0.wireOp",EDGE,"E0.sketch_text.stroke-1192"),sQuery(id+"F0.wireOp",EDGE,"E0.sketch_text.stroke-1193"),sQuery(id+"F0.wireOp",EDGE,"E0.sketch_text.stroke-1194"),sQuery(id+"F0.wireOp",EDGE,"E0.sketch_text.stroke-1195"),sQuery(id+"F0.wireOp",EDGE,"E0.sketch_text.stroke-1196"),sQuery(id+"F0.wireOp",EDGE,"E0.sketch_text.stroke-1197"),sQuery(id+"F0.wireOp",EDGE,"E0.sketch_text.stroke-1198"),sQuery(id+"F0.wireOp",EDGE,"E0.sketch_text.stroke-1199"),sQuery(id+"F0.wireOp",EDGE,"E0.sketch_text.stroke-1200"),sQuery(id+"F0.wireOp",EDGE,"E0.sketch_text.stroke-1201")])]});
            var Q110;
            Q110=makeQuery(id+"F2.opExtrude","SWEPT_BODY",BODY,{"disambiguationData":[OSD([sQuery(id+"F0.wireOp",EDGE,"E0.sketch_text.stroke-1267"),sQuery(id+"F0.wireOp",EDGE,"E0.sketch_text.stroke-1268"),sQuery(id+"F0.wireOp",EDGE,"E0.sketch_text.stroke-1269"),sQuery(id+"F0.wireOp",EDGE,"E0.sketch_text.stroke-1270")])]});
            var Q111;
            Q111=makeQuery(id+"F2.opExtrude","SWEPT_BODY",BODY,{"disambiguationData":[OSD([sQuery(id+"F0.wireOp",EDGE,"E0.sketch_text.stroke-1578"),sQuery(id+"F0.wireOp",EDGE,"E0.sketch_text.stroke-1579"),sQuery(id+"F0.wireOp",EDGE,"E0.sketch_text.stroke-1580"),sQuery(id+"F0.wireOp",EDGE,"E0.sketch_text.stroke-1581"),sQuery(id+"F0.wireOp",EDGE,"E0.sketch_text.stroke-1582"),sQuery(id+"F0.wireOp",EDGE,"E0.sketch_text.stroke-1583"),sQuery(id+"F0.wireOp",EDGE,"E0.sketch_text.stroke-1584"),sQuery(id+"F0.wireOp",EDGE,"E0.sketch_text.stroke-1585")])]});
            var Q112;
            Q112=makeQuery(id+"F2.opExtrude","SWEPT_BODY",BODY,{"disambiguationData":[OSD([sQuery(id+"F0.wireOp",EDGE,"E0.sketch_text.stroke-1648"),sQuery(id+"F0.wireOp",EDGE,"E0.sketch_text.stroke-1649"),sQuery(id+"F0.wireOp",EDGE,"E0.sketch_text.stroke-1650"),sQuery(id+"F0.wireOp",EDGE,"E0.sketch_text.stroke-1651"),sQuery(id+"F0.wireOp",EDGE,"E0.sketch_text.stroke-1652"),sQuery(id+"F0.wireOp",EDGE,"E0.sketch_text.stroke-1653"),sQuery(id+"F0.wireOp",EDGE,"E0.sketch_text.stroke-1654"),sQuery(id+"F0.wireOp",EDGE,"E0.sketch_text.stroke-1655")])]});
            var Q113;
            Q113=makeQuery(id+"F2.opExtrude","SWEPT_BODY",BODY,{"disambiguationData":[OSD([sQuery(id+"F0.wireOp",EDGE,"E0.sketch_text.stroke-341"),sQuery(id+"F0.wireOp",EDGE,"E0.sketch_text.stroke-342"),sQuery(id+"F0.wireOp",EDGE,"E0.sketch_text.stroke-343"),sQuery(id+"F0.wireOp",EDGE,"E0.sketch_text.stroke-344"),sQuery(id+"F0.wireOp",EDGE,"E0.sketch_text.stroke-345"),sQuery(id+"F0.wireOp",EDGE,"E0.sketch_text.stroke-346"),sQuery(id+"F0.wireOp",EDGE,"E0.sketch_text.stroke-347"),sQuery(id+"F0.wireOp",EDGE,"E0.sketch_text.stroke-348"),sQuery(id+"F0.wireOp",EDGE,"E0.sketch_text.stroke-349"),sQuery(id+"F0.wireOp",EDGE,"E0.sketch_text.stroke-350"),sQuery(id+"F0.wireOp",EDGE,"E0.sketch_text.stroke-351"),sQuery(id+"F0.wireOp",EDGE,"E0.sketch_text.stroke-352"),sQuery(id+"F0.wireOp",EDGE,"E0.sketch_text.stroke-353")])]});
            var Q114;
            Q114=makeQuery(id+"F2.opExtrude","SWEPT_BODY",BODY,{"disambiguationData":[OSD([sQuery(id+"F0.wireOp",EDGE,"E0.sketch_text.stroke-199"),sQuery(id+"F0.wireOp",EDGE,"E0.sketch_text.stroke-200"),sQuery(id+"F0.wireOp",EDGE,"E0.sketch_text.stroke-201"),sQuery(id+"F0.wireOp",EDGE,"E0.sketch_text.stroke-202")])]});
            var Q115;
            Q115=makeQuery(id+"F2.opExtrude","SWEPT_BODY",BODY,{"disambiguationData":[OSD([sQuery(id+"F0.wireOp",EDGE,"E0.sketch_text.stroke-220"),sQuery(id+"F0.wireOp",EDGE,"E0.sketch_text.stroke-221"),sQuery(id+"F0.wireOp",EDGE,"E0.sketch_text.stroke-222"),sQuery(id+"F0.wireOp",EDGE,"E0.sketch_text.stroke-223"),sQuery(id+"F0.wireOp",EDGE,"E0.sketch_text.stroke-224"),sQuery(id+"F0.wireOp",EDGE,"E0.sketch_text.stroke-225"),sQuery(id+"F0.wireOp",EDGE,"E0.sketch_text.stroke-226"),sQuery(id+"F0.wireOp",EDGE,"E0.sketch_text.stroke-227"),sQuery(id+"F0.wireOp",EDGE,"E0.sketch_text.stroke-228"),sQuery(id+"F0.wireOp",EDGE,"E0.sketch_text.stroke-229"),sQuery(id+"F0.wireOp",EDGE,"E0.sketch_text.stroke-230"),sQuery(id+"F0.wireOp",EDGE,"E0.sketch_text.stroke-231"),sQuery(id+"F0.wireOp",EDGE,"E0.sketch_text.stroke-232")])]});
            var Q116;
            Q116=makeQuery(id+"F2.opExtrude","SWEPT_BODY",BODY,{"disambiguationData":[OSD([sQuery(id+"F0.wireOp",EDGE,"E0.sketch_text.stroke-564"),sQuery(id+"F0.wireOp",EDGE,"E0.sketch_text.stroke-565"),sQuery(id+"F0.wireOp",EDGE,"E0.sketch_text.stroke-566"),sQuery(id+"F0.wireOp",EDGE,"E0.sketch_text.stroke-567")])]});
            var Q117;
            Q117=makeQuery(id+"F2.opExtrude","SWEPT_BODY",BODY,{"disambiguationData":[OSD([sQuery(id+"F0.wireOp",EDGE,"E0.sketch_text.stroke-667"),sQuery(id+"F0.wireOp",EDGE,"E0.sketch_text.stroke-668"),sQuery(id+"F0.wireOp",EDGE,"E0.sketch_text.stroke-669"),sQuery(id+"F0.wireOp",EDGE,"E0.sketch_text.stroke-670")])]});
            var Q118;
            Q118=makeQuery(id+"F2.opExtrude","SWEPT_BODY",BODY,{"disambiguationData":[OSD([sQuery(id+"F0.wireOp",EDGE,"E0.sketch_text.stroke-671"),sQuery(id+"F0.wireOp",EDGE,"E0.sketch_text.stroke-672"),sQuery(id+"F0.wireOp",EDGE,"E0.sketch_text.stroke-673"),sQuery(id+"F0.wireOp",EDGE,"E0.sketch_text.stroke-674")])]});
            var Q119;
            Q119=makeQuery(id+"F2.opExtrude","SWEPT_BODY",BODY,{"disambiguationData":[OSD([sQuery(id+"F0.wireOp",EDGE,"E0.sketch_text.stroke-937"),sQuery(id+"F0.wireOp",EDGE,"E0.sketch_text.stroke-938"),sQuery(id+"F0.wireOp",EDGE,"E0.sketch_text.stroke-939"),sQuery(id+"F0.wireOp",EDGE,"E0.sketch_text.stroke-940")])]});
            var Q120;
            Q120=makeQuery(id+"F2.opExtrude","SWEPT_BODY",BODY,{"disambiguationData":[OSD([sQuery(id+"F0.wireOp",EDGE,"E0.sketch_text.stroke-1473"),sQuery(id+"F0.wireOp",EDGE,"E0.sketch_text.stroke-1474"),sQuery(id+"F0.wireOp",EDGE,"E0.sketch_text.stroke-1475"),sQuery(id+"F0.wireOp",EDGE,"E0.sketch_text.stroke-1476"),sQuery(id+"F0.wireOp",EDGE,"E0.sketch_text.stroke-1477"),sQuery(id+"F0.wireOp",EDGE,"E0.sketch_text.stroke-1478"),sQuery(id+"F0.wireOp",EDGE,"E0.sketch_text.stroke-1479"),sQuery(id+"F0.wireOp",EDGE,"E0.sketch_text.stroke-1480"),sQuery(id+"F0.wireOp",EDGE,"E0.sketch_text.stroke-1481"),sQuery(id+"F0.wireOp",EDGE,"E0.sketch_text.stroke-1482"),sQuery(id+"F0.wireOp",EDGE,"E0.sketch_text.stroke-1483"),sQuery(id+"F0.wireOp",EDGE,"E0.sketch_text.stroke-1484"),sQuery(id+"F0.wireOp",EDGE,"E0.sketch_text.stroke-1485")])]});
            var Q121;
            Q121=makeQuery(id+"F2.opExtrude","SWEPT_BODY",BODY,{"disambiguationData":[OSD([sQuery(id+"F0.wireOp",EDGE,"E0.sketch_text.stroke-1444"),sQuery(id+"F0.wireOp",EDGE,"E0.sketch_text.stroke-1445"),sQuery(id+"F0.wireOp",EDGE,"E0.sketch_text.stroke-1446"),sQuery(id+"F0.wireOp",EDGE,"E0.sketch_text.stroke-1447")])]});
            var Q122;
            Q122=makeQuery(id+"F2.opExtrude","SWEPT_BODY",BODY,{"disambiguationData":[OSD([sQuery(id+"F0.wireOp",EDGE,"E0.sketch_text.stroke-933"),sQuery(id+"F0.wireOp",EDGE,"E0.sketch_text.stroke-934"),sQuery(id+"F0.wireOp",EDGE,"E0.sketch_text.stroke-935"),sQuery(id+"F0.wireOp",EDGE,"E0.sketch_text.stroke-936")])]});
            var Q123;
            Q123=makeQuery(id+"F2.opExtrude","SWEPT_BODY",BODY,{"disambiguationData":[OSD([sQuery(id+"F0.wireOp",EDGE,"E0.sketch_text.stroke-884"),sQuery(id+"F0.wireOp",EDGE,"E0.sketch_text.stroke-885"),sQuery(id+"F0.wireOp",EDGE,"E0.sketch_text.stroke-886"),sQuery(id+"F0.wireOp",EDGE,"E0.sketch_text.stroke-887"),sQuery(id+"F0.wireOp",EDGE,"E0.sketch_text.stroke-888"),sQuery(id+"F0.wireOp",EDGE,"E0.sketch_text.stroke-889"),sQuery(id+"F0.wireOp",EDGE,"E0.sketch_text.stroke-890"),sQuery(id+"F0.wireOp",EDGE,"E0.sketch_text.stroke-891"),sQuery(id+"F0.wireOp",EDGE,"E0.sketch_text.stroke-892"),sQuery(id+"F0.wireOp",EDGE,"E0.sketch_text.stroke-893"),sQuery(id+"F0.wireOp",EDGE,"E0.sketch_text.stroke-894"),sQuery(id+"F0.wireOp",EDGE,"E0.sketch_text.stroke-895"),sQuery(id+"F0.wireOp",EDGE,"E0.sketch_text.stroke-896"),sQuery(id+"F0.wireOp",EDGE,"E0.sketch_text.stroke-897"),sQuery(id+"F0.wireOp",EDGE,"E0.sketch_text.stroke-898"),sQuery(id+"F0.wireOp",EDGE,"E0.sketch_text.stroke-899"),sQuery(id+"F0.wireOp",EDGE,"E0.sketch_text.stroke-900")])]});
            var Q124;
            Q124=makeQuery(id+"F2.opExtrude","SWEPT_BODY",BODY,{"disambiguationData":[OSD([sQuery(id+"F0.wireOp",EDGE,"E0.sketch_text.stroke-992"),sQuery(id+"F0.wireOp",EDGE,"E0.sketch_text.stroke-993"),sQuery(id+"F0.wireOp",EDGE,"E0.sketch_text.stroke-994"),sQuery(id+"F0.wireOp",EDGE,"E0.sketch_text.stroke-995")])]});
            var Q125;
            Q125=makeQuery(id+"F2.opExtrude","SWEPT_BODY",BODY,{"disambiguationData":[OSD([sQuery(id+"F0.wireOp",EDGE,"E0.sketch_text.stroke-982"),sQuery(id+"F0.wireOp",EDGE,"E0.sketch_text.stroke-983"),sQuery(id+"F0.wireOp",EDGE,"E0.sketch_text.stroke-984"),sQuery(id+"F0.wireOp",EDGE,"E0.sketch_text.stroke-985")])]});
            var Q126;
            Q126=makeQuery(id+"F2.opExtrude","SWEPT_BODY",BODY,{"disambiguationData":[OSD([sQuery(id+"F0.wireOp",EDGE,"E0.sketch_text.stroke-1370"),sQuery(id+"F0.wireOp",EDGE,"E0.sketch_text.stroke-1371"),sQuery(id+"F0.wireOp",EDGE,"E0.sketch_text.stroke-1372"),sQuery(id+"F0.wireOp",EDGE,"E0.sketch_text.stroke-1373"),sQuery(id+"F0.wireOp",EDGE,"E0.sketch_text.stroke-1374"),sQuery(id+"F0.wireOp",EDGE,"E0.sketch_text.stroke-1375"),sQuery(id+"F0.wireOp",EDGE,"E0.sketch_text.stroke-1376"),sQuery(id+"F0.wireOp",EDGE,"E0.sketch_text.stroke-1377"),sQuery(id+"F0.wireOp",EDGE,"E0.sketch_text.stroke-1378"),sQuery(id+"F0.wireOp",EDGE,"E0.sketch_text.stroke-1379")])]});
            var Q127;
            Q127=makeQuery(id+"F2.opExtrude","SWEPT_BODY",BODY,{"disambiguationData":[OSD([sQuery(id+"F0.wireOp",EDGE,"E0.sketch_text.stroke-1238"),sQuery(id+"F0.wireOp",EDGE,"E0.sketch_text.stroke-1239"),sQuery(id+"F0.wireOp",EDGE,"E0.sketch_text.stroke-1240"),sQuery(id+"F0.wireOp",EDGE,"E0.sketch_text.stroke-1241"),sQuery(id+"F0.wireOp",EDGE,"E0.sketch_text.stroke-1242"),sQuery(id+"F0.wireOp",EDGE,"E0.sketch_text.stroke-1243"),sQuery(id+"F0.wireOp",EDGE,"E0.sketch_text.stroke-1244"),sQuery(id+"F0.wireOp",EDGE,"E0.sketch_text.stroke-1245"),sQuery(id+"F0.wireOp",EDGE,"E0.sketch_text.stroke-1246"),sQuery(id+"F0.wireOp",EDGE,"E0.sketch_text.stroke-1247"),sQuery(id+"F0.wireOp",EDGE,"E0.sketch_text.stroke-1248"),sQuery(id+"F0.wireOp",EDGE,"E0.sketch_text.stroke-1249"),sQuery(id+"F0.wireOp",EDGE,"E0.sketch_text.stroke-1250"),sQuery(id+"F0.wireOp",EDGE,"E0.sketch_text.stroke-1251"),sQuery(id+"F0.wireOp",EDGE,"E0.sketch_text.stroke-1252"),sQuery(id+"F0.wireOp",EDGE,"E0.sketch_text.stroke-1253"),sQuery(id+"F0.wireOp",EDGE,"E0.sketch_text.stroke-1254")])]});
            var Q128;
            Q128=makeQuery(id+"F2.opExtrude","SWEPT_BODY",BODY,{"disambiguationData":[OSD([sQuery(id+"F0.wireOp",EDGE,"E0.sketch_text.stroke-1503"),sQuery(id+"F0.wireOp",EDGE,"E0.sketch_text.stroke-1504"),sQuery(id+"F0.wireOp",EDGE,"E0.sketch_text.stroke-1505"),sQuery(id+"F0.wireOp",EDGE,"E0.sketch_text.stroke-1506"),sQuery(id+"F0.wireOp",EDGE,"E0.sketch_text.stroke-1507"),sQuery(id+"F0.wireOp",EDGE,"E0.sketch_text.stroke-1508"),sQuery(id+"F0.wireOp",EDGE,"E0.sketch_text.stroke-1509"),sQuery(id+"F0.wireOp",EDGE,"E0.sketch_text.stroke-1510")])]});
            var Q129;
            Q129=makeQuery(id+"F2.opExtrude","SWEPT_BODY",BODY,{"disambiguationData":[OSD([sQuery(id+"F0.wireOp",EDGE,"E0.sketch_text.stroke-941"),sQuery(id+"F0.wireOp",EDGE,"E0.sketch_text.stroke-942"),sQuery(id+"F0.wireOp",EDGE,"E0.sketch_text.stroke-943"),sQuery(id+"F0.wireOp",EDGE,"E0.sketch_text.stroke-944")])]});
            var Q130;
            Q130=makeQuery(id+"F2.opExtrude","SWEPT_BODY",BODY,{"disambiguationData":[OSD([sQuery(id+"F0.wireOp",EDGE,"E0.sketch_text.stroke-970"),sQuery(id+"F0.wireOp",EDGE,"E0.sketch_text.stroke-971"),sQuery(id+"F0.wireOp",EDGE,"E0.sketch_text.stroke-972"),sQuery(id+"F0.wireOp",EDGE,"E0.sketch_text.stroke-973")])]});
            var Q131;
            Q131=makeQuery(id+"F2.opExtrude","SWEPT_BODY",BODY,{"disambiguationData":[OSD([sQuery(id+"F0.wireOp",EDGE,"E0.sketch_text.stroke-945"),sQuery(id+"F0.wireOp",EDGE,"E0.sketch_text.stroke-946"),sQuery(id+"F0.wireOp",EDGE,"E0.sketch_text.stroke-947"),sQuery(id+"F0.wireOp",EDGE,"E0.sketch_text.stroke-948"),sQuery(id+"F0.wireOp",EDGE,"E0.sketch_text.stroke-949"),sQuery(id+"F0.wireOp",EDGE,"E0.sketch_text.stroke-950"),sQuery(id+"F0.wireOp",EDGE,"E0.sketch_text.stroke-951"),sQuery(id+"F0.wireOp",EDGE,"E0.sketch_text.stroke-952")])]});
            var Q132;
            Q132=makeQuery(id+"F2.opExtrude","SWEPT_BODY",BODY,{"disambiguationData":[OSD([sQuery(id+"F0.wireOp",EDGE,"E0.sketch_text.stroke-1186"),sQuery(id+"F0.wireOp",EDGE,"E0.sketch_text.stroke-1187"),sQuery(id+"F0.wireOp",EDGE,"E0.sketch_text.stroke-1188"),sQuery(id+"F0.wireOp",EDGE,"E0.sketch_text.stroke-1189"),sQuery(id+"F0.wireOp",EDGE,"E0.sketch_text.stroke-1190"),sQuery(id+"F0.wireOp",EDGE,"E0.sketch_text.stroke-1191"),sQuery(id+"F0.wireOp",EDGE,"E0.sketch_text.stroke-1192"),sQuery(id+"F0.wireOp",EDGE,"E0.sketch_text.stroke-1193")])]});
            var Q133;
            Q133=makeQuery(id+"F2.opExtrude","SWEPT_BODY",BODY,{"disambiguationData":[OSD([sQuery(id+"F0.wireOp",EDGE,"E0.sketch_text.stroke-996"),sQuery(id+"F0.wireOp",EDGE,"E0.sketch_text.stroke-997"),sQuery(id+"F0.wireOp",EDGE,"E0.sketch_text.stroke-998"),sQuery(id+"F0.wireOp",EDGE,"E0.sketch_text.stroke-999"),sQuery(id+"F0.wireOp",EDGE,"E0.sketch_text.stroke-1000"),sQuery(id+"F0.wireOp",EDGE,"E0.sketch_text.stroke-1001"),sQuery(id+"F0.wireOp",EDGE,"E0.sketch_text.stroke-1002"),sQuery(id+"F0.wireOp",EDGE,"E0.sketch_text.stroke-1003")])]});
            var Q134;
            Q134=makeQuery(id+"F3.opExtrude","SWEPT_BODY",BODY,{"disambiguationData":[OSD([sQuery(id+"F1.wireOp",EDGE,"E1.bottom"),sQuery(id+"F1.wireOp",EDGE,"E1.top"),sQuery(id+"F1.wireOp",EDGE,"E1.left"),sQuery(id+"F1.wireOp",EDGE,"E1.right")])]});
            booleanBodies(context, id + "F4", {"operationType" : BooleanOperationType.SUBTRACTION, "tools" : qUnion([Q0, Q1, Q2, Q3, Q4, Q5, Q6, Q7, Q8, Q9, Q10, Q11, Q12, Q13, Q14, Q15, Q16, Q17, Q18, Q19, Q20, Q21, Q22, Q23, Q24, Q25, Q26, Q27, Q28, Q29, Q30, Q31, Q32, Q33, Q34, Q35, Q36, Q37, Q38, Q39, Q40, Q41, Q42, Q43, Q44, Q45, Q46, Q47, Q48, Q49, Q50, Q51, Q52, Q53, Q54, Q55, Q56, Q57, Q58, Q59, Q60, Q61, Q62, Q63, Q64, Q65, Q66, Q67, Q68, Q69, Q70, Q71, Q72, Q73, Q74, Q75, Q76, Q77, Q78, Q79, Q80, Q81, Q82, Q83, Q84, Q85, Q86, Q87, Q88, Q89, Q90, Q91, Q92, Q93, Q94, Q95, Q96, Q97, Q98, Q99, Q100, Q101, Q102, Q103, Q104, Q105, Q106, Q107, Q108, Q109, Q110, Q111, Q112, Q113, Q114, Q115, Q116, Q117, Q118, Q119, Q120, Q121, Q122, Q123, Q124, Q125, Q126, Q127, Q128, Q129, Q130, Q131, Q132, Q133]), "targets" : qUnion([Q134])});
        }
    });
